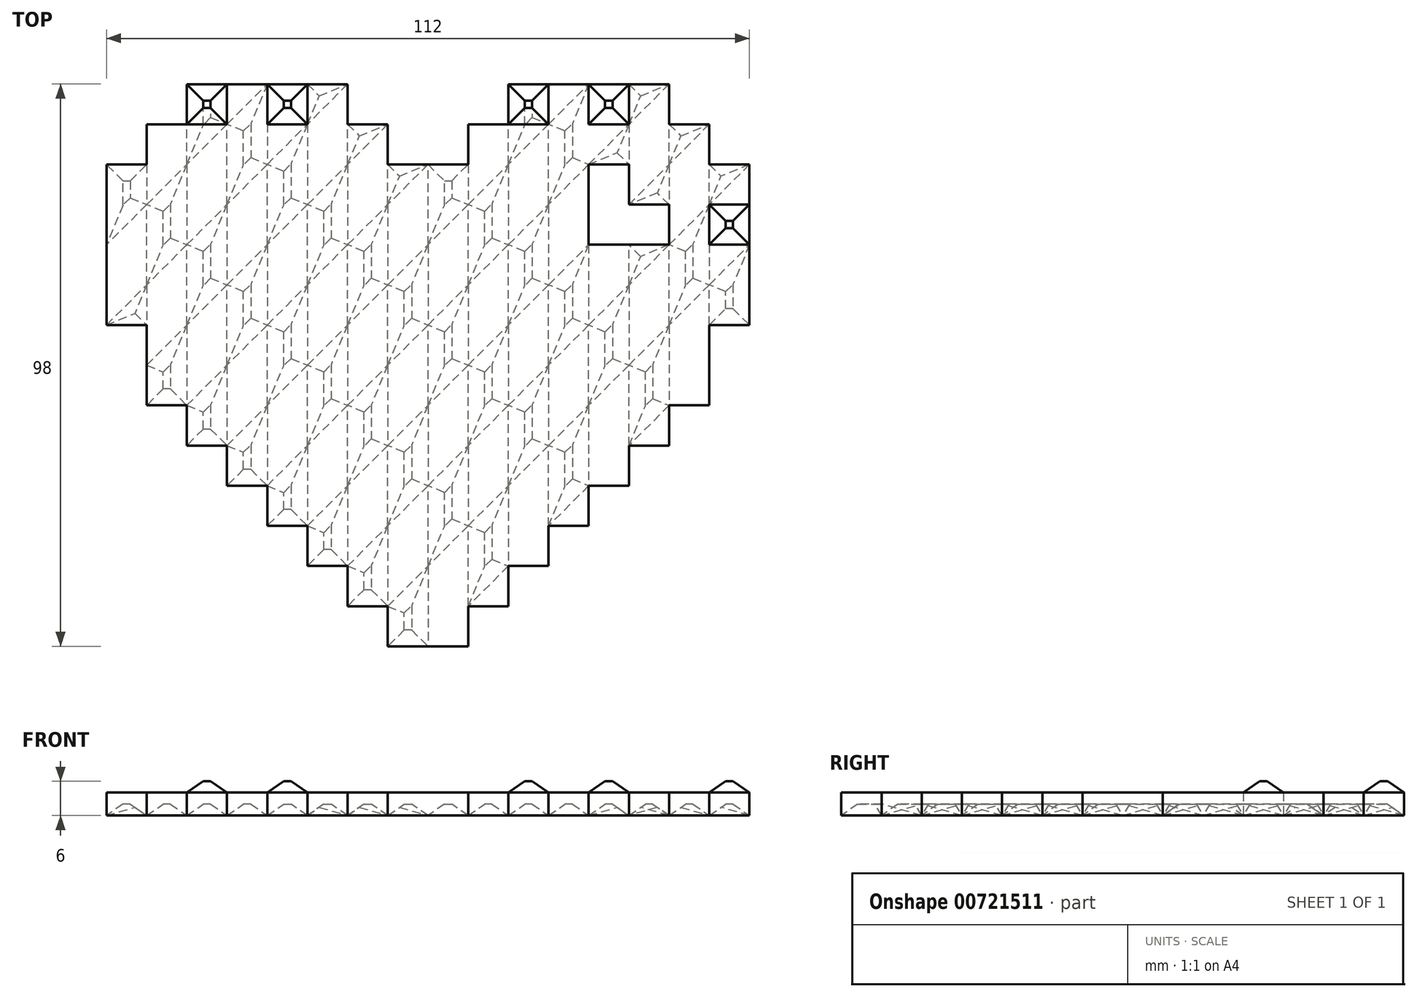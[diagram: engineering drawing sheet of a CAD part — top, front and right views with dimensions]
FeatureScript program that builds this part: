
annotation { "Feature Type Name" : "Feature", "Feature Type Description" : "" }
export const myFeature = defineFeature(function(context is Context, id is Id, definition is map)
    precondition{}
    {
        {
            var Q0;
            Q0=qCreatedBy(makeId("Top.planeOp"),FACE);
            var sketch = newSketch(context, id + "F0", { "sketchPlane" : qUnion([Q0])});
            skLineSegment(sketch, "E0", {"start": v(25.3, 13.05) * mm, "end": v(25.3, 20.05) * mm});
            skLineSegment(sketch, "E1", {"start": v(18.3, 20.05) * mm, "end": v(18.3, 6.05) * mm});
            skLineSegment(sketch, "E2", {"start": v(18.3, 6.05) * mm, "end": v(32.3, 6.05) * mm});
            skLineSegment(sketch, "E3", {"start": v(32.3, 6.05) * mm, "end": v(32.3, 13.05) * mm});
            skLineSegment(sketch, "E4", {"start": v(32.3, 13.05) * mm, "end": v(25.3, 13.05) * mm});
            skLineSegment(sketch, "E5", {"start": v(39.3, 20.05) * mm, "end": v(39.3, 27.05) * mm});
            skLineSegment(sketch, "E6", {"start": v(39.3, 27.05) * mm, "end": v(32.3, 27.05) * mm});
            skLineSegment(sketch, "E7", {"start": v(32.3, 27.05) * mm, "end": v(32.3, 34.05) * mm});
            skLineSegment(sketch, "E8", {"start": v(32.3, 34.05) * mm, "end": v(4.3, 34.05) * mm});
            skLineSegment(sketch, "E9", {"start": v(4.3, 34.05) * mm, "end": v(4.3, 27.05) * mm});
            skLineSegment(sketch, "E10", {"start": v(4.3, 27.05) * mm, "end": v(-2.7, 27.05) * mm});
            skLineSegment(sketch, "E11", {"start": v(-2.7, 27.05) * mm, "end": v(-2.7, 20.05) * mm});
            skLineSegment(sketch, "E12", {"start": v(-2.7, 20.05) * mm, "end": v(-16.7, 20.05) * mm});
            skLineSegment(sketch, "E13", {"start": v(-16.7, 20.05) * mm, "end": v(-16.7, 27.05) * mm});
            skLineSegment(sketch, "E14", {"start": v(-16.7, 27.05) * mm, "end": v(-23.7, 27.05) * mm});
            skLineSegment(sketch, "E15", {"start": v(-23.7, 27.05) * mm, "end": v(-23.7, 34.05) * mm});
            skLineSegment(sketch, "E16", {"start": v(-23.7, 34.05) * mm, "end": v(-51.7, 34.05) * mm});
            skLineSegment(sketch, "E17", {"start": v(-51.7, 34.05) * mm, "end": v(-51.7, 27.05) * mm});
            skLineSegment(sketch, "E18", {"start": v(-51.7, 27.05) * mm, "end": v(-58.7, 27.05) * mm});
            skLineSegment(sketch, "E19", {"start": v(-58.7, 27.05) * mm, "end": v(-58.7, 20.05) * mm});
            skLineSegment(sketch, "E20", {"start": v(-58.7, 20.05) * mm, "end": v(-65.7, 20.05) * mm});
            skLineSegment(sketch, "E21", {"start": v(-65.7, 20.05) * mm, "end": v(-65.7, -7.95) * mm});
            skLineSegment(sketch, "E22", {"start": v(-65.7, -7.95) * mm, "end": v(-58.7, -7.95) * mm});
            skLineSegment(sketch, "E23", {"start": v(-58.7, -7.95) * mm, "end": v(-58.7, -21.95) * mm});
            skLineSegment(sketch, "E24", {"start": v(-58.7, -21.95) * mm, "end": v(-51.7, -21.95) * mm});
            skLineSegment(sketch, "E25", {"start": v(-51.7, -21.95) * mm, "end": v(-51.7, -28.95) * mm});
            skLineSegment(sketch, "E26", {"start": v(-51.7, -28.95) * mm, "end": v(-44.7, -28.95) * mm});
            skLineSegment(sketch, "E27", {"start": v(-44.7, -28.95) * mm, "end": v(-44.7, -35.95) * mm});
            skLineSegment(sketch, "E28", {"start": v(-44.7, -35.95) * mm, "end": v(-37.7, -35.95) * mm});
            skLineSegment(sketch, "E29", {"start": v(-37.7, -35.95) * mm, "end": v(-37.7, -42.95) * mm});
            skLineSegment(sketch, "E30", {"start": v(-37.7, -42.95) * mm, "end": v(-30.7, -42.95) * mm});
            skLineSegment(sketch, "E31", {"start": v(-30.7, -42.95) * mm, "end": v(-30.7, -49.95) * mm});
            skLineSegment(sketch, "E32", {"start": v(-30.7, -49.95) * mm, "end": v(-23.7, -49.95) * mm});
            skLineSegment(sketch, "E33", {"start": v(-23.7, -49.95) * mm, "end": v(-23.7, -56.95) * mm});
            skLineSegment(sketch, "E34", {"start": v(-23.7, -56.95) * mm, "end": v(-16.7, -56.95) * mm});
            skLineSegment(sketch, "E35", {"start": v(-16.7, -56.95) * mm, "end": v(-16.7, -63.95) * mm});
            skLineSegment(sketch, "E36", {"start": v(-16.7, -63.95) * mm, "end": v(-2.7, -63.95) * mm});
            skLineSegment(sketch, "E37", {"start": v(-2.7, -63.95) * mm, "end": v(-2.7, -56.95) * mm});
            skLineSegment(sketch, "E38", {"start": v(-2.7, -56.95) * mm, "end": v(4.3, -56.95) * mm});
            skLineSegment(sketch, "E39", {"start": v(4.3, -56.95) * mm, "end": v(4.3, -49.95) * mm});
            skLineSegment(sketch, "E40", {"start": v(4.3, -49.95) * mm, "end": v(11.3, -49.95) * mm});
            skLineSegment(sketch, "E41", {"start": v(11.3, -49.95) * mm, "end": v(11.3, -42.95) * mm});
            skLineSegment(sketch, "E42", {"start": v(11.3, -42.95) * mm, "end": v(18.3, -42.95) * mm});
            skLineSegment(sketch, "E43", {"start": v(18.3, -42.95) * mm, "end": v(18.3, -35.95) * mm});
            skLineSegment(sketch, "E44", {"start": v(18.3, -35.95) * mm, "end": v(25.3, -35.95) * mm});
            skLineSegment(sketch, "E45", {"start": v(25.3, -35.95) * mm, "end": v(25.3, -28.95) * mm});
            skLineSegment(sketch, "E46", {"start": v(25.3, -28.95) * mm, "end": v(32.3, -28.95) * mm});
            skLineSegment(sketch, "E47", {"start": v(32.3, -28.95) * mm, "end": v(32.3, -21.95) * mm});
            skLineSegment(sketch, "E48", {"start": v(32.3, -21.95) * mm, "end": v(39.3, -21.95) * mm});
            skLineSegment(sketch, "E49", {"start": v(39.3, -21.95) * mm, "end": v(39.3, -7.95) * mm});
            skLineSegment(sketch, "E50", {"start": v(39.3, -7.95) * mm, "end": v(46.3, -7.95) * mm});
            skLineSegment(sketch, "E51", {"start": v(46.3, -7.95) * mm, "end": v(46.3, 20.05) * mm});
            skLineSegment(sketch, "E52", {"start": v(46.3, 20.05) * mm, "end": v(39.3, 20.05) * mm});
            skLineSegment(sketch, "E53", {"start": v(18.3, 20.05) * mm, "end": v(25.3, 20.05) * mm});
            skSolve(sketch);
        }
        {
            var Q0;
            Q0=makeQuery(id+"F0.imprint","IMPRINT",FACE,{"disambiguationData":[TD([[makeQuery(id+"F0.imprint","IMPRINT",EDGE,{"derivedFrom":sQuery(id+"F0.wireOp",EDGE,"E0")}),-1.0]])]});
            extrude(context, id + "F1", {"entities" : qUnion([Q0]), "depth" : 4 * mm, "offsetDistance" : 25 * mm});
        }
        {
            var Q0;
            Q0=makeQuery(id+"F1.opExtrude","CAP_FACE",FACE,{"disambiguationData":[OSD([sQuery(id+"F0.wireOp",EDGE,"E0"),sQuery(id+"F0.wireOp",EDGE,"E1"),sQuery(id+"F0.wireOp",EDGE,"E2"),sQuery(id+"F0.wireOp",EDGE,"E3"),sQuery(id+"F0.wireOp",EDGE,"E4"),sQuery(id+"F0.wireOp",EDGE,"E5"),sQuery(id+"F0.wireOp",EDGE,"E6"),sQuery(id+"F0.wireOp",EDGE,"E7"),sQuery(id+"F0.wireOp",EDGE,"E8"),sQuery(id+"F0.wireOp",EDGE,"E9"),sQuery(id+"F0.wireOp",EDGE,"E10"),sQuery(id+"F0.wireOp",EDGE,"E11"),sQuery(id+"F0.wireOp",EDGE,"E12"),sQuery(id+"F0.wireOp",EDGE,"E13"),sQuery(id+"F0.wireOp",EDGE,"E14"),sQuery(id+"F0.wireOp",EDGE,"E15"),sQuery(id+"F0.wireOp",EDGE,"E16"),sQuery(id+"F0.wireOp",EDGE,"E17"),sQuery(id+"F0.wireOp",EDGE,"E18"),sQuery(id+"F0.wireOp",EDGE,"E19"),sQuery(id+"F0.wireOp",EDGE,"E20"),sQuery(id+"F0.wireOp",EDGE,"E21"),sQuery(id+"F0.wireOp",EDGE,"E22"),sQuery(id+"F0.wireOp",EDGE,"E23"),sQuery(id+"F0.wireOp",EDGE,"E24"),sQuery(id+"F0.wireOp",EDGE,"E25"),sQuery(id+"F0.wireOp",EDGE,"E26"),sQuery(id+"F0.wireOp",EDGE,"E27"),sQuery(id+"F0.wireOp",EDGE,"E28"),sQuery(id+"F0.wireOp",EDGE,"E29"),sQuery(id+"F0.wireOp",EDGE,"E30"),sQuery(id+"F0.wireOp",EDGE,"E31"),sQuery(id+"F0.wireOp",EDGE,"E32"),sQuery(id+"F0.wireOp",EDGE,"E33"),sQuery(id+"F0.wireOp",EDGE,"E34"),sQuery(id+"F0.wireOp",EDGE,"E35"),sQuery(id+"F0.wireOp",EDGE,"E36"),sQuery(id+"F0.wireOp",EDGE,"E37"),sQuery(id+"F0.wireOp",EDGE,"E38"),sQuery(id+"F0.wireOp",EDGE,"E39"),sQuery(id+"F0.wireOp",EDGE,"E40"),sQuery(id+"F0.wireOp",EDGE,"E41"),sQuery(id+"F0.wireOp",EDGE,"E42"),sQuery(id+"F0.wireOp",EDGE,"E43"),sQuery(id+"F0.wireOp",EDGE,"E44"),sQuery(id+"F0.wireOp",EDGE,"E45"),sQuery(id+"F0.wireOp",EDGE,"E46"),sQuery(id+"F0.wireOp",EDGE,"E47"),sQuery(id+"F0.wireOp",EDGE,"E48"),sQuery(id+"F0.wireOp",EDGE,"E49"),sQuery(id+"F0.wireOp",EDGE,"E50"),sQuery(id+"F0.wireOp",EDGE,"E51"),sQuery(id+"F0.wireOp",EDGE,"E52"),sQuery(id+"F0.wireOp",EDGE,"E53")])],"isStart":false});
            var sketch = newSketch(context, id + "F2", { "sketchPlane" : qUnion([Q0])});
            skLineSegment(sketch, "E54.bottom", {"start": v(-58.7, 27.05) * mm, "end": v(-65.7, 27.05) * mm});
            skLineSegment(sketch, "E54.top", {"start": v(-58.7, 34.05) * mm, "end": v(-65.7, 34.05) * mm});
            skLineSegment(sketch, "E54.left", {"start": v(-58.7, 27.05) * mm, "end": v(-58.7, 34.05) * mm});
            skLineSegment(sketch, "E54.right", {"start": v(-65.7, 27.05) * mm, "end": v(-65.7, 34.05) * mm});
            skLineSegment(sketch, "E55.0.1.0", {"start": v(-58.7, 20.05) * mm, "end": v(-58.7, 27.05) * mm});
            skLineSegment(sketch, "E55.0.1.2", {"start": v(-58.7, 20.05) * mm, "end": v(-65.7, 20.05) * mm});
            skLineSegment(sketch, "E55.0.1.3", {"start": v(-65.7, 20.05) * mm, "end": v(-65.7, 27.05) * mm});
            skLineSegment(sketch, "E55.0.2.0", {"start": v(-58.7, 13.05) * mm, "end": v(-58.7, 20.05) * mm});
            skLineSegment(sketch, "E55.0.2.1", {"start": v(-58.7, 20.05) * mm, "end": v(-65.7, 20.05) * mm});
            skLineSegment(sketch, "E55.0.2.2", {"start": v(-58.7, 13.05) * mm, "end": v(-65.7, 13.05) * mm});
            skLineSegment(sketch, "E55.0.2.3", {"start": v(-65.7, 13.05) * mm, "end": v(-65.7, 20.05) * mm});
            skLineSegment(sketch, "E55.0.3.0", {"start": v(-58.7, 6.05) * mm, "end": v(-58.7, 13.05) * mm});
            skLineSegment(sketch, "E55.0.3.1", {"start": v(-58.7, 13.05) * mm, "end": v(-65.7, 13.05) * mm});
            skLineSegment(sketch, "E55.0.3.2", {"start": v(-58.7, 6.05) * mm, "end": v(-65.7, 6.05) * mm});
            skLineSegment(sketch, "E55.0.3.3", {"start": v(-65.7, 6.05) * mm, "end": v(-65.7, 13.05) * mm});
            skLineSegment(sketch, "E55.0.4.0", {"start": v(-58.7, -0.95) * mm, "end": v(-58.7, 6.05) * mm});
            skLineSegment(sketch, "E55.0.4.1", {"start": v(-58.7, 6.05) * mm, "end": v(-65.7, 6.05) * mm});
            skLineSegment(sketch, "E55.0.4.2", {"start": v(-58.7, -0.95) * mm, "end": v(-65.7, -0.95) * mm});
            skLineSegment(sketch, "E55.0.4.3", {"start": v(-65.7, -0.95) * mm, "end": v(-65.7, 6.05) * mm});
            skLineSegment(sketch, "E55.0.5.0", {"start": v(-58.7, -7.95) * mm, "end": v(-58.7, -0.95) * mm});
            skLineSegment(sketch, "E55.0.5.1", {"start": v(-58.7, -0.95) * mm, "end": v(-65.7, -0.95) * mm});
            skLineSegment(sketch, "E55.0.5.2", {"start": v(-58.7, -7.95) * mm, "end": v(-65.7, -7.95) * mm});
            skLineSegment(sketch, "E55.0.5.3", {"start": v(-65.7, -7.95) * mm, "end": v(-65.7, -0.95) * mm});
            skLineSegment(sketch, "E55.0.6.0", {"start": v(-58.7, -14.95) * mm, "end": v(-58.7, -7.95) * mm});
            skLineSegment(sketch, "E55.0.6.1", {"start": v(-58.7, -7.95) * mm, "end": v(-65.7, -7.95) * mm});
            skLineSegment(sketch, "E55.0.6.2", {"start": v(-58.7, -14.95) * mm, "end": v(-65.7, -14.95) * mm});
            skLineSegment(sketch, "E55.0.6.3", {"start": v(-65.7, -14.95) * mm, "end": v(-65.7, -7.95) * mm});
            skLineSegment(sketch, "E55.0.7.0", {"start": v(-58.7, -21.95) * mm, "end": v(-58.7, -14.95) * mm});
            skLineSegment(sketch, "E55.0.7.1", {"start": v(-58.7, -14.95) * mm, "end": v(-65.7, -14.95) * mm});
            skLineSegment(sketch, "E55.0.7.2", {"start": v(-58.7, -21.95) * mm, "end": v(-65.7, -21.95) * mm});
            skLineSegment(sketch, "E55.0.7.3", {"start": v(-65.7, -21.95) * mm, "end": v(-65.7, -14.95) * mm});
            skLineSegment(sketch, "E55.0.8.0", {"start": v(-58.7, -28.95) * mm, "end": v(-58.7, -21.95) * mm});
            skLineSegment(sketch, "E55.0.8.1", {"start": v(-58.7, -21.95) * mm, "end": v(-65.7, -21.95) * mm});
            skLineSegment(sketch, "E55.0.8.2", {"start": v(-58.7, -28.95) * mm, "end": v(-65.7, -28.95) * mm});
            skLineSegment(sketch, "E55.0.8.3", {"start": v(-65.7, -28.95) * mm, "end": v(-65.7, -21.95) * mm});
            skLineSegment(sketch, "E55.0.9.0", {"start": v(-58.7, -35.95) * mm, "end": v(-58.7, -28.95) * mm});
            skLineSegment(sketch, "E55.0.9.1", {"start": v(-58.7, -28.95) * mm, "end": v(-65.7, -28.95) * mm});
            skLineSegment(sketch, "E55.0.9.2", {"start": v(-58.7, -35.95) * mm, "end": v(-65.7, -35.95) * mm});
            skLineSegment(sketch, "E55.0.9.3", {"start": v(-65.7, -35.95) * mm, "end": v(-65.7, -28.95) * mm});
            skLineSegment(sketch, "E55.0.10.0", {"start": v(-58.7, -42.95) * mm, "end": v(-58.7, -35.95) * mm});
            skLineSegment(sketch, "E55.0.10.1", {"start": v(-58.7, -35.95) * mm, "end": v(-65.7, -35.95) * mm});
            skLineSegment(sketch, "E55.0.10.2", {"start": v(-58.7, -42.95) * mm, "end": v(-65.7, -42.95) * mm});
            skLineSegment(sketch, "E55.0.10.3", {"start": v(-65.7, -42.95) * mm, "end": v(-65.7, -35.95) * mm});
            skLineSegment(sketch, "E55.0.11.0", {"start": v(-58.7, -49.95) * mm, "end": v(-58.7, -42.95) * mm});
            skLineSegment(sketch, "E55.0.11.1", {"start": v(-58.7, -42.95) * mm, "end": v(-65.7, -42.95) * mm});
            skLineSegment(sketch, "E55.0.11.2", {"start": v(-58.7, -49.95) * mm, "end": v(-65.7, -49.95) * mm});
            skLineSegment(sketch, "E55.0.11.3", {"start": v(-65.7, -49.95) * mm, "end": v(-65.7, -42.95) * mm});
            skLineSegment(sketch, "E55.0.12.0", {"start": v(-58.7, -56.95) * mm, "end": v(-58.7, -49.95) * mm});
            skLineSegment(sketch, "E55.0.12.1", {"start": v(-58.7, -49.95) * mm, "end": v(-65.7, -49.95) * mm});
            skLineSegment(sketch, "E55.0.12.2", {"start": v(-58.7, -56.95) * mm, "end": v(-65.7, -56.95) * mm});
            skLineSegment(sketch, "E55.0.12.3", {"start": v(-65.7, -56.95) * mm, "end": v(-65.7, -49.95) * mm});
            skLineSegment(sketch, "E55.0.13.0", {"start": v(-58.7, -63.95) * mm, "end": v(-58.7, -56.95) * mm});
            skLineSegment(sketch, "E55.0.13.1", {"start": v(-58.7, -56.95) * mm, "end": v(-65.7, -56.95) * mm});
            skLineSegment(sketch, "E55.0.13.2", {"start": v(-58.7, -63.95) * mm, "end": v(-65.7, -63.95) * mm});
            skLineSegment(sketch, "E55.0.13.3", {"start": v(-65.7, -63.95) * mm, "end": v(-65.7, -56.95) * mm});
            skLineSegment(sketch, "E55.0.14.0", {"start": v(-58.7, -70.95) * mm, "end": v(-58.7, -63.95) * mm});
            skLineSegment(sketch, "E55.0.14.1", {"start": v(-58.7, -63.95) * mm, "end": v(-65.7, -63.95) * mm});
            skLineSegment(sketch, "E55.0.14.2", {"start": v(-58.7, -70.95) * mm, "end": v(-65.7, -70.95) * mm});
            skLineSegment(sketch, "E55.0.14.3", {"start": v(-65.7, -70.95) * mm, "end": v(-65.7, -63.95) * mm});
            skLineSegment(sketch, "E55.0.15.0", {"start": v(-58.7, -77.95) * mm, "end": v(-58.7, -70.95) * mm});
            skLineSegment(sketch, "E55.0.15.1", {"start": v(-58.7, -70.95) * mm, "end": v(-65.7, -70.95) * mm});
            skLineSegment(sketch, "E55.0.15.2", {"start": v(-58.7, -77.95) * mm, "end": v(-65.7, -77.95) * mm});
            skLineSegment(sketch, "E55.0.15.3", {"start": v(-65.7, -77.95) * mm, "end": v(-65.7, -70.95) * mm});
            skLineSegment(sketch, "E55.1.0.0", {"start": v(-51.7, 27.05) * mm, "end": v(-51.7, 34.05) * mm});
            skLineSegment(sketch, "E55.1.0.1", {"start": v(-51.7, 34.05) * mm, "end": v(-58.7, 34.05) * mm});
            skLineSegment(sketch, "E55.1.0.2", {"start": v(-51.7, 27.05) * mm, "end": v(-58.7, 27.05) * mm});
            skLineSegment(sketch, "E55.1.1.0", {"start": v(-51.7, 20.05) * mm, "end": v(-51.7, 27.05) * mm});
            skLineSegment(sketch, "E55.1.1.1", {"start": v(-51.7, 27.05) * mm, "end": v(-58.7, 27.05) * mm});
            skLineSegment(sketch, "E55.1.1.2", {"start": v(-51.7, 20.05) * mm, "end": v(-58.7, 20.05) * mm});
            skLineSegment(sketch, "E55.1.1.3", {"start": v(-58.7, 20.05) * mm, "end": v(-58.7, 27.05) * mm});
            skLineSegment(sketch, "E55.1.2.0", {"start": v(-51.7, 13.05) * mm, "end": v(-51.7, 20.05) * mm});
            skLineSegment(sketch, "E55.1.2.1", {"start": v(-51.7, 20.05) * mm, "end": v(-58.7, 20.05) * mm});
            skLineSegment(sketch, "E55.1.2.2", {"start": v(-51.7, 13.05) * mm, "end": v(-58.7, 13.05) * mm});
            skLineSegment(sketch, "E55.1.2.3", {"start": v(-58.7, 13.05) * mm, "end": v(-58.7, 20.05) * mm});
            skLineSegment(sketch, "E55.1.3.0", {"start": v(-51.7, 6.05) * mm, "end": v(-51.7, 13.05) * mm});
            skLineSegment(sketch, "E55.1.3.1", {"start": v(-51.7, 13.05) * mm, "end": v(-58.7, 13.05) * mm});
            skLineSegment(sketch, "E55.1.3.2", {"start": v(-51.7, 6.05) * mm, "end": v(-58.7, 6.05) * mm});
            skLineSegment(sketch, "E55.1.3.3", {"start": v(-58.7, 6.05) * mm, "end": v(-58.7, 13.05) * mm});
            skLineSegment(sketch, "E55.1.4.0", {"start": v(-51.7, -0.95) * mm, "end": v(-51.7, 6.05) * mm});
            skLineSegment(sketch, "E55.1.4.1", {"start": v(-51.7, 6.05) * mm, "end": v(-58.7, 6.05) * mm});
            skLineSegment(sketch, "E55.1.4.2", {"start": v(-51.7, -0.95) * mm, "end": v(-58.7, -0.95) * mm});
            skLineSegment(sketch, "E55.1.4.3", {"start": v(-58.7, -0.95) * mm, "end": v(-58.7, 6.05) * mm});
            skLineSegment(sketch, "E55.1.5.0", {"start": v(-51.7, -7.95) * mm, "end": v(-51.7, -0.95) * mm});
            skLineSegment(sketch, "E55.1.5.1", {"start": v(-51.7, -0.95) * mm, "end": v(-58.7, -0.95) * mm});
            skLineSegment(sketch, "E55.1.5.2", {"start": v(-51.7, -7.95) * mm, "end": v(-58.7, -7.95) * mm});
            skLineSegment(sketch, "E55.1.5.3", {"start": v(-58.7, -7.95) * mm, "end": v(-58.7, -0.95) * mm});
            skLineSegment(sketch, "E55.1.6.0", {"start": v(-51.7, -14.95) * mm, "end": v(-51.7, -7.95) * mm});
            skLineSegment(sketch, "E55.1.6.1", {"start": v(-51.7, -7.95) * mm, "end": v(-58.7, -7.95) * mm});
            skLineSegment(sketch, "E55.1.6.2", {"start": v(-51.7, -14.95) * mm, "end": v(-58.7, -14.95) * mm});
            skLineSegment(sketch, "E55.1.6.3", {"start": v(-58.7, -14.95) * mm, "end": v(-58.7, -7.95) * mm});
            skLineSegment(sketch, "E55.1.7.0", {"start": v(-51.7, -21.95) * mm, "end": v(-51.7, -14.95) * mm});
            skLineSegment(sketch, "E55.1.7.1", {"start": v(-51.7, -14.95) * mm, "end": v(-58.7, -14.95) * mm});
            skLineSegment(sketch, "E55.1.7.2", {"start": v(-51.7, -21.95) * mm, "end": v(-58.7, -21.95) * mm});
            skLineSegment(sketch, "E55.1.7.3", {"start": v(-58.7, -21.95) * mm, "end": v(-58.7, -14.95) * mm});
            skLineSegment(sketch, "E55.1.8.0", {"start": v(-51.7, -28.95) * mm, "end": v(-51.7, -21.95) * mm});
            skLineSegment(sketch, "E55.1.8.1", {"start": v(-51.7, -21.95) * mm, "end": v(-58.7, -21.95) * mm});
            skLineSegment(sketch, "E55.1.8.2", {"start": v(-51.7, -28.95) * mm, "end": v(-58.7, -28.95) * mm});
            skLineSegment(sketch, "E55.1.8.3", {"start": v(-58.7, -28.95) * mm, "end": v(-58.7, -21.95) * mm});
            skLineSegment(sketch, "E55.1.9.0", {"start": v(-51.7, -35.95) * mm, "end": v(-51.7, -28.95) * mm});
            skLineSegment(sketch, "E55.1.9.1", {"start": v(-51.7, -28.95) * mm, "end": v(-58.7, -28.95) * mm});
            skLineSegment(sketch, "E55.1.9.2", {"start": v(-51.7, -35.95) * mm, "end": v(-58.7, -35.95) * mm});
            skLineSegment(sketch, "E55.1.9.3", {"start": v(-58.7, -35.95) * mm, "end": v(-58.7, -28.95) * mm});
            skLineSegment(sketch, "E55.1.10.0", {"start": v(-51.7, -42.95) * mm, "end": v(-51.7, -35.95) * mm});
            skLineSegment(sketch, "E55.1.10.1", {"start": v(-51.7, -35.95) * mm, "end": v(-58.7, -35.95) * mm});
            skLineSegment(sketch, "E55.1.10.2", {"start": v(-51.7, -42.95) * mm, "end": v(-58.7, -42.95) * mm});
            skLineSegment(sketch, "E55.1.10.3", {"start": v(-58.7, -42.95) * mm, "end": v(-58.7, -35.95) * mm});
            skLineSegment(sketch, "E55.1.11.0", {"start": v(-51.7, -49.95) * mm, "end": v(-51.7, -42.95) * mm});
            skLineSegment(sketch, "E55.1.11.1", {"start": v(-51.7, -42.95) * mm, "end": v(-58.7, -42.95) * mm});
            skLineSegment(sketch, "E55.1.11.2", {"start": v(-51.7, -49.95) * mm, "end": v(-58.7, -49.95) * mm});
            skLineSegment(sketch, "E55.1.11.3", {"start": v(-58.7, -49.95) * mm, "end": v(-58.7, -42.95) * mm});
            skLineSegment(sketch, "E55.1.12.0", {"start": v(-51.7, -56.95) * mm, "end": v(-51.7, -49.95) * mm});
            skLineSegment(sketch, "E55.1.12.1", {"start": v(-51.7, -49.95) * mm, "end": v(-58.7, -49.95) * mm});
            skLineSegment(sketch, "E55.1.12.2", {"start": v(-51.7, -56.95) * mm, "end": v(-58.7, -56.95) * mm});
            skLineSegment(sketch, "E55.1.12.3", {"start": v(-58.7, -56.95) * mm, "end": v(-58.7, -49.95) * mm});
            skLineSegment(sketch, "E55.1.13.0", {"start": v(-51.7, -63.95) * mm, "end": v(-51.7, -56.95) * mm});
            skLineSegment(sketch, "E55.1.13.1", {"start": v(-51.7, -56.95) * mm, "end": v(-58.7, -56.95) * mm});
            skLineSegment(sketch, "E55.1.13.2", {"start": v(-51.7, -63.95) * mm, "end": v(-58.7, -63.95) * mm});
            skLineSegment(sketch, "E55.1.13.3", {"start": v(-58.7, -63.95) * mm, "end": v(-58.7, -56.95) * mm});
            skLineSegment(sketch, "E55.1.14.0", {"start": v(-51.7, -70.95) * mm, "end": v(-51.7, -63.95) * mm});
            skLineSegment(sketch, "E55.1.14.1", {"start": v(-51.7, -63.95) * mm, "end": v(-58.7, -63.95) * mm});
            skLineSegment(sketch, "E55.1.14.2", {"start": v(-51.7, -70.95) * mm, "end": v(-58.7, -70.95) * mm});
            skLineSegment(sketch, "E55.1.14.3", {"start": v(-58.7, -70.95) * mm, "end": v(-58.7, -63.95) * mm});
            skLineSegment(sketch, "E55.1.15.0", {"start": v(-51.7, -77.95) * mm, "end": v(-51.7, -70.95) * mm});
            skLineSegment(sketch, "E55.1.15.1", {"start": v(-51.7, -70.95) * mm, "end": v(-58.7, -70.95) * mm});
            skLineSegment(sketch, "E55.1.15.2", {"start": v(-51.7, -77.95) * mm, "end": v(-58.7, -77.95) * mm});
            skLineSegment(sketch, "E55.1.15.3", {"start": v(-58.7, -77.95) * mm, "end": v(-58.7, -70.95) * mm});
            skLineSegment(sketch, "E55.2.0.0", {"start": v(-44.7, 27.05) * mm, "end": v(-44.7, 34.05) * mm});
            skLineSegment(sketch, "E55.2.0.1", {"start": v(-44.7, 34.05) * mm, "end": v(-51.7, 34.05) * mm});
            skLineSegment(sketch, "E55.2.0.2", {"start": v(-44.7, 27.05) * mm, "end": v(-51.7, 27.05) * mm});
            skLineSegment(sketch, "E55.2.0.3", {"start": v(-51.7, 27.05) * mm, "end": v(-51.7, 34.05) * mm});
            skLineSegment(sketch, "E55.2.1.0", {"start": v(-44.7, 20.05) * mm, "end": v(-44.7, 27.05) * mm});
            skLineSegment(sketch, "E55.2.1.1", {"start": v(-44.7, 27.05) * mm, "end": v(-51.7, 27.05) * mm});
            skLineSegment(sketch, "E55.2.1.2", {"start": v(-44.7, 20.05) * mm, "end": v(-51.7, 20.05) * mm});
            skLineSegment(sketch, "E55.2.1.3", {"start": v(-51.7, 20.05) * mm, "end": v(-51.7, 27.05) * mm});
            skLineSegment(sketch, "E55.2.2.0", {"start": v(-44.7, 13.05) * mm, "end": v(-44.7, 20.05) * mm});
            skLineSegment(sketch, "E55.2.2.1", {"start": v(-44.7, 20.05) * mm, "end": v(-51.7, 20.05) * mm});
            skLineSegment(sketch, "E55.2.2.2", {"start": v(-44.7, 13.05) * mm, "end": v(-51.7, 13.05) * mm});
            skLineSegment(sketch, "E55.2.2.3", {"start": v(-51.7, 13.05) * mm, "end": v(-51.7, 20.05) * mm});
            skLineSegment(sketch, "E55.2.3.0", {"start": v(-44.7, 6.05) * mm, "end": v(-44.7, 13.05) * mm});
            skLineSegment(sketch, "E55.2.3.1", {"start": v(-44.7, 13.05) * mm, "end": v(-51.7, 13.05) * mm});
            skLineSegment(sketch, "E55.2.3.2", {"start": v(-44.7, 6.05) * mm, "end": v(-51.7, 6.05) * mm});
            skLineSegment(sketch, "E55.2.3.3", {"start": v(-51.7, 6.05) * mm, "end": v(-51.7, 13.05) * mm});
            skLineSegment(sketch, "E55.2.4.0", {"start": v(-44.7, -0.95) * mm, "end": v(-44.7, 6.05) * mm});
            skLineSegment(sketch, "E55.2.4.1", {"start": v(-44.7, 6.05) * mm, "end": v(-51.7, 6.05) * mm});
            skLineSegment(sketch, "E55.2.4.2", {"start": v(-44.7, -0.95) * mm, "end": v(-51.7, -0.95) * mm});
            skLineSegment(sketch, "E55.2.4.3", {"start": v(-51.7, -0.95) * mm, "end": v(-51.7, 6.05) * mm});
            skLineSegment(sketch, "E55.2.5.0", {"start": v(-44.7, -7.95) * mm, "end": v(-44.7, -0.95) * mm});
            skLineSegment(sketch, "E55.2.5.1", {"start": v(-44.7, -0.95) * mm, "end": v(-51.7, -0.95) * mm});
            skLineSegment(sketch, "E55.2.5.2", {"start": v(-44.7, -7.95) * mm, "end": v(-51.7, -7.95) * mm});
            skLineSegment(sketch, "E55.2.5.3", {"start": v(-51.7, -7.95) * mm, "end": v(-51.7, -0.95) * mm});
            skLineSegment(sketch, "E55.2.6.0", {"start": v(-44.7, -14.95) * mm, "end": v(-44.7, -7.95) * mm});
            skLineSegment(sketch, "E55.2.6.1", {"start": v(-44.7, -7.95) * mm, "end": v(-51.7, -7.95) * mm});
            skLineSegment(sketch, "E55.2.6.2", {"start": v(-44.7, -14.95) * mm, "end": v(-51.7, -14.95) * mm});
            skLineSegment(sketch, "E55.2.6.3", {"start": v(-51.7, -14.95) * mm, "end": v(-51.7, -7.95) * mm});
            skLineSegment(sketch, "E55.2.7.0", {"start": v(-44.7, -21.95) * mm, "end": v(-44.7, -14.95) * mm});
            skLineSegment(sketch, "E55.2.7.1", {"start": v(-44.7, -14.95) * mm, "end": v(-51.7, -14.95) * mm});
            skLineSegment(sketch, "E55.2.7.2", {"start": v(-44.7, -21.95) * mm, "end": v(-51.7, -21.95) * mm});
            skLineSegment(sketch, "E55.2.7.3", {"start": v(-51.7, -21.95) * mm, "end": v(-51.7, -14.95) * mm});
            skLineSegment(sketch, "E55.2.8.0", {"start": v(-44.7, -28.95) * mm, "end": v(-44.7, -21.95) * mm});
            skLineSegment(sketch, "E55.2.8.1", {"start": v(-44.7, -21.95) * mm, "end": v(-51.7, -21.95) * mm});
            skLineSegment(sketch, "E55.2.8.2", {"start": v(-44.7, -28.95) * mm, "end": v(-51.7, -28.95) * mm});
            skLineSegment(sketch, "E55.2.8.3", {"start": v(-51.7, -28.95) * mm, "end": v(-51.7, -21.95) * mm});
            skLineSegment(sketch, "E55.2.9.0", {"start": v(-44.7, -35.95) * mm, "end": v(-44.7, -28.95) * mm});
            skLineSegment(sketch, "E55.2.9.1", {"start": v(-44.7, -28.95) * mm, "end": v(-51.7, -28.95) * mm});
            skLineSegment(sketch, "E55.2.9.2", {"start": v(-44.7, -35.95) * mm, "end": v(-51.7, -35.95) * mm});
            skLineSegment(sketch, "E55.2.9.3", {"start": v(-51.7, -35.95) * mm, "end": v(-51.7, -28.95) * mm});
            skLineSegment(sketch, "E55.2.10.0", {"start": v(-44.7, -42.95) * mm, "end": v(-44.7, -35.95) * mm});
            skLineSegment(sketch, "E55.2.10.1", {"start": v(-44.7, -35.95) * mm, "end": v(-51.7, -35.95) * mm});
            skLineSegment(sketch, "E55.2.10.2", {"start": v(-44.7, -42.95) * mm, "end": v(-51.7, -42.95) * mm});
            skLineSegment(sketch, "E55.2.10.3", {"start": v(-51.7, -42.95) * mm, "end": v(-51.7, -35.95) * mm});
            skLineSegment(sketch, "E55.2.11.0", {"start": v(-44.7, -49.95) * mm, "end": v(-44.7, -42.95) * mm});
            skLineSegment(sketch, "E55.2.11.1", {"start": v(-44.7, -42.95) * mm, "end": v(-51.7, -42.95) * mm});
            skLineSegment(sketch, "E55.2.11.2", {"start": v(-44.7, -49.95) * mm, "end": v(-51.7, -49.95) * mm});
            skLineSegment(sketch, "E55.2.11.3", {"start": v(-51.7, -49.95) * mm, "end": v(-51.7, -42.95) * mm});
            skLineSegment(sketch, "E55.2.12.0", {"start": v(-44.7, -56.95) * mm, "end": v(-44.7, -49.95) * mm});
            skLineSegment(sketch, "E55.2.12.1", {"start": v(-44.7, -49.95) * mm, "end": v(-51.7, -49.95) * mm});
            skLineSegment(sketch, "E55.2.12.2", {"start": v(-44.7, -56.95) * mm, "end": v(-51.7, -56.95) * mm});
            skLineSegment(sketch, "E55.2.12.3", {"start": v(-51.7, -56.95) * mm, "end": v(-51.7, -49.95) * mm});
            skLineSegment(sketch, "E55.2.13.0", {"start": v(-44.7, -63.95) * mm, "end": v(-44.7, -56.95) * mm});
            skLineSegment(sketch, "E55.2.13.1", {"start": v(-44.7, -56.95) * mm, "end": v(-51.7, -56.95) * mm});
            skLineSegment(sketch, "E55.2.13.2", {"start": v(-44.7, -63.95) * mm, "end": v(-51.7, -63.95) * mm});
            skLineSegment(sketch, "E55.2.13.3", {"start": v(-51.7, -63.95) * mm, "end": v(-51.7, -56.95) * mm});
            skLineSegment(sketch, "E55.2.14.0", {"start": v(-44.7, -70.95) * mm, "end": v(-44.7, -63.95) * mm});
            skLineSegment(sketch, "E55.2.14.1", {"start": v(-44.7, -63.95) * mm, "end": v(-51.7, -63.95) * mm});
            skLineSegment(sketch, "E55.2.14.2", {"start": v(-44.7, -70.95) * mm, "end": v(-51.7, -70.95) * mm});
            skLineSegment(sketch, "E55.2.14.3", {"start": v(-51.7, -70.95) * mm, "end": v(-51.7, -63.95) * mm});
            skLineSegment(sketch, "E55.2.15.0", {"start": v(-44.7, -77.95) * mm, "end": v(-44.7, -70.95) * mm});
            skLineSegment(sketch, "E55.2.15.1", {"start": v(-44.7, -70.95) * mm, "end": v(-51.7, -70.95) * mm});
            skLineSegment(sketch, "E55.2.15.2", {"start": v(-44.7, -77.95) * mm, "end": v(-51.7, -77.95) * mm});
            skLineSegment(sketch, "E55.2.15.3", {"start": v(-51.7, -77.95) * mm, "end": v(-51.7, -70.95) * mm});
            skLineSegment(sketch, "E55.3.0.0", {"start": v(-37.7, 27.05) * mm, "end": v(-37.7, 34.05) * mm});
            skLineSegment(sketch, "E55.3.0.1", {"start": v(-37.7, 34.05) * mm, "end": v(-44.7, 34.05) * mm});
            skLineSegment(sketch, "E55.3.0.2", {"start": v(-37.7, 27.05) * mm, "end": v(-44.7, 27.05) * mm});
            skLineSegment(sketch, "E55.3.0.3", {"start": v(-44.7, 27.05) * mm, "end": v(-44.7, 34.05) * mm});
            skLineSegment(sketch, "E55.3.1.0", {"start": v(-37.7, 20.05) * mm, "end": v(-37.7, 27.05) * mm});
            skLineSegment(sketch, "E55.3.1.1", {"start": v(-37.7, 27.05) * mm, "end": v(-44.7, 27.05) * mm});
            skLineSegment(sketch, "E55.3.1.2", {"start": v(-37.7, 20.05) * mm, "end": v(-44.7, 20.05) * mm});
            skLineSegment(sketch, "E55.3.1.3", {"start": v(-44.7, 20.05) * mm, "end": v(-44.7, 27.05) * mm});
            skLineSegment(sketch, "E55.3.2.0", {"start": v(-37.7, 13.05) * mm, "end": v(-37.7, 20.05) * mm});
            skLineSegment(sketch, "E55.3.2.1", {"start": v(-37.7, 20.05) * mm, "end": v(-44.7, 20.05) * mm});
            skLineSegment(sketch, "E55.3.2.2", {"start": v(-37.7, 13.05) * mm, "end": v(-44.7, 13.05) * mm});
            skLineSegment(sketch, "E55.3.2.3", {"start": v(-44.7, 13.05) * mm, "end": v(-44.7, 20.05) * mm});
            skLineSegment(sketch, "E55.3.3.0", {"start": v(-37.7, 6.05) * mm, "end": v(-37.7, 13.05) * mm});
            skLineSegment(sketch, "E55.3.3.1", {"start": v(-37.7, 13.05) * mm, "end": v(-44.7, 13.05) * mm});
            skLineSegment(sketch, "E55.3.3.2", {"start": v(-37.7, 6.05) * mm, "end": v(-44.7, 6.05) * mm});
            skLineSegment(sketch, "E55.3.3.3", {"start": v(-44.7, 6.05) * mm, "end": v(-44.7, 13.05) * mm});
            skLineSegment(sketch, "E55.3.4.0", {"start": v(-37.7, -0.95) * mm, "end": v(-37.7, 6.05) * mm});
            skLineSegment(sketch, "E55.3.4.1", {"start": v(-37.7, 6.05) * mm, "end": v(-44.7, 6.05) * mm});
            skLineSegment(sketch, "E55.3.4.2", {"start": v(-37.7, -0.95) * mm, "end": v(-44.7, -0.95) * mm});
            skLineSegment(sketch, "E55.3.4.3", {"start": v(-44.7, -0.95) * mm, "end": v(-44.7, 6.05) * mm});
            skLineSegment(sketch, "E55.3.5.0", {"start": v(-37.7, -7.95) * mm, "end": v(-37.7, -0.95) * mm});
            skLineSegment(sketch, "E55.3.5.1", {"start": v(-37.7, -0.95) * mm, "end": v(-44.7, -0.95) * mm});
            skLineSegment(sketch, "E55.3.5.2", {"start": v(-37.7, -7.95) * mm, "end": v(-44.7, -7.95) * mm});
            skLineSegment(sketch, "E55.3.5.3", {"start": v(-44.7, -7.95) * mm, "end": v(-44.7, -0.95) * mm});
            skLineSegment(sketch, "E55.3.6.0", {"start": v(-37.7, -14.95) * mm, "end": v(-37.7, -7.95) * mm});
            skLineSegment(sketch, "E55.3.6.1", {"start": v(-37.7, -7.95) * mm, "end": v(-44.7, -7.95) * mm});
            skLineSegment(sketch, "E55.3.6.2", {"start": v(-37.7, -14.95) * mm, "end": v(-44.7, -14.95) * mm});
            skLineSegment(sketch, "E55.3.6.3", {"start": v(-44.7, -14.95) * mm, "end": v(-44.7, -7.95) * mm});
            skLineSegment(sketch, "E55.3.7.0", {"start": v(-37.7, -21.95) * mm, "end": v(-37.7, -14.95) * mm});
            skLineSegment(sketch, "E55.3.7.1", {"start": v(-37.7, -14.95) * mm, "end": v(-44.7, -14.95) * mm});
            skLineSegment(sketch, "E55.3.7.2", {"start": v(-37.7, -21.95) * mm, "end": v(-44.7, -21.95) * mm});
            skLineSegment(sketch, "E55.3.7.3", {"start": v(-44.7, -21.95) * mm, "end": v(-44.7, -14.95) * mm});
            skLineSegment(sketch, "E55.3.8.0", {"start": v(-37.7, -28.95) * mm, "end": v(-37.7, -21.95) * mm});
            skLineSegment(sketch, "E55.3.8.1", {"start": v(-37.7, -21.95) * mm, "end": v(-44.7, -21.95) * mm});
            skLineSegment(sketch, "E55.3.8.2", {"start": v(-37.7, -28.95) * mm, "end": v(-44.7, -28.95) * mm});
            skLineSegment(sketch, "E55.3.8.3", {"start": v(-44.7, -28.95) * mm, "end": v(-44.7, -21.95) * mm});
            skLineSegment(sketch, "E55.3.9.0", {"start": v(-37.7, -35.95) * mm, "end": v(-37.7, -28.95) * mm});
            skLineSegment(sketch, "E55.3.9.1", {"start": v(-37.7, -28.95) * mm, "end": v(-44.7, -28.95) * mm});
            skLineSegment(sketch, "E55.3.9.2", {"start": v(-37.7, -35.95) * mm, "end": v(-44.7, -35.95) * mm});
            skLineSegment(sketch, "E55.3.9.3", {"start": v(-44.7, -35.95) * mm, "end": v(-44.7, -28.95) * mm});
            skLineSegment(sketch, "E55.3.10.0", {"start": v(-37.7, -42.95) * mm, "end": v(-37.7, -35.95) * mm});
            skLineSegment(sketch, "E55.3.10.1", {"start": v(-37.7, -35.95) * mm, "end": v(-44.7, -35.95) * mm});
            skLineSegment(sketch, "E55.3.10.2", {"start": v(-37.7, -42.95) * mm, "end": v(-44.7, -42.95) * mm});
            skLineSegment(sketch, "E55.3.10.3", {"start": v(-44.7, -42.95) * mm, "end": v(-44.7, -35.95) * mm});
            skLineSegment(sketch, "E55.3.11.0", {"start": v(-37.7, -49.95) * mm, "end": v(-37.7, -42.95) * mm});
            skLineSegment(sketch, "E55.3.11.1", {"start": v(-37.7, -42.95) * mm, "end": v(-44.7, -42.95) * mm});
            skLineSegment(sketch, "E55.3.11.2", {"start": v(-37.7, -49.95) * mm, "end": v(-44.7, -49.95) * mm});
            skLineSegment(sketch, "E55.3.11.3", {"start": v(-44.7, -49.95) * mm, "end": v(-44.7, -42.95) * mm});
            skLineSegment(sketch, "E55.3.12.0", {"start": v(-37.7, -56.95) * mm, "end": v(-37.7, -49.95) * mm});
            skLineSegment(sketch, "E55.3.12.1", {"start": v(-37.7, -49.95) * mm, "end": v(-44.7, -49.95) * mm});
            skLineSegment(sketch, "E55.3.12.2", {"start": v(-37.7, -56.95) * mm, "end": v(-44.7, -56.95) * mm});
            skLineSegment(sketch, "E55.3.12.3", {"start": v(-44.7, -56.95) * mm, "end": v(-44.7, -49.95) * mm});
            skLineSegment(sketch, "E55.3.13.0", {"start": v(-37.7, -63.95) * mm, "end": v(-37.7, -56.95) * mm});
            skLineSegment(sketch, "E55.3.13.1", {"start": v(-37.7, -56.95) * mm, "end": v(-44.7, -56.95) * mm});
            skLineSegment(sketch, "E55.3.13.2", {"start": v(-37.7, -63.95) * mm, "end": v(-44.7, -63.95) * mm});
            skLineSegment(sketch, "E55.3.13.3", {"start": v(-44.7, -63.95) * mm, "end": v(-44.7, -56.95) * mm});
            skLineSegment(sketch, "E55.3.14.0", {"start": v(-37.7, -70.95) * mm, "end": v(-37.7, -63.95) * mm});
            skLineSegment(sketch, "E55.3.14.1", {"start": v(-37.7, -63.95) * mm, "end": v(-44.7, -63.95) * mm});
            skLineSegment(sketch, "E55.3.14.2", {"start": v(-37.7, -70.95) * mm, "end": v(-44.7, -70.95) * mm});
            skLineSegment(sketch, "E55.3.14.3", {"start": v(-44.7, -70.95) * mm, "end": v(-44.7, -63.95) * mm});
            skLineSegment(sketch, "E55.3.15.0", {"start": v(-37.7, -77.95) * mm, "end": v(-37.7, -70.95) * mm});
            skLineSegment(sketch, "E55.3.15.1", {"start": v(-37.7, -70.95) * mm, "end": v(-44.7, -70.95) * mm});
            skLineSegment(sketch, "E55.3.15.2", {"start": v(-37.7, -77.95) * mm, "end": v(-44.7, -77.95) * mm});
            skLineSegment(sketch, "E55.3.15.3", {"start": v(-44.7, -77.95) * mm, "end": v(-44.7, -70.95) * mm});
            skLineSegment(sketch, "E55.4.0.0", {"start": v(-30.7, 27.05) * mm, "end": v(-30.7, 34.05) * mm});
            skLineSegment(sketch, "E55.4.0.1", {"start": v(-30.7, 34.05) * mm, "end": v(-37.7, 34.05) * mm});
            skLineSegment(sketch, "E55.4.0.2", {"start": v(-30.7, 27.05) * mm, "end": v(-37.7, 27.05) * mm});
            skLineSegment(sketch, "E55.4.0.3", {"start": v(-37.7, 27.05) * mm, "end": v(-37.7, 34.05) * mm});
            skLineSegment(sketch, "E55.4.1.0", {"start": v(-30.7, 20.05) * mm, "end": v(-30.7, 27.05) * mm});
            skLineSegment(sketch, "E55.4.1.1", {"start": v(-30.7, 27.05) * mm, "end": v(-37.7, 27.05) * mm});
            skLineSegment(sketch, "E55.4.1.2", {"start": v(-30.7, 20.05) * mm, "end": v(-37.7, 20.05) * mm});
            skLineSegment(sketch, "E55.4.1.3", {"start": v(-37.7, 20.05) * mm, "end": v(-37.7, 27.05) * mm});
            skLineSegment(sketch, "E55.4.2.0", {"start": v(-30.7, 13.05) * mm, "end": v(-30.7, 20.05) * mm});
            skLineSegment(sketch, "E55.4.2.1", {"start": v(-30.7, 20.05) * mm, "end": v(-37.7, 20.05) * mm});
            skLineSegment(sketch, "E55.4.2.2", {"start": v(-30.7, 13.05) * mm, "end": v(-37.7, 13.05) * mm});
            skLineSegment(sketch, "E55.4.2.3", {"start": v(-37.7, 13.05) * mm, "end": v(-37.7, 20.05) * mm});
            skLineSegment(sketch, "E55.4.3.0", {"start": v(-30.7, 6.05) * mm, "end": v(-30.7, 13.05) * mm});
            skLineSegment(sketch, "E55.4.3.1", {"start": v(-30.7, 13.05) * mm, "end": v(-37.7, 13.05) * mm});
            skLineSegment(sketch, "E55.4.3.2", {"start": v(-30.7, 6.05) * mm, "end": v(-37.7, 6.05) * mm});
            skLineSegment(sketch, "E55.4.3.3", {"start": v(-37.7, 6.05) * mm, "end": v(-37.7, 13.05) * mm});
            skLineSegment(sketch, "E55.4.4.0", {"start": v(-30.7, -0.95) * mm, "end": v(-30.7, 6.05) * mm});
            skLineSegment(sketch, "E55.4.4.1", {"start": v(-30.7, 6.05) * mm, "end": v(-37.7, 6.05) * mm});
            skLineSegment(sketch, "E55.4.4.2", {"start": v(-30.7, -0.95) * mm, "end": v(-37.7, -0.95) * mm});
            skLineSegment(sketch, "E55.4.4.3", {"start": v(-37.7, -0.95) * mm, "end": v(-37.7, 6.05) * mm});
            skLineSegment(sketch, "E55.4.5.0", {"start": v(-30.7, -7.95) * mm, "end": v(-30.7, -0.95) * mm});
            skLineSegment(sketch, "E55.4.5.1", {"start": v(-30.7, -0.95) * mm, "end": v(-37.7, -0.95) * mm});
            skLineSegment(sketch, "E55.4.5.2", {"start": v(-30.7, -7.95) * mm, "end": v(-37.7, -7.95) * mm});
            skLineSegment(sketch, "E55.4.5.3", {"start": v(-37.7, -7.95) * mm, "end": v(-37.7, -0.95) * mm});
            skLineSegment(sketch, "E55.4.6.0", {"start": v(-30.7, -14.95) * mm, "end": v(-30.7, -7.95) * mm});
            skLineSegment(sketch, "E55.4.6.1", {"start": v(-30.7, -7.95) * mm, "end": v(-37.7, -7.95) * mm});
            skLineSegment(sketch, "E55.4.6.2", {"start": v(-30.7, -14.95) * mm, "end": v(-37.7, -14.95) * mm});
            skLineSegment(sketch, "E55.4.6.3", {"start": v(-37.7, -14.95) * mm, "end": v(-37.7, -7.95) * mm});
            skLineSegment(sketch, "E55.4.7.0", {"start": v(-30.7, -21.95) * mm, "end": v(-30.7, -14.95) * mm});
            skLineSegment(sketch, "E55.4.7.1", {"start": v(-30.7, -14.95) * mm, "end": v(-37.7, -14.95) * mm});
            skLineSegment(sketch, "E55.4.7.2", {"start": v(-30.7, -21.95) * mm, "end": v(-37.7, -21.95) * mm});
            skLineSegment(sketch, "E55.4.7.3", {"start": v(-37.7, -21.95) * mm, "end": v(-37.7, -14.95) * mm});
            skLineSegment(sketch, "E55.4.8.0", {"start": v(-30.7, -28.95) * mm, "end": v(-30.7, -21.95) * mm});
            skLineSegment(sketch, "E55.4.8.1", {"start": v(-30.7, -21.95) * mm, "end": v(-37.7, -21.95) * mm});
            skLineSegment(sketch, "E55.4.8.2", {"start": v(-30.7, -28.95) * mm, "end": v(-37.7, -28.95) * mm});
            skLineSegment(sketch, "E55.4.8.3", {"start": v(-37.7, -28.95) * mm, "end": v(-37.7, -21.95) * mm});
            skLineSegment(sketch, "E55.4.9.0", {"start": v(-30.7, -35.95) * mm, "end": v(-30.7, -28.95) * mm});
            skLineSegment(sketch, "E55.4.9.1", {"start": v(-30.7, -28.95) * mm, "end": v(-37.7, -28.95) * mm});
            skLineSegment(sketch, "E55.4.9.2", {"start": v(-30.7, -35.95) * mm, "end": v(-37.7, -35.95) * mm});
            skLineSegment(sketch, "E55.4.9.3", {"start": v(-37.7, -35.95) * mm, "end": v(-37.7, -28.95) * mm});
            skLineSegment(sketch, "E55.4.10.0", {"start": v(-30.7, -42.95) * mm, "end": v(-30.7, -35.95) * mm});
            skLineSegment(sketch, "E55.4.10.1", {"start": v(-30.7, -35.95) * mm, "end": v(-37.7, -35.95) * mm});
            skLineSegment(sketch, "E55.4.10.2", {"start": v(-30.7, -42.95) * mm, "end": v(-37.7, -42.95) * mm});
            skLineSegment(sketch, "E55.4.10.3", {"start": v(-37.7, -42.95) * mm, "end": v(-37.7, -35.95) * mm});
            skLineSegment(sketch, "E55.4.11.0", {"start": v(-30.7, -49.95) * mm, "end": v(-30.7, -42.95) * mm});
            skLineSegment(sketch, "E55.4.11.1", {"start": v(-30.7, -42.95) * mm, "end": v(-37.7, -42.95) * mm});
            skLineSegment(sketch, "E55.4.11.2", {"start": v(-30.7, -49.95) * mm, "end": v(-37.7, -49.95) * mm});
            skLineSegment(sketch, "E55.4.11.3", {"start": v(-37.7, -49.95) * mm, "end": v(-37.7, -42.95) * mm});
            skLineSegment(sketch, "E55.4.12.0", {"start": v(-30.7, -56.95) * mm, "end": v(-30.7, -49.95) * mm});
            skLineSegment(sketch, "E55.4.12.1", {"start": v(-30.7, -49.95) * mm, "end": v(-37.7, -49.95) * mm});
            skLineSegment(sketch, "E55.4.12.2", {"start": v(-30.7, -56.95) * mm, "end": v(-37.7, -56.95) * mm});
            skLineSegment(sketch, "E55.4.12.3", {"start": v(-37.7, -56.95) * mm, "end": v(-37.7, -49.95) * mm});
            skLineSegment(sketch, "E55.4.13.0", {"start": v(-30.7, -63.95) * mm, "end": v(-30.7, -56.95) * mm});
            skLineSegment(sketch, "E55.4.13.1", {"start": v(-30.7, -56.95) * mm, "end": v(-37.7, -56.95) * mm});
            skLineSegment(sketch, "E55.4.13.2", {"start": v(-30.7, -63.95) * mm, "end": v(-37.7, -63.95) * mm});
            skLineSegment(sketch, "E55.4.13.3", {"start": v(-37.7, -63.95) * mm, "end": v(-37.7, -56.95) * mm});
            skLineSegment(sketch, "E55.4.14.0", {"start": v(-30.7, -70.95) * mm, "end": v(-30.7, -63.95) * mm});
            skLineSegment(sketch, "E55.4.14.1", {"start": v(-30.7, -63.95) * mm, "end": v(-37.7, -63.95) * mm});
            skLineSegment(sketch, "E55.4.14.2", {"start": v(-30.7, -70.95) * mm, "end": v(-37.7, -70.95) * mm});
            skLineSegment(sketch, "E55.4.14.3", {"start": v(-37.7, -70.95) * mm, "end": v(-37.7, -63.95) * mm});
            skLineSegment(sketch, "E55.4.15.0", {"start": v(-30.7, -77.95) * mm, "end": v(-30.7, -70.95) * mm});
            skLineSegment(sketch, "E55.4.15.1", {"start": v(-30.7, -70.95) * mm, "end": v(-37.7, -70.95) * mm});
            skLineSegment(sketch, "E55.4.15.2", {"start": v(-30.7, -77.95) * mm, "end": v(-37.7, -77.95) * mm});
            skLineSegment(sketch, "E55.4.15.3", {"start": v(-37.7, -77.95) * mm, "end": v(-37.7, -70.95) * mm});
            skLineSegment(sketch, "E55.5.0.0", {"start": v(-23.7, 27.05) * mm, "end": v(-23.7, 34.05) * mm});
            skLineSegment(sketch, "E55.5.0.1", {"start": v(-23.7, 34.05) * mm, "end": v(-30.7, 34.05) * mm});
            skLineSegment(sketch, "E55.5.0.2", {"start": v(-23.7, 27.05) * mm, "end": v(-30.7, 27.05) * mm});
            skLineSegment(sketch, "E55.5.0.3", {"start": v(-30.7, 27.05) * mm, "end": v(-30.7, 34.05) * mm});
            skLineSegment(sketch, "E55.5.1.0", {"start": v(-23.7, 20.05) * mm, "end": v(-23.7, 27.05) * mm});
            skLineSegment(sketch, "E55.5.1.1", {"start": v(-23.7, 27.05) * mm, "end": v(-30.7, 27.05) * mm});
            skLineSegment(sketch, "E55.5.1.2", {"start": v(-23.7, 20.05) * mm, "end": v(-30.7, 20.05) * mm});
            skLineSegment(sketch, "E55.5.1.3", {"start": v(-30.7, 20.05) * mm, "end": v(-30.7, 27.05) * mm});
            skLineSegment(sketch, "E55.5.2.0", {"start": v(-23.7, 13.05) * mm, "end": v(-23.7, 20.05) * mm});
            skLineSegment(sketch, "E55.5.2.1", {"start": v(-23.7, 20.05) * mm, "end": v(-30.7, 20.05) * mm});
            skLineSegment(sketch, "E55.5.2.2", {"start": v(-23.7, 13.05) * mm, "end": v(-30.7, 13.05) * mm});
            skLineSegment(sketch, "E55.5.2.3", {"start": v(-30.7, 13.05) * mm, "end": v(-30.7, 20.05) * mm});
            skLineSegment(sketch, "E55.5.3.0", {"start": v(-23.7, 6.05) * mm, "end": v(-23.7, 13.05) * mm});
            skLineSegment(sketch, "E55.5.3.1", {"start": v(-23.7, 13.05) * mm, "end": v(-30.7, 13.05) * mm});
            skLineSegment(sketch, "E55.5.3.2", {"start": v(-23.7, 6.05) * mm, "end": v(-30.7, 6.05) * mm});
            skLineSegment(sketch, "E55.5.3.3", {"start": v(-30.7, 6.05) * mm, "end": v(-30.7, 13.05) * mm});
            skLineSegment(sketch, "E55.5.4.0", {"start": v(-23.7, -0.95) * mm, "end": v(-23.7, 6.05) * mm});
            skLineSegment(sketch, "E55.5.4.1", {"start": v(-23.7, 6.05) * mm, "end": v(-30.7, 6.05) * mm});
            skLineSegment(sketch, "E55.5.4.2", {"start": v(-23.7, -0.95) * mm, "end": v(-30.7, -0.95) * mm});
            skLineSegment(sketch, "E55.5.4.3", {"start": v(-30.7, -0.95) * mm, "end": v(-30.7, 6.05) * mm});
            skLineSegment(sketch, "E55.5.5.0", {"start": v(-23.7, -7.95) * mm, "end": v(-23.7, -0.95) * mm});
            skLineSegment(sketch, "E55.5.5.1", {"start": v(-23.7, -0.95) * mm, "end": v(-30.7, -0.95) * mm});
            skLineSegment(sketch, "E55.5.5.2", {"start": v(-23.7, -7.95) * mm, "end": v(-30.7, -7.95) * mm});
            skLineSegment(sketch, "E55.5.5.3", {"start": v(-30.7, -7.95) * mm, "end": v(-30.7, -0.95) * mm});
            skLineSegment(sketch, "E55.5.6.0", {"start": v(-23.7, -14.95) * mm, "end": v(-23.7, -7.95) * mm});
            skLineSegment(sketch, "E55.5.6.1", {"start": v(-23.7, -7.95) * mm, "end": v(-30.7, -7.95) * mm});
            skLineSegment(sketch, "E55.5.6.2", {"start": v(-23.7, -14.95) * mm, "end": v(-30.7, -14.95) * mm});
            skLineSegment(sketch, "E55.5.6.3", {"start": v(-30.7, -14.95) * mm, "end": v(-30.7, -7.95) * mm});
            skLineSegment(sketch, "E55.5.7.0", {"start": v(-23.7, -21.95) * mm, "end": v(-23.7, -14.95) * mm});
            skLineSegment(sketch, "E55.5.7.1", {"start": v(-23.7, -14.95) * mm, "end": v(-30.7, -14.95) * mm});
            skLineSegment(sketch, "E55.5.7.2", {"start": v(-23.7, -21.95) * mm, "end": v(-30.7, -21.95) * mm});
            skLineSegment(sketch, "E55.5.7.3", {"start": v(-30.7, -21.95) * mm, "end": v(-30.7, -14.95) * mm});
            skLineSegment(sketch, "E55.5.8.0", {"start": v(-23.7, -28.95) * mm, "end": v(-23.7, -21.95) * mm});
            skLineSegment(sketch, "E55.5.8.1", {"start": v(-23.7, -21.95) * mm, "end": v(-30.7, -21.95) * mm});
            skLineSegment(sketch, "E55.5.8.2", {"start": v(-23.7, -28.95) * mm, "end": v(-30.7, -28.95) * mm});
            skLineSegment(sketch, "E55.5.8.3", {"start": v(-30.7, -28.95) * mm, "end": v(-30.7, -21.95) * mm});
            skLineSegment(sketch, "E55.5.9.0", {"start": v(-23.7, -35.95) * mm, "end": v(-23.7, -28.95) * mm});
            skLineSegment(sketch, "E55.5.9.1", {"start": v(-23.7, -28.95) * mm, "end": v(-30.7, -28.95) * mm});
            skLineSegment(sketch, "E55.5.9.2", {"start": v(-23.7, -35.95) * mm, "end": v(-30.7, -35.95) * mm});
            skLineSegment(sketch, "E55.5.9.3", {"start": v(-30.7, -35.95) * mm, "end": v(-30.7, -28.95) * mm});
            skLineSegment(sketch, "E55.5.10.0", {"start": v(-23.7, -42.95) * mm, "end": v(-23.7, -35.95) * mm});
            skLineSegment(sketch, "E55.5.10.1", {"start": v(-23.7, -35.95) * mm, "end": v(-30.7, -35.95) * mm});
            skLineSegment(sketch, "E55.5.10.2", {"start": v(-23.7, -42.95) * mm, "end": v(-30.7, -42.95) * mm});
            skLineSegment(sketch, "E55.5.10.3", {"start": v(-30.7, -42.95) * mm, "end": v(-30.7, -35.95) * mm});
            skLineSegment(sketch, "E55.5.11.0", {"start": v(-23.7, -49.95) * mm, "end": v(-23.7, -42.95) * mm});
            skLineSegment(sketch, "E55.5.11.1", {"start": v(-23.7, -42.95) * mm, "end": v(-30.7, -42.95) * mm});
            skLineSegment(sketch, "E55.5.11.2", {"start": v(-23.7, -49.95) * mm, "end": v(-30.7, -49.95) * mm});
            skLineSegment(sketch, "E55.5.11.3", {"start": v(-30.7, -49.95) * mm, "end": v(-30.7, -42.95) * mm});
            skLineSegment(sketch, "E55.5.12.0", {"start": v(-23.7, -56.95) * mm, "end": v(-23.7, -49.95) * mm});
            skLineSegment(sketch, "E55.5.12.1", {"start": v(-23.7, -49.95) * mm, "end": v(-30.7, -49.95) * mm});
            skLineSegment(sketch, "E55.5.12.2", {"start": v(-23.7, -56.95) * mm, "end": v(-30.7, -56.95) * mm});
            skLineSegment(sketch, "E55.5.12.3", {"start": v(-30.7, -56.95) * mm, "end": v(-30.7, -49.95) * mm});
            skLineSegment(sketch, "E55.5.13.0", {"start": v(-23.7, -63.95) * mm, "end": v(-23.7, -56.95) * mm});
            skLineSegment(sketch, "E55.5.13.1", {"start": v(-23.7, -56.95) * mm, "end": v(-30.7, -56.95) * mm});
            skLineSegment(sketch, "E55.5.13.2", {"start": v(-23.7, -63.95) * mm, "end": v(-30.7, -63.95) * mm});
            skLineSegment(sketch, "E55.5.13.3", {"start": v(-30.7, -63.95) * mm, "end": v(-30.7, -56.95) * mm});
            skLineSegment(sketch, "E55.5.14.0", {"start": v(-23.7, -70.95) * mm, "end": v(-23.7, -63.95) * mm});
            skLineSegment(sketch, "E55.5.14.1", {"start": v(-23.7, -63.95) * mm, "end": v(-30.7, -63.95) * mm});
            skLineSegment(sketch, "E55.5.14.2", {"start": v(-23.7, -70.95) * mm, "end": v(-30.7, -70.95) * mm});
            skLineSegment(sketch, "E55.5.14.3", {"start": v(-30.7, -70.95) * mm, "end": v(-30.7, -63.95) * mm});
            skLineSegment(sketch, "E55.5.15.0", {"start": v(-23.7, -77.95) * mm, "end": v(-23.7, -70.95) * mm});
            skLineSegment(sketch, "E55.5.15.1", {"start": v(-23.7, -70.95) * mm, "end": v(-30.7, -70.95) * mm});
            skLineSegment(sketch, "E55.5.15.2", {"start": v(-23.7, -77.95) * mm, "end": v(-30.7, -77.95) * mm});
            skLineSegment(sketch, "E55.5.15.3", {"start": v(-30.7, -77.95) * mm, "end": v(-30.7, -70.95) * mm});
            skLineSegment(sketch, "E55.6.0.0", {"start": v(-16.7, 27.05) * mm, "end": v(-16.7, 34.05) * mm});
            skLineSegment(sketch, "E55.6.0.1", {"start": v(-16.7, 34.05) * mm, "end": v(-23.7, 34.05) * mm});
            skLineSegment(sketch, "E55.6.0.2", {"start": v(-16.7, 27.05) * mm, "end": v(-23.7, 27.05) * mm});
            skLineSegment(sketch, "E55.6.0.3", {"start": v(-23.7, 27.05) * mm, "end": v(-23.7, 34.05) * mm});
            skLineSegment(sketch, "E55.6.1.0", {"start": v(-16.7, 20.05) * mm, "end": v(-16.7, 27.05) * mm});
            skLineSegment(sketch, "E55.6.1.1", {"start": v(-16.7, 27.05) * mm, "end": v(-23.7, 27.05) * mm});
            skLineSegment(sketch, "E55.6.1.2", {"start": v(-16.7, 20.05) * mm, "end": v(-23.7, 20.05) * mm});
            skLineSegment(sketch, "E55.6.1.3", {"start": v(-23.7, 20.05) * mm, "end": v(-23.7, 27.05) * mm});
            skLineSegment(sketch, "E55.6.2.0", {"start": v(-16.7, 13.05) * mm, "end": v(-16.7, 20.05) * mm});
            skLineSegment(sketch, "E55.6.2.1", {"start": v(-16.7, 20.05) * mm, "end": v(-23.7, 20.05) * mm});
            skLineSegment(sketch, "E55.6.2.2", {"start": v(-16.7, 13.05) * mm, "end": v(-23.7, 13.05) * mm});
            skLineSegment(sketch, "E55.6.2.3", {"start": v(-23.7, 13.05) * mm, "end": v(-23.7, 20.05) * mm});
            skLineSegment(sketch, "E55.6.3.0", {"start": v(-16.7, 6.05) * mm, "end": v(-16.7, 13.05) * mm});
            skLineSegment(sketch, "E55.6.3.1", {"start": v(-16.7, 13.05) * mm, "end": v(-23.7, 13.05) * mm});
            skLineSegment(sketch, "E55.6.3.2", {"start": v(-16.7, 6.05) * mm, "end": v(-23.7, 6.05) * mm});
            skLineSegment(sketch, "E55.6.3.3", {"start": v(-23.7, 6.05) * mm, "end": v(-23.7, 13.05) * mm});
            skLineSegment(sketch, "E55.6.4.0", {"start": v(-16.7, -0.95) * mm, "end": v(-16.7, 6.05) * mm});
            skLineSegment(sketch, "E55.6.4.1", {"start": v(-16.7, 6.05) * mm, "end": v(-23.7, 6.05) * mm});
            skLineSegment(sketch, "E55.6.4.2", {"start": v(-16.7, -0.95) * mm, "end": v(-23.7, -0.95) * mm});
            skLineSegment(sketch, "E55.6.4.3", {"start": v(-23.7, -0.95) * mm, "end": v(-23.7, 6.05) * mm});
            skLineSegment(sketch, "E55.6.5.0", {"start": v(-16.7, -7.95) * mm, "end": v(-16.7, -0.95) * mm});
            skLineSegment(sketch, "E55.6.5.1", {"start": v(-16.7, -0.95) * mm, "end": v(-23.7, -0.95) * mm});
            skLineSegment(sketch, "E55.6.5.2", {"start": v(-16.7, -7.95) * mm, "end": v(-23.7, -7.95) * mm});
            skLineSegment(sketch, "E55.6.5.3", {"start": v(-23.7, -7.95) * mm, "end": v(-23.7, -0.95) * mm});
            skLineSegment(sketch, "E55.6.6.0", {"start": v(-16.7, -14.95) * mm, "end": v(-16.7, -7.95) * mm});
            skLineSegment(sketch, "E55.6.6.1", {"start": v(-16.7, -7.95) * mm, "end": v(-23.7, -7.95) * mm});
            skLineSegment(sketch, "E55.6.6.2", {"start": v(-16.7, -14.95) * mm, "end": v(-23.7, -14.95) * mm});
            skLineSegment(sketch, "E55.6.6.3", {"start": v(-23.7, -14.95) * mm, "end": v(-23.7, -7.95) * mm});
            skLineSegment(sketch, "E55.6.7.0", {"start": v(-16.7, -21.95) * mm, "end": v(-16.7, -14.95) * mm});
            skLineSegment(sketch, "E55.6.7.1", {"start": v(-16.7, -14.95) * mm, "end": v(-23.7, -14.95) * mm});
            skLineSegment(sketch, "E55.6.7.2", {"start": v(-16.7, -21.95) * mm, "end": v(-23.7, -21.95) * mm});
            skLineSegment(sketch, "E55.6.7.3", {"start": v(-23.7, -21.95) * mm, "end": v(-23.7, -14.95) * mm});
            skLineSegment(sketch, "E55.6.8.0", {"start": v(-16.7, -28.95) * mm, "end": v(-16.7, -21.95) * mm});
            skLineSegment(sketch, "E55.6.8.1", {"start": v(-16.7, -21.95) * mm, "end": v(-23.7, -21.95) * mm});
            skLineSegment(sketch, "E55.6.8.2", {"start": v(-16.7, -28.95) * mm, "end": v(-23.7, -28.95) * mm});
            skLineSegment(sketch, "E55.6.8.3", {"start": v(-23.7, -28.95) * mm, "end": v(-23.7, -21.95) * mm});
            skLineSegment(sketch, "E55.6.9.0", {"start": v(-16.7, -35.95) * mm, "end": v(-16.7, -28.95) * mm});
            skLineSegment(sketch, "E55.6.9.1", {"start": v(-16.7, -28.95) * mm, "end": v(-23.7, -28.95) * mm});
            skLineSegment(sketch, "E55.6.9.2", {"start": v(-16.7, -35.95) * mm, "end": v(-23.7, -35.95) * mm});
            skLineSegment(sketch, "E55.6.9.3", {"start": v(-23.7, -35.95) * mm, "end": v(-23.7, -28.95) * mm});
            skLineSegment(sketch, "E55.6.10.0", {"start": v(-16.7, -42.95) * mm, "end": v(-16.7, -35.95) * mm});
            skLineSegment(sketch, "E55.6.10.1", {"start": v(-16.7, -35.95) * mm, "end": v(-23.7, -35.95) * mm});
            skLineSegment(sketch, "E55.6.10.2", {"start": v(-16.7, -42.95) * mm, "end": v(-23.7, -42.95) * mm});
            skLineSegment(sketch, "E55.6.10.3", {"start": v(-23.7, -42.95) * mm, "end": v(-23.7, -35.95) * mm});
            skLineSegment(sketch, "E55.6.11.0", {"start": v(-16.7, -49.95) * mm, "end": v(-16.7, -42.95) * mm});
            skLineSegment(sketch, "E55.6.11.1", {"start": v(-16.7, -42.95) * mm, "end": v(-23.7, -42.95) * mm});
            skLineSegment(sketch, "E55.6.11.2", {"start": v(-16.7, -49.95) * mm, "end": v(-23.7, -49.95) * mm});
            skLineSegment(sketch, "E55.6.11.3", {"start": v(-23.7, -49.95) * mm, "end": v(-23.7, -42.95) * mm});
            skLineSegment(sketch, "E55.6.12.0", {"start": v(-16.7, -56.95) * mm, "end": v(-16.7, -49.95) * mm});
            skLineSegment(sketch, "E55.6.12.1", {"start": v(-16.7, -49.95) * mm, "end": v(-23.7, -49.95) * mm});
            skLineSegment(sketch, "E55.6.12.2", {"start": v(-16.7, -56.95) * mm, "end": v(-23.7, -56.95) * mm});
            skLineSegment(sketch, "E55.6.12.3", {"start": v(-23.7, -56.95) * mm, "end": v(-23.7, -49.95) * mm});
            skLineSegment(sketch, "E55.6.13.0", {"start": v(-16.7, -63.95) * mm, "end": v(-16.7, -56.95) * mm});
            skLineSegment(sketch, "E55.6.13.1", {"start": v(-16.7, -56.95) * mm, "end": v(-23.7, -56.95) * mm});
            skLineSegment(sketch, "E55.6.13.2", {"start": v(-16.7, -63.95) * mm, "end": v(-23.7, -63.95) * mm});
            skLineSegment(sketch, "E55.6.13.3", {"start": v(-23.7, -63.95) * mm, "end": v(-23.7, -56.95) * mm});
            skLineSegment(sketch, "E55.6.14.0", {"start": v(-16.7, -70.95) * mm, "end": v(-16.7, -63.95) * mm});
            skLineSegment(sketch, "E55.6.14.1", {"start": v(-16.7, -63.95) * mm, "end": v(-23.7, -63.95) * mm});
            skLineSegment(sketch, "E55.6.14.2", {"start": v(-16.7, -70.95) * mm, "end": v(-23.7, -70.95) * mm});
            skLineSegment(sketch, "E55.6.14.3", {"start": v(-23.7, -70.95) * mm, "end": v(-23.7, -63.95) * mm});
            skLineSegment(sketch, "E55.6.15.0", {"start": v(-16.7, -77.95) * mm, "end": v(-16.7, -70.95) * mm});
            skLineSegment(sketch, "E55.6.15.1", {"start": v(-16.7, -70.95) * mm, "end": v(-23.7, -70.95) * mm});
            skLineSegment(sketch, "E55.6.15.2", {"start": v(-16.7, -77.95) * mm, "end": v(-23.7, -77.95) * mm});
            skLineSegment(sketch, "E55.6.15.3", {"start": v(-23.7, -77.95) * mm, "end": v(-23.7, -70.95) * mm});
            skLineSegment(sketch, "E55.7.0.0", {"start": v(-9.7, 27.05) * mm, "end": v(-9.7, 34.05) * mm});
            skLineSegment(sketch, "E55.7.0.1", {"start": v(-9.7, 34.05) * mm, "end": v(-16.7, 34.05) * mm});
            skLineSegment(sketch, "E55.7.0.2", {"start": v(-9.7, 27.05) * mm, "end": v(-16.7, 27.05) * mm});
            skLineSegment(sketch, "E55.7.0.3", {"start": v(-16.7, 27.05) * mm, "end": v(-16.7, 34.05) * mm});
            skLineSegment(sketch, "E55.7.1.0", {"start": v(-9.7, 20.05) * mm, "end": v(-9.7, 27.05) * mm});
            skLineSegment(sketch, "E55.7.1.1", {"start": v(-9.7, 27.05) * mm, "end": v(-16.7, 27.05) * mm});
            skLineSegment(sketch, "E55.7.1.2", {"start": v(-9.7, 20.05) * mm, "end": v(-16.7, 20.05) * mm});
            skLineSegment(sketch, "E55.7.1.3", {"start": v(-16.7, 20.05) * mm, "end": v(-16.7, 27.05) * mm});
            skLineSegment(sketch, "E55.7.2.0", {"start": v(-9.7, 13.05) * mm, "end": v(-9.7, 20.05) * mm});
            skLineSegment(sketch, "E55.7.2.1", {"start": v(-9.7, 20.05) * mm, "end": v(-16.7, 20.05) * mm});
            skLineSegment(sketch, "E55.7.2.2", {"start": v(-9.7, 13.05) * mm, "end": v(-16.7, 13.05) * mm});
            skLineSegment(sketch, "E55.7.2.3", {"start": v(-16.7, 13.05) * mm, "end": v(-16.7, 20.05) * mm});
            skLineSegment(sketch, "E55.7.3.0", {"start": v(-9.7, 6.05) * mm, "end": v(-9.7, 13.05) * mm});
            skLineSegment(sketch, "E55.7.3.1", {"start": v(-9.7, 13.05) * mm, "end": v(-16.7, 13.05) * mm});
            skLineSegment(sketch, "E55.7.3.2", {"start": v(-9.7, 6.05) * mm, "end": v(-16.7, 6.05) * mm});
            skLineSegment(sketch, "E55.7.3.3", {"start": v(-16.7, 6.05) * mm, "end": v(-16.7, 13.05) * mm});
            skLineSegment(sketch, "E55.7.4.0", {"start": v(-9.7, -0.95) * mm, "end": v(-9.7, 6.05) * mm});
            skLineSegment(sketch, "E55.7.4.1", {"start": v(-9.7, 6.05) * mm, "end": v(-16.7, 6.05) * mm});
            skLineSegment(sketch, "E55.7.4.2", {"start": v(-9.7, -0.95) * mm, "end": v(-16.7, -0.95) * mm});
            skLineSegment(sketch, "E55.7.4.3", {"start": v(-16.7, -0.95) * mm, "end": v(-16.7, 6.05) * mm});
            skLineSegment(sketch, "E55.7.5.0", {"start": v(-9.7, -7.95) * mm, "end": v(-9.7, -0.95) * mm});
            skLineSegment(sketch, "E55.7.5.1", {"start": v(-9.7, -0.95) * mm, "end": v(-16.7, -0.95) * mm});
            skLineSegment(sketch, "E55.7.5.2", {"start": v(-9.7, -7.95) * mm, "end": v(-16.7, -7.95) * mm});
            skLineSegment(sketch, "E55.7.5.3", {"start": v(-16.7, -7.95) * mm, "end": v(-16.7, -0.95) * mm});
            skLineSegment(sketch, "E55.7.6.0", {"start": v(-9.7, -14.95) * mm, "end": v(-9.7, -7.95) * mm});
            skLineSegment(sketch, "E55.7.6.1", {"start": v(-9.7, -7.95) * mm, "end": v(-16.7, -7.95) * mm});
            skLineSegment(sketch, "E55.7.6.2", {"start": v(-9.7, -14.95) * mm, "end": v(-16.7, -14.95) * mm});
            skLineSegment(sketch, "E55.7.6.3", {"start": v(-16.7, -14.95) * mm, "end": v(-16.7, -7.95) * mm});
            skLineSegment(sketch, "E55.7.7.0", {"start": v(-9.7, -21.95) * mm, "end": v(-9.7, -14.95) * mm});
            skLineSegment(sketch, "E55.7.7.1", {"start": v(-9.7, -14.95) * mm, "end": v(-16.7, -14.95) * mm});
            skLineSegment(sketch, "E55.7.7.2", {"start": v(-9.7, -21.95) * mm, "end": v(-16.7, -21.95) * mm});
            skLineSegment(sketch, "E55.7.7.3", {"start": v(-16.7, -21.95) * mm, "end": v(-16.7, -14.95) * mm});
            skLineSegment(sketch, "E55.7.8.0", {"start": v(-9.7, -28.95) * mm, "end": v(-9.7, -21.95) * mm});
            skLineSegment(sketch, "E55.7.8.1", {"start": v(-9.7, -21.95) * mm, "end": v(-16.7, -21.95) * mm});
            skLineSegment(sketch, "E55.7.8.2", {"start": v(-9.7, -28.95) * mm, "end": v(-16.7, -28.95) * mm});
            skLineSegment(sketch, "E55.7.8.3", {"start": v(-16.7, -28.95) * mm, "end": v(-16.7, -21.95) * mm});
            skLineSegment(sketch, "E55.7.9.0", {"start": v(-9.7, -35.95) * mm, "end": v(-9.7, -28.95) * mm});
            skLineSegment(sketch, "E55.7.9.1", {"start": v(-9.7, -28.95) * mm, "end": v(-16.7, -28.95) * mm});
            skLineSegment(sketch, "E55.7.9.2", {"start": v(-9.7, -35.95) * mm, "end": v(-16.7, -35.95) * mm});
            skLineSegment(sketch, "E55.7.9.3", {"start": v(-16.7, -35.95) * mm, "end": v(-16.7, -28.95) * mm});
            skLineSegment(sketch, "E55.7.10.0", {"start": v(-9.7, -42.95) * mm, "end": v(-9.7, -35.95) * mm});
            skLineSegment(sketch, "E55.7.10.1", {"start": v(-9.7, -35.95) * mm, "end": v(-16.7, -35.95) * mm});
            skLineSegment(sketch, "E55.7.10.2", {"start": v(-9.7, -42.95) * mm, "end": v(-16.7, -42.95) * mm});
            skLineSegment(sketch, "E55.7.10.3", {"start": v(-16.7, -42.95) * mm, "end": v(-16.7, -35.95) * mm});
            skLineSegment(sketch, "E55.7.11.0", {"start": v(-9.7, -49.95) * mm, "end": v(-9.7, -42.95) * mm});
            skLineSegment(sketch, "E55.7.11.1", {"start": v(-9.7, -42.95) * mm, "end": v(-16.7, -42.95) * mm});
            skLineSegment(sketch, "E55.7.11.2", {"start": v(-9.7, -49.95) * mm, "end": v(-16.7, -49.95) * mm});
            skLineSegment(sketch, "E55.7.11.3", {"start": v(-16.7, -49.95) * mm, "end": v(-16.7, -42.95) * mm});
            skLineSegment(sketch, "E55.7.12.0", {"start": v(-9.7, -56.95) * mm, "end": v(-9.7, -49.95) * mm});
            skLineSegment(sketch, "E55.7.12.1", {"start": v(-9.7, -49.95) * mm, "end": v(-16.7, -49.95) * mm});
            skLineSegment(sketch, "E55.7.12.2", {"start": v(-9.7, -56.95) * mm, "end": v(-16.7, -56.95) * mm});
            skLineSegment(sketch, "E55.7.12.3", {"start": v(-16.7, -56.95) * mm, "end": v(-16.7, -49.95) * mm});
            skLineSegment(sketch, "E55.7.13.0", {"start": v(-9.7, -63.95) * mm, "end": v(-9.7, -56.95) * mm});
            skLineSegment(sketch, "E55.7.13.1", {"start": v(-9.7, -56.95) * mm, "end": v(-16.7, -56.95) * mm});
            skLineSegment(sketch, "E55.7.13.2", {"start": v(-9.7, -63.95) * mm, "end": v(-16.7, -63.95) * mm});
            skLineSegment(sketch, "E55.7.13.3", {"start": v(-16.7, -63.95) * mm, "end": v(-16.7, -56.95) * mm});
            skLineSegment(sketch, "E55.7.14.0", {"start": v(-9.7, -70.95) * mm, "end": v(-9.7, -63.95) * mm});
            skLineSegment(sketch, "E55.7.14.1", {"start": v(-9.7, -63.95) * mm, "end": v(-16.7, -63.95) * mm});
            skLineSegment(sketch, "E55.7.14.2", {"start": v(-9.7, -70.95) * mm, "end": v(-16.7, -70.95) * mm});
            skLineSegment(sketch, "E55.7.14.3", {"start": v(-16.7, -70.95) * mm, "end": v(-16.7, -63.95) * mm});
            skLineSegment(sketch, "E55.7.15.0", {"start": v(-9.7, -77.95) * mm, "end": v(-9.7, -70.95) * mm});
            skLineSegment(sketch, "E55.7.15.1", {"start": v(-9.7, -70.95) * mm, "end": v(-16.7, -70.95) * mm});
            skLineSegment(sketch, "E55.7.15.2", {"start": v(-9.7, -77.95) * mm, "end": v(-16.7, -77.95) * mm});
            skLineSegment(sketch, "E55.7.15.3", {"start": v(-16.7, -77.95) * mm, "end": v(-16.7, -70.95) * mm});
            skLineSegment(sketch, "E55.8.0.0", {"start": v(-2.7, 27.05) * mm, "end": v(-2.7, 34.05) * mm});
            skLineSegment(sketch, "E55.8.0.1", {"start": v(-2.7, 34.05) * mm, "end": v(-9.7, 34.05) * mm});
            skLineSegment(sketch, "E55.8.0.2", {"start": v(-2.7, 27.05) * mm, "end": v(-9.7, 27.05) * mm});
            skLineSegment(sketch, "E55.8.0.3", {"start": v(-9.7, 27.05) * mm, "end": v(-9.7, 34.05) * mm});
            skLineSegment(sketch, "E55.8.1.0", {"start": v(-2.7, 20.05) * mm, "end": v(-2.7, 27.05) * mm});
            skLineSegment(sketch, "E55.8.1.1", {"start": v(-2.7, 27.05) * mm, "end": v(-9.7, 27.05) * mm});
            skLineSegment(sketch, "E55.8.1.2", {"start": v(-2.7, 20.05) * mm, "end": v(-9.7, 20.05) * mm});
            skLineSegment(sketch, "E55.8.1.3", {"start": v(-9.7, 20.05) * mm, "end": v(-9.7, 27.05) * mm});
            skLineSegment(sketch, "E55.8.2.0", {"start": v(-2.7, 13.05) * mm, "end": v(-2.7, 20.05) * mm});
            skLineSegment(sketch, "E55.8.2.1", {"start": v(-2.7, 20.05) * mm, "end": v(-9.7, 20.05) * mm});
            skLineSegment(sketch, "E55.8.2.2", {"start": v(-2.7, 13.05) * mm, "end": v(-9.7, 13.05) * mm});
            skLineSegment(sketch, "E55.8.2.3", {"start": v(-9.7, 13.05) * mm, "end": v(-9.7, 20.05) * mm});
            skLineSegment(sketch, "E55.8.3.0", {"start": v(-2.7, 6.05) * mm, "end": v(-2.7, 13.05) * mm});
            skLineSegment(sketch, "E55.8.3.1", {"start": v(-2.7, 13.05) * mm, "end": v(-9.7, 13.05) * mm});
            skLineSegment(sketch, "E55.8.3.2", {"start": v(-2.7, 6.05) * mm, "end": v(-9.7, 6.05) * mm});
            skLineSegment(sketch, "E55.8.3.3", {"start": v(-9.7, 6.05) * mm, "end": v(-9.7, 13.05) * mm});
            skLineSegment(sketch, "E55.8.4.0", {"start": v(-2.7, -0.95) * mm, "end": v(-2.7, 6.05) * mm});
            skLineSegment(sketch, "E55.8.4.1", {"start": v(-2.7, 6.05) * mm, "end": v(-9.7, 6.05) * mm});
            skLineSegment(sketch, "E55.8.4.2", {"start": v(-2.7, -0.95) * mm, "end": v(-9.7, -0.95) * mm});
            skLineSegment(sketch, "E55.8.4.3", {"start": v(-9.7, -0.95) * mm, "end": v(-9.7, 6.05) * mm});
            skLineSegment(sketch, "E55.8.5.0", {"start": v(-2.7, -7.95) * mm, "end": v(-2.7, -0.95) * mm});
            skLineSegment(sketch, "E55.8.5.1", {"start": v(-2.7, -0.95) * mm, "end": v(-9.7, -0.95) * mm});
            skLineSegment(sketch, "E55.8.5.2", {"start": v(-2.7, -7.95) * mm, "end": v(-9.7, -7.95) * mm});
            skLineSegment(sketch, "E55.8.5.3", {"start": v(-9.7, -7.95) * mm, "end": v(-9.7, -0.95) * mm});
            skLineSegment(sketch, "E55.8.6.0", {"start": v(-2.7, -14.95) * mm, "end": v(-2.7, -7.95) * mm});
            skLineSegment(sketch, "E55.8.6.1", {"start": v(-2.7, -7.95) * mm, "end": v(-9.7, -7.95) * mm});
            skLineSegment(sketch, "E55.8.6.2", {"start": v(-2.7, -14.95) * mm, "end": v(-9.7, -14.95) * mm});
            skLineSegment(sketch, "E55.8.6.3", {"start": v(-9.7, -14.95) * mm, "end": v(-9.7, -7.95) * mm});
            skLineSegment(sketch, "E55.8.7.0", {"start": v(-2.7, -21.95) * mm, "end": v(-2.7, -14.95) * mm});
            skLineSegment(sketch, "E55.8.7.1", {"start": v(-2.7, -14.95) * mm, "end": v(-9.7, -14.95) * mm});
            skLineSegment(sketch, "E55.8.7.2", {"start": v(-2.7, -21.95) * mm, "end": v(-9.7, -21.95) * mm});
            skLineSegment(sketch, "E55.8.7.3", {"start": v(-9.7, -21.95) * mm, "end": v(-9.7, -14.95) * mm});
            skLineSegment(sketch, "E55.8.8.0", {"start": v(-2.7, -28.95) * mm, "end": v(-2.7, -21.95) * mm});
            skLineSegment(sketch, "E55.8.8.1", {"start": v(-2.7, -21.95) * mm, "end": v(-9.7, -21.95) * mm});
            skLineSegment(sketch, "E55.8.8.2", {"start": v(-2.7, -28.95) * mm, "end": v(-9.7, -28.95) * mm});
            skLineSegment(sketch, "E55.8.8.3", {"start": v(-9.7, -28.95) * mm, "end": v(-9.7, -21.95) * mm});
            skLineSegment(sketch, "E55.8.9.0", {"start": v(-2.7, -35.95) * mm, "end": v(-2.7, -28.95) * mm});
            skLineSegment(sketch, "E55.8.9.1", {"start": v(-2.7, -28.95) * mm, "end": v(-9.7, -28.95) * mm});
            skLineSegment(sketch, "E55.8.9.2", {"start": v(-2.7, -35.95) * mm, "end": v(-9.7, -35.95) * mm});
            skLineSegment(sketch, "E55.8.9.3", {"start": v(-9.7, -35.95) * mm, "end": v(-9.7, -28.95) * mm});
            skLineSegment(sketch, "E55.8.10.0", {"start": v(-2.7, -42.95) * mm, "end": v(-2.7, -35.95) * mm});
            skLineSegment(sketch, "E55.8.10.1", {"start": v(-2.7, -35.95) * mm, "end": v(-9.7, -35.95) * mm});
            skLineSegment(sketch, "E55.8.10.2", {"start": v(-2.7, -42.95) * mm, "end": v(-9.7, -42.95) * mm});
            skLineSegment(sketch, "E55.8.10.3", {"start": v(-9.7, -42.95) * mm, "end": v(-9.7, -35.95) * mm});
            skLineSegment(sketch, "E55.8.11.0", {"start": v(-2.7, -49.95) * mm, "end": v(-2.7, -42.95) * mm});
            skLineSegment(sketch, "E55.8.11.1", {"start": v(-2.7, -42.95) * mm, "end": v(-9.7, -42.95) * mm});
            skLineSegment(sketch, "E55.8.11.2", {"start": v(-2.7, -49.95) * mm, "end": v(-9.7, -49.95) * mm});
            skLineSegment(sketch, "E55.8.11.3", {"start": v(-9.7, -49.95) * mm, "end": v(-9.7, -42.95) * mm});
            skLineSegment(sketch, "E55.8.12.0", {"start": v(-2.7, -56.95) * mm, "end": v(-2.7, -49.95) * mm});
            skLineSegment(sketch, "E55.8.12.1", {"start": v(-2.7, -49.95) * mm, "end": v(-9.7, -49.95) * mm});
            skLineSegment(sketch, "E55.8.12.2", {"start": v(-2.7, -56.95) * mm, "end": v(-9.7, -56.95) * mm});
            skLineSegment(sketch, "E55.8.12.3", {"start": v(-9.7, -56.95) * mm, "end": v(-9.7, -49.95) * mm});
            skLineSegment(sketch, "E55.8.13.0", {"start": v(-2.7, -63.95) * mm, "end": v(-2.7, -56.95) * mm});
            skLineSegment(sketch, "E55.8.13.1", {"start": v(-2.7, -56.95) * mm, "end": v(-9.7, -56.95) * mm});
            skLineSegment(sketch, "E55.8.13.2", {"start": v(-2.7, -63.95) * mm, "end": v(-9.7, -63.95) * mm});
            skLineSegment(sketch, "E55.8.13.3", {"start": v(-9.7, -63.95) * mm, "end": v(-9.7, -56.95) * mm});
            skLineSegment(sketch, "E55.8.14.0", {"start": v(-2.7, -70.95) * mm, "end": v(-2.7, -63.95) * mm});
            skLineSegment(sketch, "E55.8.14.1", {"start": v(-2.7, -63.95) * mm, "end": v(-9.7, -63.95) * mm});
            skLineSegment(sketch, "E55.8.14.2", {"start": v(-2.7, -70.95) * mm, "end": v(-9.7, -70.95) * mm});
            skLineSegment(sketch, "E55.8.14.3", {"start": v(-9.7, -70.95) * mm, "end": v(-9.7, -63.95) * mm});
            skLineSegment(sketch, "E55.8.15.0", {"start": v(-2.7, -77.95) * mm, "end": v(-2.7, -70.95) * mm});
            skLineSegment(sketch, "E55.8.15.1", {"start": v(-2.7, -70.95) * mm, "end": v(-9.7, -70.95) * mm});
            skLineSegment(sketch, "E55.8.15.2", {"start": v(-2.7, -77.95) * mm, "end": v(-9.7, -77.95) * mm});
            skLineSegment(sketch, "E55.8.15.3", {"start": v(-9.7, -77.95) * mm, "end": v(-9.7, -70.95) * mm});
            skLineSegment(sketch, "E55.9.0.0", {"start": v(4.3, 27.05) * mm, "end": v(4.3, 34.05) * mm});
            skLineSegment(sketch, "E55.9.0.1", {"start": v(4.3, 34.05) * mm, "end": v(-2.7, 34.05) * mm});
            skLineSegment(sketch, "E55.9.0.2", {"start": v(4.3, 27.05) * mm, "end": v(-2.7, 27.05) * mm});
            skLineSegment(sketch, "E55.9.0.3", {"start": v(-2.7, 27.05) * mm, "end": v(-2.7, 34.05) * mm});
            skLineSegment(sketch, "E55.9.1.0", {"start": v(4.3, 20.05) * mm, "end": v(4.3, 27.05) * mm});
            skLineSegment(sketch, "E55.9.1.1", {"start": v(4.3, 27.05) * mm, "end": v(-2.7, 27.05) * mm});
            skLineSegment(sketch, "E55.9.1.2", {"start": v(4.3, 20.05) * mm, "end": v(-2.7, 20.05) * mm});
            skLineSegment(sketch, "E55.9.1.3", {"start": v(-2.7, 20.05) * mm, "end": v(-2.7, 27.05) * mm});
            skLineSegment(sketch, "E55.9.2.0", {"start": v(4.3, 13.05) * mm, "end": v(4.3, 20.05) * mm});
            skLineSegment(sketch, "E55.9.2.1", {"start": v(4.3, 20.05) * mm, "end": v(-2.7, 20.05) * mm});
            skLineSegment(sketch, "E55.9.2.2", {"start": v(4.3, 13.05) * mm, "end": v(-2.7, 13.05) * mm});
            skLineSegment(sketch, "E55.9.2.3", {"start": v(-2.7, 13.05) * mm, "end": v(-2.7, 20.05) * mm});
            skLineSegment(sketch, "E55.9.3.0", {"start": v(4.3, 6.05) * mm, "end": v(4.3, 13.05) * mm});
            skLineSegment(sketch, "E55.9.3.1", {"start": v(4.3, 13.05) * mm, "end": v(-2.7, 13.05) * mm});
            skLineSegment(sketch, "E55.9.3.2", {"start": v(4.3, 6.05) * mm, "end": v(-2.7, 6.05) * mm});
            skLineSegment(sketch, "E55.9.3.3", {"start": v(-2.7, 6.05) * mm, "end": v(-2.7, 13.05) * mm});
            skLineSegment(sketch, "E55.9.4.0", {"start": v(4.3, -0.95) * mm, "end": v(4.3, 6.05) * mm});
            skLineSegment(sketch, "E55.9.4.1", {"start": v(4.3, 6.05) * mm, "end": v(-2.7, 6.05) * mm});
            skLineSegment(sketch, "E55.9.4.2", {"start": v(4.3, -0.95) * mm, "end": v(-2.7, -0.95) * mm});
            skLineSegment(sketch, "E55.9.4.3", {"start": v(-2.7, -0.95) * mm, "end": v(-2.7, 6.05) * mm});
            skLineSegment(sketch, "E55.9.5.0", {"start": v(4.3, -7.95) * mm, "end": v(4.3, -0.95) * mm});
            skLineSegment(sketch, "E55.9.5.1", {"start": v(4.3, -0.95) * mm, "end": v(-2.7, -0.95) * mm});
            skLineSegment(sketch, "E55.9.5.2", {"start": v(4.3, -7.95) * mm, "end": v(-2.7, -7.95) * mm});
            skLineSegment(sketch, "E55.9.5.3", {"start": v(-2.7, -7.95) * mm, "end": v(-2.7, -0.95) * mm});
            skLineSegment(sketch, "E55.9.6.0", {"start": v(4.3, -14.95) * mm, "end": v(4.3, -7.95) * mm});
            skLineSegment(sketch, "E55.9.6.1", {"start": v(4.3, -7.95) * mm, "end": v(-2.7, -7.95) * mm});
            skLineSegment(sketch, "E55.9.6.2", {"start": v(4.3, -14.95) * mm, "end": v(-2.7, -14.95) * mm});
            skLineSegment(sketch, "E55.9.6.3", {"start": v(-2.7, -14.95) * mm, "end": v(-2.7, -7.95) * mm});
            skLineSegment(sketch, "E55.9.7.0", {"start": v(4.3, -21.95) * mm, "end": v(4.3, -14.95) * mm});
            skLineSegment(sketch, "E55.9.7.1", {"start": v(4.3, -14.95) * mm, "end": v(-2.7, -14.95) * mm});
            skLineSegment(sketch, "E55.9.7.2", {"start": v(4.3, -21.95) * mm, "end": v(-2.7, -21.95) * mm});
            skLineSegment(sketch, "E55.9.7.3", {"start": v(-2.7, -21.95) * mm, "end": v(-2.7, -14.95) * mm});
            skLineSegment(sketch, "E55.9.8.0", {"start": v(4.3, -28.95) * mm, "end": v(4.3, -21.95) * mm});
            skLineSegment(sketch, "E55.9.8.1", {"start": v(4.3, -21.95) * mm, "end": v(-2.7, -21.95) * mm});
            skLineSegment(sketch, "E55.9.8.2", {"start": v(4.3, -28.95) * mm, "end": v(-2.7, -28.95) * mm});
            skLineSegment(sketch, "E55.9.8.3", {"start": v(-2.7, -28.95) * mm, "end": v(-2.7, -21.95) * mm});
            skLineSegment(sketch, "E55.9.9.0", {"start": v(4.3, -35.95) * mm, "end": v(4.3, -28.95) * mm});
            skLineSegment(sketch, "E55.9.9.1", {"start": v(4.3, -28.95) * mm, "end": v(-2.7, -28.95) * mm});
            skLineSegment(sketch, "E55.9.9.2", {"start": v(4.3, -35.95) * mm, "end": v(-2.7, -35.95) * mm});
            skLineSegment(sketch, "E55.9.9.3", {"start": v(-2.7, -35.95) * mm, "end": v(-2.7, -28.95) * mm});
            skLineSegment(sketch, "E55.9.10.0", {"start": v(4.3, -42.95) * mm, "end": v(4.3, -35.95) * mm});
            skLineSegment(sketch, "E55.9.10.1", {"start": v(4.3, -35.95) * mm, "end": v(-2.7, -35.95) * mm});
            skLineSegment(sketch, "E55.9.10.2", {"start": v(4.3, -42.95) * mm, "end": v(-2.7, -42.95) * mm});
            skLineSegment(sketch, "E55.9.10.3", {"start": v(-2.7, -42.95) * mm, "end": v(-2.7, -35.95) * mm});
            skLineSegment(sketch, "E55.9.11.0", {"start": v(4.3, -49.95) * mm, "end": v(4.3, -42.95) * mm});
            skLineSegment(sketch, "E55.9.11.1", {"start": v(4.3, -42.95) * mm, "end": v(-2.7, -42.95) * mm});
            skLineSegment(sketch, "E55.9.11.2", {"start": v(4.3, -49.95) * mm, "end": v(-2.7, -49.95) * mm});
            skLineSegment(sketch, "E55.9.11.3", {"start": v(-2.7, -49.95) * mm, "end": v(-2.7, -42.95) * mm});
            skLineSegment(sketch, "E55.9.12.0", {"start": v(4.3, -56.95) * mm, "end": v(4.3, -49.95) * mm});
            skLineSegment(sketch, "E55.9.12.1", {"start": v(4.3, -49.95) * mm, "end": v(-2.7, -49.95) * mm});
            skLineSegment(sketch, "E55.9.12.2", {"start": v(4.3, -56.95) * mm, "end": v(-2.7, -56.95) * mm});
            skLineSegment(sketch, "E55.9.12.3", {"start": v(-2.7, -56.95) * mm, "end": v(-2.7, -49.95) * mm});
            skLineSegment(sketch, "E55.9.13.0", {"start": v(4.3, -63.95) * mm, "end": v(4.3, -56.95) * mm});
            skLineSegment(sketch, "E55.9.13.1", {"start": v(4.3, -56.95) * mm, "end": v(-2.7, -56.95) * mm});
            skLineSegment(sketch, "E55.9.13.2", {"start": v(4.3, -63.95) * mm, "end": v(-2.7, -63.95) * mm});
            skLineSegment(sketch, "E55.9.13.3", {"start": v(-2.7, -63.95) * mm, "end": v(-2.7, -56.95) * mm});
            skLineSegment(sketch, "E55.9.14.0", {"start": v(4.3, -70.95) * mm, "end": v(4.3, -63.95) * mm});
            skLineSegment(sketch, "E55.9.14.1", {"start": v(4.3, -63.95) * mm, "end": v(-2.7, -63.95) * mm});
            skLineSegment(sketch, "E55.9.14.2", {"start": v(4.3, -70.95) * mm, "end": v(-2.7, -70.95) * mm});
            skLineSegment(sketch, "E55.9.14.3", {"start": v(-2.7, -70.95) * mm, "end": v(-2.7, -63.95) * mm});
            skLineSegment(sketch, "E55.9.15.0", {"start": v(4.3, -77.95) * mm, "end": v(4.3, -70.95) * mm});
            skLineSegment(sketch, "E55.9.15.1", {"start": v(4.3, -70.95) * mm, "end": v(-2.7, -70.95) * mm});
            skLineSegment(sketch, "E55.9.15.2", {"start": v(4.3, -77.95) * mm, "end": v(-2.7, -77.95) * mm});
            skLineSegment(sketch, "E55.9.15.3", {"start": v(-2.7, -77.95) * mm, "end": v(-2.7, -70.95) * mm});
            skLineSegment(sketch, "E55.10.0.0", {"start": v(11.3, 27.05) * mm, "end": v(11.3, 34.05) * mm});
            skLineSegment(sketch, "E55.10.0.1", {"start": v(11.3, 34.05) * mm, "end": v(4.3, 34.05) * mm});
            skLineSegment(sketch, "E55.10.0.2", {"start": v(11.3, 27.05) * mm, "end": v(4.3, 27.05) * mm});
            skLineSegment(sketch, "E55.10.0.3", {"start": v(4.3, 27.05) * mm, "end": v(4.3, 34.05) * mm});
            skLineSegment(sketch, "E55.10.1.0", {"start": v(11.3, 20.05) * mm, "end": v(11.3, 27.05) * mm});
            skLineSegment(sketch, "E55.10.1.1", {"start": v(11.3, 27.05) * mm, "end": v(4.3, 27.05) * mm});
            skLineSegment(sketch, "E55.10.1.2", {"start": v(11.3, 20.05) * mm, "end": v(4.3, 20.05) * mm});
            skLineSegment(sketch, "E55.10.1.3", {"start": v(4.3, 20.05) * mm, "end": v(4.3, 27.05) * mm});
            skLineSegment(sketch, "E55.10.2.0", {"start": v(11.3, 13.05) * mm, "end": v(11.3, 20.05) * mm});
            skLineSegment(sketch, "E55.10.2.1", {"start": v(11.3, 20.05) * mm, "end": v(4.3, 20.05) * mm});
            skLineSegment(sketch, "E55.10.2.2", {"start": v(11.3, 13.05) * mm, "end": v(4.3, 13.05) * mm});
            skLineSegment(sketch, "E55.10.2.3", {"start": v(4.3, 13.05) * mm, "end": v(4.3, 20.05) * mm});
            skLineSegment(sketch, "E55.10.3.0", {"start": v(11.3, 6.05) * mm, "end": v(11.3, 13.05) * mm});
            skLineSegment(sketch, "E55.10.3.1", {"start": v(11.3, 13.05) * mm, "end": v(4.3, 13.05) * mm});
            skLineSegment(sketch, "E55.10.3.2", {"start": v(11.3, 6.05) * mm, "end": v(4.3, 6.05) * mm});
            skLineSegment(sketch, "E55.10.3.3", {"start": v(4.3, 6.05) * mm, "end": v(4.3, 13.05) * mm});
            skLineSegment(sketch, "E55.10.4.0", {"start": v(11.3, -0.95) * mm, "end": v(11.3, 6.05) * mm});
            skLineSegment(sketch, "E55.10.4.1", {"start": v(11.3, 6.05) * mm, "end": v(4.3, 6.05) * mm});
            skLineSegment(sketch, "E55.10.4.2", {"start": v(11.3, -0.95) * mm, "end": v(4.3, -0.95) * mm});
            skLineSegment(sketch, "E55.10.4.3", {"start": v(4.3, -0.95) * mm, "end": v(4.3, 6.05) * mm});
            skLineSegment(sketch, "E55.10.5.0", {"start": v(11.3, -7.95) * mm, "end": v(11.3, -0.95) * mm});
            skLineSegment(sketch, "E55.10.5.1", {"start": v(11.3, -0.95) * mm, "end": v(4.3, -0.95) * mm});
            skLineSegment(sketch, "E55.10.5.2", {"start": v(11.3, -7.95) * mm, "end": v(4.3, -7.95) * mm});
            skLineSegment(sketch, "E55.10.5.3", {"start": v(4.3, -7.95) * mm, "end": v(4.3, -0.95) * mm});
            skLineSegment(sketch, "E55.10.6.0", {"start": v(11.3, -14.95) * mm, "end": v(11.3, -7.95) * mm});
            skLineSegment(sketch, "E55.10.6.1", {"start": v(11.3, -7.95) * mm, "end": v(4.3, -7.95) * mm});
            skLineSegment(sketch, "E55.10.6.2", {"start": v(11.3, -14.95) * mm, "end": v(4.3, -14.95) * mm});
            skLineSegment(sketch, "E55.10.6.3", {"start": v(4.3, -14.95) * mm, "end": v(4.3, -7.95) * mm});
            skLineSegment(sketch, "E55.10.7.0", {"start": v(11.3, -21.95) * mm, "end": v(11.3, -14.95) * mm});
            skLineSegment(sketch, "E55.10.7.1", {"start": v(11.3, -14.95) * mm, "end": v(4.3, -14.95) * mm});
            skLineSegment(sketch, "E55.10.7.2", {"start": v(11.3, -21.95) * mm, "end": v(4.3, -21.95) * mm});
            skLineSegment(sketch, "E55.10.7.3", {"start": v(4.3, -21.95) * mm, "end": v(4.3, -14.95) * mm});
            skLineSegment(sketch, "E55.10.8.0", {"start": v(11.3, -28.95) * mm, "end": v(11.3, -21.95) * mm});
            skLineSegment(sketch, "E55.10.8.1", {"start": v(11.3, -21.95) * mm, "end": v(4.3, -21.95) * mm});
            skLineSegment(sketch, "E55.10.8.2", {"start": v(11.3, -28.95) * mm, "end": v(4.3, -28.95) * mm});
            skLineSegment(sketch, "E55.10.8.3", {"start": v(4.3, -28.95) * mm, "end": v(4.3, -21.95) * mm});
            skLineSegment(sketch, "E55.10.9.0", {"start": v(11.3, -35.95) * mm, "end": v(11.3, -28.95) * mm});
            skLineSegment(sketch, "E55.10.9.1", {"start": v(11.3, -28.95) * mm, "end": v(4.3, -28.95) * mm});
            skLineSegment(sketch, "E55.10.9.2", {"start": v(11.3, -35.95) * mm, "end": v(4.3, -35.95) * mm});
            skLineSegment(sketch, "E55.10.9.3", {"start": v(4.3, -35.95) * mm, "end": v(4.3, -28.95) * mm});
            skLineSegment(sketch, "E55.10.10.0", {"start": v(11.3, -42.95) * mm, "end": v(11.3, -35.95) * mm});
            skLineSegment(sketch, "E55.10.10.1", {"start": v(11.3, -35.95) * mm, "end": v(4.3, -35.95) * mm});
            skLineSegment(sketch, "E55.10.10.2", {"start": v(11.3, -42.95) * mm, "end": v(4.3, -42.95) * mm});
            skLineSegment(sketch, "E55.10.10.3", {"start": v(4.3, -42.95) * mm, "end": v(4.3, -35.95) * mm});
            skLineSegment(sketch, "E55.10.11.0", {"start": v(11.3, -49.95) * mm, "end": v(11.3, -42.95) * mm});
            skLineSegment(sketch, "E55.10.11.1", {"start": v(11.3, -42.95) * mm, "end": v(4.3, -42.95) * mm});
            skLineSegment(sketch, "E55.10.11.2", {"start": v(11.3, -49.95) * mm, "end": v(4.3, -49.95) * mm});
            skLineSegment(sketch, "E55.10.11.3", {"start": v(4.3, -49.95) * mm, "end": v(4.3, -42.95) * mm});
            skLineSegment(sketch, "E55.10.12.0", {"start": v(11.3, -56.95) * mm, "end": v(11.3, -49.95) * mm});
            skLineSegment(sketch, "E55.10.12.1", {"start": v(11.3, -49.95) * mm, "end": v(4.3, -49.95) * mm});
            skLineSegment(sketch, "E55.10.12.2", {"start": v(11.3, -56.95) * mm, "end": v(4.3, -56.95) * mm});
            skLineSegment(sketch, "E55.10.12.3", {"start": v(4.3, -56.95) * mm, "end": v(4.3, -49.95) * mm});
            skLineSegment(sketch, "E55.10.13.0", {"start": v(11.3, -63.95) * mm, "end": v(11.3, -56.95) * mm});
            skLineSegment(sketch, "E55.10.13.1", {"start": v(11.3, -56.95) * mm, "end": v(4.3, -56.95) * mm});
            skLineSegment(sketch, "E55.10.13.2", {"start": v(11.3, -63.95) * mm, "end": v(4.3, -63.95) * mm});
            skLineSegment(sketch, "E55.10.13.3", {"start": v(4.3, -63.95) * mm, "end": v(4.3, -56.95) * mm});
            skLineSegment(sketch, "E55.10.14.0", {"start": v(11.3, -70.95) * mm, "end": v(11.3, -63.95) * mm});
            skLineSegment(sketch, "E55.10.14.1", {"start": v(11.3, -63.95) * mm, "end": v(4.3, -63.95) * mm});
            skLineSegment(sketch, "E55.10.14.2", {"start": v(11.3, -70.95) * mm, "end": v(4.3, -70.95) * mm});
            skLineSegment(sketch, "E55.10.14.3", {"start": v(4.3, -70.95) * mm, "end": v(4.3, -63.95) * mm});
            skLineSegment(sketch, "E55.10.15.0", {"start": v(11.3, -77.95) * mm, "end": v(11.3, -70.95) * mm});
            skLineSegment(sketch, "E55.10.15.1", {"start": v(11.3, -70.95) * mm, "end": v(4.3, -70.95) * mm});
            skLineSegment(sketch, "E55.10.15.2", {"start": v(11.3, -77.95) * mm, "end": v(4.3, -77.95) * mm});
            skLineSegment(sketch, "E55.10.15.3", {"start": v(4.3, -77.95) * mm, "end": v(4.3, -70.95) * mm});
            skLineSegment(sketch, "E55.11.0.0", {"start": v(18.3, 27.05) * mm, "end": v(18.3, 34.05) * mm});
            skLineSegment(sketch, "E55.11.0.1", {"start": v(18.3, 34.05) * mm, "end": v(11.3, 34.05) * mm});
            skLineSegment(sketch, "E55.11.0.2", {"start": v(18.3, 27.05) * mm, "end": v(11.3, 27.05) * mm});
            skLineSegment(sketch, "E55.11.0.3", {"start": v(11.3, 27.05) * mm, "end": v(11.3, 34.05) * mm});
            skLineSegment(sketch, "E55.11.1.0", {"start": v(18.3, 20.05) * mm, "end": v(18.3, 27.05) * mm});
            skLineSegment(sketch, "E55.11.1.1", {"start": v(18.3, 27.05) * mm, "end": v(11.3, 27.05) * mm});
            skLineSegment(sketch, "E55.11.1.2", {"start": v(18.3, 20.05) * mm, "end": v(11.3, 20.05) * mm});
            skLineSegment(sketch, "E55.11.1.3", {"start": v(11.3, 20.05) * mm, "end": v(11.3, 27.05) * mm});
            skLineSegment(sketch, "E55.11.2.0", {"start": v(18.3, 13.05) * mm, "end": v(18.3, 20.05) * mm});
            skLineSegment(sketch, "E55.11.2.1", {"start": v(18.3, 20.05) * mm, "end": v(11.3, 20.05) * mm});
            skLineSegment(sketch, "E55.11.2.2", {"start": v(18.3, 13.05) * mm, "end": v(11.3, 13.05) * mm});
            skLineSegment(sketch, "E55.11.2.3", {"start": v(11.3, 13.05) * mm, "end": v(11.3, 20.05) * mm});
            skLineSegment(sketch, "E55.11.3.0", {"start": v(18.3, 6.05) * mm, "end": v(18.3, 13.05) * mm});
            skLineSegment(sketch, "E55.11.3.1", {"start": v(18.3, 13.05) * mm, "end": v(11.3, 13.05) * mm});
            skLineSegment(sketch, "E55.11.3.2", {"start": v(18.3, 6.05) * mm, "end": v(11.3, 6.05) * mm});
            skLineSegment(sketch, "E55.11.3.3", {"start": v(11.3, 6.05) * mm, "end": v(11.3, 13.05) * mm});
            skLineSegment(sketch, "E55.11.4.0", {"start": v(18.3, -0.95) * mm, "end": v(18.3, 6.05) * mm});
            skLineSegment(sketch, "E55.11.4.1", {"start": v(18.3, 6.05) * mm, "end": v(11.3, 6.05) * mm});
            skLineSegment(sketch, "E55.11.4.2", {"start": v(18.3, -0.95) * mm, "end": v(11.3, -0.95) * mm});
            skLineSegment(sketch, "E55.11.4.3", {"start": v(11.3, -0.95) * mm, "end": v(11.3, 6.05) * mm});
            skLineSegment(sketch, "E55.11.5.0", {"start": v(18.3, -7.95) * mm, "end": v(18.3, -0.95) * mm});
            skLineSegment(sketch, "E55.11.5.1", {"start": v(18.3, -0.95) * mm, "end": v(11.3, -0.95) * mm});
            skLineSegment(sketch, "E55.11.5.2", {"start": v(18.3, -7.95) * mm, "end": v(11.3, -7.95) * mm});
            skLineSegment(sketch, "E55.11.5.3", {"start": v(11.3, -7.95) * mm, "end": v(11.3, -0.95) * mm});
            skLineSegment(sketch, "E55.11.6.0", {"start": v(18.3, -14.95) * mm, "end": v(18.3, -7.95) * mm});
            skLineSegment(sketch, "E55.11.6.1", {"start": v(18.3, -7.95) * mm, "end": v(11.3, -7.95) * mm});
            skLineSegment(sketch, "E55.11.6.2", {"start": v(18.3, -14.95) * mm, "end": v(11.3, -14.95) * mm});
            skLineSegment(sketch, "E55.11.6.3", {"start": v(11.3, -14.95) * mm, "end": v(11.3, -7.95) * mm});
            skLineSegment(sketch, "E55.11.7.0", {"start": v(18.3, -21.95) * mm, "end": v(18.3, -14.95) * mm});
            skLineSegment(sketch, "E55.11.7.1", {"start": v(18.3, -14.95) * mm, "end": v(11.3, -14.95) * mm});
            skLineSegment(sketch, "E55.11.7.2", {"start": v(18.3, -21.95) * mm, "end": v(11.3, -21.95) * mm});
            skLineSegment(sketch, "E55.11.7.3", {"start": v(11.3, -21.95) * mm, "end": v(11.3, -14.95) * mm});
            skLineSegment(sketch, "E55.11.8.0", {"start": v(18.3, -28.95) * mm, "end": v(18.3, -21.95) * mm});
            skLineSegment(sketch, "E55.11.8.1", {"start": v(18.3, -21.95) * mm, "end": v(11.3, -21.95) * mm});
            skLineSegment(sketch, "E55.11.8.2", {"start": v(18.3, -28.95) * mm, "end": v(11.3, -28.95) * mm});
            skLineSegment(sketch, "E55.11.8.3", {"start": v(11.3, -28.95) * mm, "end": v(11.3, -21.95) * mm});
            skLineSegment(sketch, "E55.11.9.0", {"start": v(18.3, -35.95) * mm, "end": v(18.3, -28.95) * mm});
            skLineSegment(sketch, "E55.11.9.1", {"start": v(18.3, -28.95) * mm, "end": v(11.3, -28.95) * mm});
            skLineSegment(sketch, "E55.11.9.2", {"start": v(18.3, -35.95) * mm, "end": v(11.3, -35.95) * mm});
            skLineSegment(sketch, "E55.11.9.3", {"start": v(11.3, -35.95) * mm, "end": v(11.3, -28.95) * mm});
            skLineSegment(sketch, "E55.11.10.0", {"start": v(18.3, -42.95) * mm, "end": v(18.3, -35.95) * mm});
            skLineSegment(sketch, "E55.11.10.1", {"start": v(18.3, -35.95) * mm, "end": v(11.3, -35.95) * mm});
            skLineSegment(sketch, "E55.11.10.2", {"start": v(18.3, -42.95) * mm, "end": v(11.3, -42.95) * mm});
            skLineSegment(sketch, "E55.11.10.3", {"start": v(11.3, -42.95) * mm, "end": v(11.3, -35.95) * mm});
            skLineSegment(sketch, "E55.11.11.0", {"start": v(18.3, -49.95) * mm, "end": v(18.3, -42.95) * mm});
            skLineSegment(sketch, "E55.11.11.1", {"start": v(18.3, -42.95) * mm, "end": v(11.3, -42.95) * mm});
            skLineSegment(sketch, "E55.11.11.2", {"start": v(18.3, -49.95) * mm, "end": v(11.3, -49.95) * mm});
            skLineSegment(sketch, "E55.11.11.3", {"start": v(11.3, -49.95) * mm, "end": v(11.3, -42.95) * mm});
            skLineSegment(sketch, "E55.11.12.0", {"start": v(18.3, -56.95) * mm, "end": v(18.3, -49.95) * mm});
            skLineSegment(sketch, "E55.11.12.1", {"start": v(18.3, -49.95) * mm, "end": v(11.3, -49.95) * mm});
            skLineSegment(sketch, "E55.11.12.2", {"start": v(18.3, -56.95) * mm, "end": v(11.3, -56.95) * mm});
            skLineSegment(sketch, "E55.11.12.3", {"start": v(11.3, -56.95) * mm, "end": v(11.3, -49.95) * mm});
            skLineSegment(sketch, "E55.11.13.0", {"start": v(18.3, -63.95) * mm, "end": v(18.3, -56.95) * mm});
            skLineSegment(sketch, "E55.11.13.1", {"start": v(18.3, -56.95) * mm, "end": v(11.3, -56.95) * mm});
            skLineSegment(sketch, "E55.11.13.2", {"start": v(18.3, -63.95) * mm, "end": v(11.3, -63.95) * mm});
            skLineSegment(sketch, "E55.11.13.3", {"start": v(11.3, -63.95) * mm, "end": v(11.3, -56.95) * mm});
            skLineSegment(sketch, "E55.11.14.0", {"start": v(18.3, -70.95) * mm, "end": v(18.3, -63.95) * mm});
            skLineSegment(sketch, "E55.11.14.1", {"start": v(18.3, -63.95) * mm, "end": v(11.3, -63.95) * mm});
            skLineSegment(sketch, "E55.11.14.2", {"start": v(18.3, -70.95) * mm, "end": v(11.3, -70.95) * mm});
            skLineSegment(sketch, "E55.11.14.3", {"start": v(11.3, -70.95) * mm, "end": v(11.3, -63.95) * mm});
            skLineSegment(sketch, "E55.11.15.0", {"start": v(18.3, -77.95) * mm, "end": v(18.3, -70.95) * mm});
            skLineSegment(sketch, "E55.11.15.1", {"start": v(18.3, -70.95) * mm, "end": v(11.3, -70.95) * mm});
            skLineSegment(sketch, "E55.11.15.2", {"start": v(18.3, -77.95) * mm, "end": v(11.3, -77.95) * mm});
            skLineSegment(sketch, "E55.11.15.3", {"start": v(11.3, -77.95) * mm, "end": v(11.3, -70.95) * mm});
            skLineSegment(sketch, "E55.12.0.0", {"start": v(25.3, 27.05) * mm, "end": v(25.3, 34.05) * mm});
            skLineSegment(sketch, "E55.12.0.1", {"start": v(25.3, 34.05) * mm, "end": v(18.3, 34.05) * mm});
            skLineSegment(sketch, "E55.12.0.2", {"start": v(25.3, 27.05) * mm, "end": v(18.3, 27.05) * mm});
            skLineSegment(sketch, "E55.12.0.3", {"start": v(18.3, 27.05) * mm, "end": v(18.3, 34.05) * mm});
            skLineSegment(sketch, "E55.12.1.0", {"start": v(25.3, 20.05) * mm, "end": v(25.3, 27.05) * mm});
            skLineSegment(sketch, "E55.12.1.1", {"start": v(25.3, 27.05) * mm, "end": v(18.3, 27.05) * mm});
            skLineSegment(sketch, "E55.12.1.2", {"start": v(25.3, 20.05) * mm, "end": v(18.3, 20.05) * mm});
            skLineSegment(sketch, "E55.12.1.3", {"start": v(18.3, 20.05) * mm, "end": v(18.3, 27.05) * mm});
            skLineSegment(sketch, "E55.12.2.0", {"start": v(25.3, 13.05) * mm, "end": v(25.3, 20.05) * mm});
            skLineSegment(sketch, "E55.12.2.1", {"start": v(25.3, 20.05) * mm, "end": v(18.3, 20.05) * mm});
            skLineSegment(sketch, "E55.12.2.2", {"start": v(25.3, 13.05) * mm, "end": v(18.3, 13.05) * mm});
            skLineSegment(sketch, "E55.12.2.3", {"start": v(18.3, 13.05) * mm, "end": v(18.3, 20.05) * mm});
            skLineSegment(sketch, "E55.12.3.0", {"start": v(25.3, 6.05) * mm, "end": v(25.3, 13.05) * mm});
            skLineSegment(sketch, "E55.12.3.1", {"start": v(25.3, 13.05) * mm, "end": v(18.3, 13.05) * mm});
            skLineSegment(sketch, "E55.12.3.2", {"start": v(25.3, 6.05) * mm, "end": v(18.3, 6.05) * mm});
            skLineSegment(sketch, "E55.12.3.3", {"start": v(18.3, 6.05) * mm, "end": v(18.3, 13.05) * mm});
            skLineSegment(sketch, "E55.12.4.0", {"start": v(25.3, -0.95) * mm, "end": v(25.3, 6.05) * mm});
            skLineSegment(sketch, "E55.12.4.1", {"start": v(25.3, 6.05) * mm, "end": v(18.3, 6.05) * mm});
            skLineSegment(sketch, "E55.12.4.2", {"start": v(25.3, -0.95) * mm, "end": v(18.3, -0.95) * mm});
            skLineSegment(sketch, "E55.12.4.3", {"start": v(18.3, -0.95) * mm, "end": v(18.3, 6.05) * mm});
            skLineSegment(sketch, "E55.12.5.0", {"start": v(25.3, -7.95) * mm, "end": v(25.3, -0.95) * mm});
            skLineSegment(sketch, "E55.12.5.1", {"start": v(25.3, -0.95) * mm, "end": v(18.3, -0.95) * mm});
            skLineSegment(sketch, "E55.12.5.2", {"start": v(25.3, -7.95) * mm, "end": v(18.3, -7.95) * mm});
            skLineSegment(sketch, "E55.12.5.3", {"start": v(18.3, -7.95) * mm, "end": v(18.3, -0.95) * mm});
            skLineSegment(sketch, "E55.12.6.0", {"start": v(25.3, -14.95) * mm, "end": v(25.3, -7.95) * mm});
            skLineSegment(sketch, "E55.12.6.1", {"start": v(25.3, -7.95) * mm, "end": v(18.3, -7.95) * mm});
            skLineSegment(sketch, "E55.12.6.2", {"start": v(25.3, -14.95) * mm, "end": v(18.3, -14.95) * mm});
            skLineSegment(sketch, "E55.12.6.3", {"start": v(18.3, -14.95) * mm, "end": v(18.3, -7.95) * mm});
            skLineSegment(sketch, "E55.12.7.0", {"start": v(25.3, -21.95) * mm, "end": v(25.3, -14.95) * mm});
            skLineSegment(sketch, "E55.12.7.1", {"start": v(25.3, -14.95) * mm, "end": v(18.3, -14.95) * mm});
            skLineSegment(sketch, "E55.12.7.2", {"start": v(25.3, -21.95) * mm, "end": v(18.3, -21.95) * mm});
            skLineSegment(sketch, "E55.12.7.3", {"start": v(18.3, -21.95) * mm, "end": v(18.3, -14.95) * mm});
            skLineSegment(sketch, "E55.12.8.0", {"start": v(25.3, -28.95) * mm, "end": v(25.3, -21.95) * mm});
            skLineSegment(sketch, "E55.12.8.1", {"start": v(25.3, -21.95) * mm, "end": v(18.3, -21.95) * mm});
            skLineSegment(sketch, "E55.12.8.2", {"start": v(25.3, -28.95) * mm, "end": v(18.3, -28.95) * mm});
            skLineSegment(sketch, "E55.12.8.3", {"start": v(18.3, -28.95) * mm, "end": v(18.3, -21.95) * mm});
            skLineSegment(sketch, "E55.12.9.0", {"start": v(25.3, -35.95) * mm, "end": v(25.3, -28.95) * mm});
            skLineSegment(sketch, "E55.12.9.1", {"start": v(25.3, -28.95) * mm, "end": v(18.3, -28.95) * mm});
            skLineSegment(sketch, "E55.12.9.2", {"start": v(25.3, -35.95) * mm, "end": v(18.3, -35.95) * mm});
            skLineSegment(sketch, "E55.12.9.3", {"start": v(18.3, -35.95) * mm, "end": v(18.3, -28.95) * mm});
            skLineSegment(sketch, "E55.12.10.0", {"start": v(25.3, -42.95) * mm, "end": v(25.3, -35.95) * mm});
            skLineSegment(sketch, "E55.12.10.1", {"start": v(25.3, -35.95) * mm, "end": v(18.3, -35.95) * mm});
            skLineSegment(sketch, "E55.12.10.2", {"start": v(25.3, -42.95) * mm, "end": v(18.3, -42.95) * mm});
            skLineSegment(sketch, "E55.12.10.3", {"start": v(18.3, -42.95) * mm, "end": v(18.3, -35.95) * mm});
            skLineSegment(sketch, "E55.12.11.0", {"start": v(25.3, -49.95) * mm, "end": v(25.3, -42.95) * mm});
            skLineSegment(sketch, "E55.12.11.1", {"start": v(25.3, -42.95) * mm, "end": v(18.3, -42.95) * mm});
            skLineSegment(sketch, "E55.12.11.2", {"start": v(25.3, -49.95) * mm, "end": v(18.3, -49.95) * mm});
            skLineSegment(sketch, "E55.12.11.3", {"start": v(18.3, -49.95) * mm, "end": v(18.3, -42.95) * mm});
            skLineSegment(sketch, "E55.12.12.0", {"start": v(25.3, -56.95) * mm, "end": v(25.3, -49.95) * mm});
            skLineSegment(sketch, "E55.12.12.1", {"start": v(25.3, -49.95) * mm, "end": v(18.3, -49.95) * mm});
            skLineSegment(sketch, "E55.12.12.2", {"start": v(25.3, -56.95) * mm, "end": v(18.3, -56.95) * mm});
            skLineSegment(sketch, "E55.12.12.3", {"start": v(18.3, -56.95) * mm, "end": v(18.3, -49.95) * mm});
            skLineSegment(sketch, "E55.12.13.0", {"start": v(25.3, -63.95) * mm, "end": v(25.3, -56.95) * mm});
            skLineSegment(sketch, "E55.12.13.1", {"start": v(25.3, -56.95) * mm, "end": v(18.3, -56.95) * mm});
            skLineSegment(sketch, "E55.12.13.2", {"start": v(25.3, -63.95) * mm, "end": v(18.3, -63.95) * mm});
            skLineSegment(sketch, "E55.12.13.3", {"start": v(18.3, -63.95) * mm, "end": v(18.3, -56.95) * mm});
            skLineSegment(sketch, "E55.12.14.0", {"start": v(25.3, -70.95) * mm, "end": v(25.3, -63.95) * mm});
            skLineSegment(sketch, "E55.12.14.1", {"start": v(25.3, -63.95) * mm, "end": v(18.3, -63.95) * mm});
            skLineSegment(sketch, "E55.12.14.2", {"start": v(25.3, -70.95) * mm, "end": v(18.3, -70.95) * mm});
            skLineSegment(sketch, "E55.12.14.3", {"start": v(18.3, -70.95) * mm, "end": v(18.3, -63.95) * mm});
            skLineSegment(sketch, "E55.12.15.0", {"start": v(25.3, -77.95) * mm, "end": v(25.3, -70.95) * mm});
            skLineSegment(sketch, "E55.12.15.1", {"start": v(25.3, -70.95) * mm, "end": v(18.3, -70.95) * mm});
            skLineSegment(sketch, "E55.12.15.2", {"start": v(25.3, -77.95) * mm, "end": v(18.3, -77.95) * mm});
            skLineSegment(sketch, "E55.12.15.3", {"start": v(18.3, -77.95) * mm, "end": v(18.3, -70.95) * mm});
            skLineSegment(sketch, "E55.13.0.0", {"start": v(32.3, 27.05) * mm, "end": v(32.3, 34.05) * mm});
            skLineSegment(sketch, "E55.13.0.1", {"start": v(32.3, 34.05) * mm, "end": v(25.3, 34.05) * mm});
            skLineSegment(sketch, "E55.13.0.2", {"start": v(32.3, 27.05) * mm, "end": v(25.3, 27.05) * mm});
            skLineSegment(sketch, "E55.13.0.3", {"start": v(25.3, 27.05) * mm, "end": v(25.3, 34.05) * mm});
            skLineSegment(sketch, "E55.13.1.0", {"start": v(32.3, 20.05) * mm, "end": v(32.3, 27.05) * mm});
            skLineSegment(sketch, "E55.13.1.1", {"start": v(32.3, 27.05) * mm, "end": v(25.3, 27.05) * mm});
            skLineSegment(sketch, "E55.13.1.2", {"start": v(32.3, 20.05) * mm, "end": v(25.3, 20.05) * mm});
            skLineSegment(sketch, "E55.13.1.3", {"start": v(25.3, 20.05) * mm, "end": v(25.3, 27.05) * mm});
            skLineSegment(sketch, "E55.13.2.0", {"start": v(32.3, 13.05) * mm, "end": v(32.3, 20.05) * mm});
            skLineSegment(sketch, "E55.13.2.1", {"start": v(32.3, 20.05) * mm, "end": v(25.3, 20.05) * mm});
            skLineSegment(sketch, "E55.13.2.2", {"start": v(32.3, 13.05) * mm, "end": v(25.3, 13.05) * mm});
            skLineSegment(sketch, "E55.13.2.3", {"start": v(25.3, 13.05) * mm, "end": v(25.3, 20.05) * mm});
            skLineSegment(sketch, "E55.13.3.0", {"start": v(32.3, 6.05) * mm, "end": v(32.3, 13.05) * mm});
            skLineSegment(sketch, "E55.13.3.1", {"start": v(32.3, 13.05) * mm, "end": v(25.3, 13.05) * mm});
            skLineSegment(sketch, "E55.13.3.2", {"start": v(32.3, 6.05) * mm, "end": v(25.3, 6.05) * mm});
            skLineSegment(sketch, "E55.13.3.3", {"start": v(25.3, 6.05) * mm, "end": v(25.3, 13.05) * mm});
            skLineSegment(sketch, "E55.13.4.0", {"start": v(32.3, -0.95) * mm, "end": v(32.3, 6.05) * mm});
            skLineSegment(sketch, "E55.13.4.1", {"start": v(32.3, 6.05) * mm, "end": v(25.3, 6.05) * mm});
            skLineSegment(sketch, "E55.13.4.2", {"start": v(32.3, -0.95) * mm, "end": v(25.3, -0.95) * mm});
            skLineSegment(sketch, "E55.13.4.3", {"start": v(25.3, -0.95) * mm, "end": v(25.3, 6.05) * mm});
            skLineSegment(sketch, "E55.13.5.0", {"start": v(32.3, -7.95) * mm, "end": v(32.3, -0.95) * mm});
            skLineSegment(sketch, "E55.13.5.1", {"start": v(32.3, -0.95) * mm, "end": v(25.3, -0.95) * mm});
            skLineSegment(sketch, "E55.13.5.2", {"start": v(32.3, -7.95) * mm, "end": v(25.3, -7.95) * mm});
            skLineSegment(sketch, "E55.13.5.3", {"start": v(25.3, -7.95) * mm, "end": v(25.3, -0.95) * mm});
            skLineSegment(sketch, "E55.13.6.0", {"start": v(32.3, -14.95) * mm, "end": v(32.3, -7.95) * mm});
            skLineSegment(sketch, "E55.13.6.1", {"start": v(32.3, -7.95) * mm, "end": v(25.3, -7.95) * mm});
            skLineSegment(sketch, "E55.13.6.2", {"start": v(32.3, -14.95) * mm, "end": v(25.3, -14.95) * mm});
            skLineSegment(sketch, "E55.13.6.3", {"start": v(25.3, -14.95) * mm, "end": v(25.3, -7.95) * mm});
            skLineSegment(sketch, "E55.13.7.0", {"start": v(32.3, -21.95) * mm, "end": v(32.3, -14.95) * mm});
            skLineSegment(sketch, "E55.13.7.1", {"start": v(32.3, -14.95) * mm, "end": v(25.3, -14.95) * mm});
            skLineSegment(sketch, "E55.13.7.2", {"start": v(32.3, -21.95) * mm, "end": v(25.3, -21.95) * mm});
            skLineSegment(sketch, "E55.13.7.3", {"start": v(25.3, -21.95) * mm, "end": v(25.3, -14.95) * mm});
            skLineSegment(sketch, "E55.13.8.0", {"start": v(32.3, -28.95) * mm, "end": v(32.3, -21.95) * mm});
            skLineSegment(sketch, "E55.13.8.1", {"start": v(32.3, -21.95) * mm, "end": v(25.3, -21.95) * mm});
            skLineSegment(sketch, "E55.13.8.2", {"start": v(32.3, -28.95) * mm, "end": v(25.3, -28.95) * mm});
            skLineSegment(sketch, "E55.13.8.3", {"start": v(25.3, -28.95) * mm, "end": v(25.3, -21.95) * mm});
            skLineSegment(sketch, "E55.13.9.0", {"start": v(32.3, -35.95) * mm, "end": v(32.3, -28.95) * mm});
            skLineSegment(sketch, "E55.13.9.1", {"start": v(32.3, -28.95) * mm, "end": v(25.3, -28.95) * mm});
            skLineSegment(sketch, "E55.13.9.2", {"start": v(32.3, -35.95) * mm, "end": v(25.3, -35.95) * mm});
            skLineSegment(sketch, "E55.13.9.3", {"start": v(25.3, -35.95) * mm, "end": v(25.3, -28.95) * mm});
            skLineSegment(sketch, "E55.13.10.0", {"start": v(32.3, -42.95) * mm, "end": v(32.3, -35.95) * mm});
            skLineSegment(sketch, "E55.13.10.1", {"start": v(32.3, -35.95) * mm, "end": v(25.3, -35.95) * mm});
            skLineSegment(sketch, "E55.13.10.2", {"start": v(32.3, -42.95) * mm, "end": v(25.3, -42.95) * mm});
            skLineSegment(sketch, "E55.13.10.3", {"start": v(25.3, -42.95) * mm, "end": v(25.3, -35.95) * mm});
            skLineSegment(sketch, "E55.13.11.0", {"start": v(32.3, -49.95) * mm, "end": v(32.3, -42.95) * mm});
            skLineSegment(sketch, "E55.13.11.1", {"start": v(32.3, -42.95) * mm, "end": v(25.3, -42.95) * mm});
            skLineSegment(sketch, "E55.13.11.2", {"start": v(32.3, -49.95) * mm, "end": v(25.3, -49.95) * mm});
            skLineSegment(sketch, "E55.13.11.3", {"start": v(25.3, -49.95) * mm, "end": v(25.3, -42.95) * mm});
            skLineSegment(sketch, "E55.13.12.0", {"start": v(32.3, -56.95) * mm, "end": v(32.3, -49.95) * mm});
            skLineSegment(sketch, "E55.13.12.1", {"start": v(32.3, -49.95) * mm, "end": v(25.3, -49.95) * mm});
            skLineSegment(sketch, "E55.13.12.2", {"start": v(32.3, -56.95) * mm, "end": v(25.3, -56.95) * mm});
            skLineSegment(sketch, "E55.13.12.3", {"start": v(25.3, -56.95) * mm, "end": v(25.3, -49.95) * mm});
            skLineSegment(sketch, "E55.13.13.0", {"start": v(32.3, -63.95) * mm, "end": v(32.3, -56.95) * mm});
            skLineSegment(sketch, "E55.13.13.1", {"start": v(32.3, -56.95) * mm, "end": v(25.3, -56.95) * mm});
            skLineSegment(sketch, "E55.13.13.2", {"start": v(32.3, -63.95) * mm, "end": v(25.3, -63.95) * mm});
            skLineSegment(sketch, "E55.13.13.3", {"start": v(25.3, -63.95) * mm, "end": v(25.3, -56.95) * mm});
            skLineSegment(sketch, "E55.13.14.0", {"start": v(32.3, -70.95) * mm, "end": v(32.3, -63.95) * mm});
            skLineSegment(sketch, "E55.13.14.1", {"start": v(32.3, -63.95) * mm, "end": v(25.3, -63.95) * mm});
            skLineSegment(sketch, "E55.13.14.2", {"start": v(32.3, -70.95) * mm, "end": v(25.3, -70.95) * mm});
            skLineSegment(sketch, "E55.13.14.3", {"start": v(25.3, -70.95) * mm, "end": v(25.3, -63.95) * mm});
            skLineSegment(sketch, "E55.13.15.0", {"start": v(32.3, -77.95) * mm, "end": v(32.3, -70.95) * mm});
            skLineSegment(sketch, "E55.13.15.1", {"start": v(32.3, -70.95) * mm, "end": v(25.3, -70.95) * mm});
            skLineSegment(sketch, "E55.13.15.2", {"start": v(32.3, -77.95) * mm, "end": v(25.3, -77.95) * mm});
            skLineSegment(sketch, "E55.13.15.3", {"start": v(25.3, -77.95) * mm, "end": v(25.3, -70.95) * mm});
            skLineSegment(sketch, "E55.14.0.0", {"start": v(39.3, 27.05) * mm, "end": v(39.3, 34.05) * mm});
            skLineSegment(sketch, "E55.14.0.1", {"start": v(39.3, 34.05) * mm, "end": v(32.3, 34.05) * mm});
            skLineSegment(sketch, "E55.14.0.2", {"start": v(39.3, 27.05) * mm, "end": v(32.3, 27.05) * mm});
            skLineSegment(sketch, "E55.14.0.3", {"start": v(32.3, 27.05) * mm, "end": v(32.3, 34.05) * mm});
            skLineSegment(sketch, "E55.14.1.0", {"start": v(39.3, 20.05) * mm, "end": v(39.3, 27.05) * mm});
            skLineSegment(sketch, "E55.14.1.1", {"start": v(39.3, 27.05) * mm, "end": v(32.3, 27.05) * mm});
            skLineSegment(sketch, "E55.14.1.2", {"start": v(39.3, 20.05) * mm, "end": v(32.3, 20.05) * mm});
            skLineSegment(sketch, "E55.14.1.3", {"start": v(32.3, 20.05) * mm, "end": v(32.3, 27.05) * mm});
            skLineSegment(sketch, "E55.14.2.0", {"start": v(39.3, 13.05) * mm, "end": v(39.3, 20.05) * mm});
            skLineSegment(sketch, "E55.14.2.1", {"start": v(39.3, 20.05) * mm, "end": v(32.3, 20.05) * mm});
            skLineSegment(sketch, "E55.14.2.2", {"start": v(39.3, 13.05) * mm, "end": v(32.3, 13.05) * mm});
            skLineSegment(sketch, "E55.14.2.3", {"start": v(32.3, 13.05) * mm, "end": v(32.3, 20.05) * mm});
            skLineSegment(sketch, "E55.14.3.0", {"start": v(39.3, 6.05) * mm, "end": v(39.3, 13.05) * mm});
            skLineSegment(sketch, "E55.14.3.1", {"start": v(39.3, 13.05) * mm, "end": v(32.3, 13.05) * mm});
            skLineSegment(sketch, "E55.14.3.2", {"start": v(39.3, 6.05) * mm, "end": v(32.3, 6.05) * mm});
            skLineSegment(sketch, "E55.14.3.3", {"start": v(32.3, 6.05) * mm, "end": v(32.3, 13.05) * mm});
            skLineSegment(sketch, "E55.14.4.0", {"start": v(39.3, -0.95) * mm, "end": v(39.3, 6.05) * mm});
            skLineSegment(sketch, "E55.14.4.1", {"start": v(39.3, 6.05) * mm, "end": v(32.3, 6.05) * mm});
            skLineSegment(sketch, "E55.14.4.2", {"start": v(39.3, -0.95) * mm, "end": v(32.3, -0.95) * mm});
            skLineSegment(sketch, "E55.14.4.3", {"start": v(32.3, -0.95) * mm, "end": v(32.3, 6.05) * mm});
            skLineSegment(sketch, "E55.14.5.0", {"start": v(39.3, -7.95) * mm, "end": v(39.3, -0.95) * mm});
            skLineSegment(sketch, "E55.14.5.1", {"start": v(39.3, -0.95) * mm, "end": v(32.3, -0.95) * mm});
            skLineSegment(sketch, "E55.14.5.2", {"start": v(39.3, -7.95) * mm, "end": v(32.3, -7.95) * mm});
            skLineSegment(sketch, "E55.14.5.3", {"start": v(32.3, -7.95) * mm, "end": v(32.3, -0.95) * mm});
            skLineSegment(sketch, "E55.14.6.0", {"start": v(39.3, -14.95) * mm, "end": v(39.3, -7.95) * mm});
            skLineSegment(sketch, "E55.14.6.1", {"start": v(39.3, -7.95) * mm, "end": v(32.3, -7.95) * mm});
            skLineSegment(sketch, "E55.14.6.2", {"start": v(39.3, -14.95) * mm, "end": v(32.3, -14.95) * mm});
            skLineSegment(sketch, "E55.14.6.3", {"start": v(32.3, -14.95) * mm, "end": v(32.3, -7.95) * mm});
            skLineSegment(sketch, "E55.14.7.0", {"start": v(39.3, -21.95) * mm, "end": v(39.3, -14.95) * mm});
            skLineSegment(sketch, "E55.14.7.1", {"start": v(39.3, -14.95) * mm, "end": v(32.3, -14.95) * mm});
            skLineSegment(sketch, "E55.14.7.2", {"start": v(39.3, -21.95) * mm, "end": v(32.3, -21.95) * mm});
            skLineSegment(sketch, "E55.14.7.3", {"start": v(32.3, -21.95) * mm, "end": v(32.3, -14.95) * mm});
            skLineSegment(sketch, "E55.14.8.0", {"start": v(39.3, -28.95) * mm, "end": v(39.3, -21.95) * mm});
            skLineSegment(sketch, "E55.14.8.1", {"start": v(39.3, -21.95) * mm, "end": v(32.3, -21.95) * mm});
            skLineSegment(sketch, "E55.14.8.2", {"start": v(39.3, -28.95) * mm, "end": v(32.3, -28.95) * mm});
            skLineSegment(sketch, "E55.14.8.3", {"start": v(32.3, -28.95) * mm, "end": v(32.3, -21.95) * mm});
            skLineSegment(sketch, "E55.14.9.0", {"start": v(39.3, -35.95) * mm, "end": v(39.3, -28.95) * mm});
            skLineSegment(sketch, "E55.14.9.1", {"start": v(39.3, -28.95) * mm, "end": v(32.3, -28.95) * mm});
            skLineSegment(sketch, "E55.14.9.2", {"start": v(39.3, -35.95) * mm, "end": v(32.3, -35.95) * mm});
            skLineSegment(sketch, "E55.14.9.3", {"start": v(32.3, -35.95) * mm, "end": v(32.3, -28.95) * mm});
            skLineSegment(sketch, "E55.14.10.0", {"start": v(39.3, -42.95) * mm, "end": v(39.3, -35.95) * mm});
            skLineSegment(sketch, "E55.14.10.1", {"start": v(39.3, -35.95) * mm, "end": v(32.3, -35.95) * mm});
            skLineSegment(sketch, "E55.14.10.2", {"start": v(39.3, -42.95) * mm, "end": v(32.3, -42.95) * mm});
            skLineSegment(sketch, "E55.14.10.3", {"start": v(32.3, -42.95) * mm, "end": v(32.3, -35.95) * mm});
            skLineSegment(sketch, "E55.14.11.0", {"start": v(39.3, -49.95) * mm, "end": v(39.3, -42.95) * mm});
            skLineSegment(sketch, "E55.14.11.1", {"start": v(39.3, -42.95) * mm, "end": v(32.3, -42.95) * mm});
            skLineSegment(sketch, "E55.14.11.2", {"start": v(39.3, -49.95) * mm, "end": v(32.3, -49.95) * mm});
            skLineSegment(sketch, "E55.14.11.3", {"start": v(32.3, -49.95) * mm, "end": v(32.3, -42.95) * mm});
            skLineSegment(sketch, "E55.14.12.0", {"start": v(39.3, -56.95) * mm, "end": v(39.3, -49.95) * mm});
            skLineSegment(sketch, "E55.14.12.1", {"start": v(39.3, -49.95) * mm, "end": v(32.3, -49.95) * mm});
            skLineSegment(sketch, "E55.14.12.2", {"start": v(39.3, -56.95) * mm, "end": v(32.3, -56.95) * mm});
            skLineSegment(sketch, "E55.14.12.3", {"start": v(32.3, -56.95) * mm, "end": v(32.3, -49.95) * mm});
            skLineSegment(sketch, "E55.14.13.0", {"start": v(39.3, -63.95) * mm, "end": v(39.3, -56.95) * mm});
            skLineSegment(sketch, "E55.14.13.1", {"start": v(39.3, -56.95) * mm, "end": v(32.3, -56.95) * mm});
            skLineSegment(sketch, "E55.14.13.2", {"start": v(39.3, -63.95) * mm, "end": v(32.3, -63.95) * mm});
            skLineSegment(sketch, "E55.14.13.3", {"start": v(32.3, -63.95) * mm, "end": v(32.3, -56.95) * mm});
            skLineSegment(sketch, "E55.14.14.0", {"start": v(39.3, -70.95) * mm, "end": v(39.3, -63.95) * mm});
            skLineSegment(sketch, "E55.14.14.1", {"start": v(39.3, -63.95) * mm, "end": v(32.3, -63.95) * mm});
            skLineSegment(sketch, "E55.14.14.2", {"start": v(39.3, -70.95) * mm, "end": v(32.3, -70.95) * mm});
            skLineSegment(sketch, "E55.14.14.3", {"start": v(32.3, -70.95) * mm, "end": v(32.3, -63.95) * mm});
            skLineSegment(sketch, "E55.14.15.0", {"start": v(39.3, -77.95) * mm, "end": v(39.3, -70.95) * mm});
            skLineSegment(sketch, "E55.14.15.1", {"start": v(39.3, -70.95) * mm, "end": v(32.3, -70.95) * mm});
            skLineSegment(sketch, "E55.14.15.2", {"start": v(39.3, -77.95) * mm, "end": v(32.3, -77.95) * mm});
            skLineSegment(sketch, "E55.14.15.3", {"start": v(32.3, -77.95) * mm, "end": v(32.3, -70.95) * mm});
            skLineSegment(sketch, "E55.15.0.0", {"start": v(46.3, 27.05) * mm, "end": v(46.3, 34.05) * mm});
            skLineSegment(sketch, "E55.15.0.1", {"start": v(46.3, 34.05) * mm, "end": v(39.3, 34.05) * mm});
            skLineSegment(sketch, "E55.15.0.2", {"start": v(46.3, 27.05) * mm, "end": v(39.3, 27.05) * mm});
            skLineSegment(sketch, "E55.15.0.3", {"start": v(39.3, 27.05) * mm, "end": v(39.3, 34.05) * mm});
            skLineSegment(sketch, "E55.15.1.0", {"start": v(46.3, 20.05) * mm, "end": v(46.3, 27.05) * mm});
            skLineSegment(sketch, "E55.15.1.1", {"start": v(46.3, 27.05) * mm, "end": v(39.3, 27.05) * mm});
            skLineSegment(sketch, "E55.15.1.2", {"start": v(46.3, 20.05) * mm, "end": v(39.3, 20.05) * mm});
            skLineSegment(sketch, "E55.15.1.3", {"start": v(39.3, 20.05) * mm, "end": v(39.3, 27.05) * mm});
            skLineSegment(sketch, "E55.15.2.0", {"start": v(46.3, 13.05) * mm, "end": v(46.3, 20.05) * mm});
            skLineSegment(sketch, "E55.15.2.1", {"start": v(46.3, 20.05) * mm, "end": v(39.3, 20.05) * mm});
            skLineSegment(sketch, "E55.15.2.2", {"start": v(46.3, 13.05) * mm, "end": v(39.3, 13.05) * mm});
            skLineSegment(sketch, "E55.15.2.3", {"start": v(39.3, 13.05) * mm, "end": v(39.3, 20.05) * mm});
            skLineSegment(sketch, "E55.15.3.0", {"start": v(46.3, 6.05) * mm, "end": v(46.3, 13.05) * mm});
            skLineSegment(sketch, "E55.15.3.1", {"start": v(46.3, 13.05) * mm, "end": v(39.3, 13.05) * mm});
            skLineSegment(sketch, "E55.15.3.2", {"start": v(46.3, 6.05) * mm, "end": v(39.3, 6.05) * mm});
            skLineSegment(sketch, "E55.15.3.3", {"start": v(39.3, 6.05) * mm, "end": v(39.3, 13.05) * mm});
            skLineSegment(sketch, "E55.15.4.0", {"start": v(46.3, -0.95) * mm, "end": v(46.3, 6.05) * mm});
            skLineSegment(sketch, "E55.15.4.1", {"start": v(46.3, 6.05) * mm, "end": v(39.3, 6.05) * mm});
            skLineSegment(sketch, "E55.15.4.2", {"start": v(46.3, -0.95) * mm, "end": v(39.3, -0.95) * mm});
            skLineSegment(sketch, "E55.15.4.3", {"start": v(39.3, -0.95) * mm, "end": v(39.3, 6.05) * mm});
            skLineSegment(sketch, "E55.15.5.0", {"start": v(46.3, -7.95) * mm, "end": v(46.3, -0.95) * mm});
            skLineSegment(sketch, "E55.15.5.1", {"start": v(46.3, -0.95) * mm, "end": v(39.3, -0.95) * mm});
            skLineSegment(sketch, "E55.15.5.2", {"start": v(46.3, -7.95) * mm, "end": v(39.3, -7.95) * mm});
            skLineSegment(sketch, "E55.15.5.3", {"start": v(39.3, -7.95) * mm, "end": v(39.3, -0.95) * mm});
            skLineSegment(sketch, "E55.15.6.0", {"start": v(46.3, -14.95) * mm, "end": v(46.3, -7.95) * mm});
            skLineSegment(sketch, "E55.15.6.1", {"start": v(46.3, -7.95) * mm, "end": v(39.3, -7.95) * mm});
            skLineSegment(sketch, "E55.15.6.2", {"start": v(46.3, -14.95) * mm, "end": v(39.3, -14.95) * mm});
            skLineSegment(sketch, "E55.15.6.3", {"start": v(39.3, -14.95) * mm, "end": v(39.3, -7.95) * mm});
            skLineSegment(sketch, "E55.15.7.0", {"start": v(46.3, -21.95) * mm, "end": v(46.3, -14.95) * mm});
            skLineSegment(sketch, "E55.15.7.1", {"start": v(46.3, -14.95) * mm, "end": v(39.3, -14.95) * mm});
            skLineSegment(sketch, "E55.15.7.2", {"start": v(46.3, -21.95) * mm, "end": v(39.3, -21.95) * mm});
            skLineSegment(sketch, "E55.15.7.3", {"start": v(39.3, -21.95) * mm, "end": v(39.3, -14.95) * mm});
            skLineSegment(sketch, "E55.15.8.0", {"start": v(46.3, -28.95) * mm, "end": v(46.3, -21.95) * mm});
            skLineSegment(sketch, "E55.15.8.1", {"start": v(46.3, -21.95) * mm, "end": v(39.3, -21.95) * mm});
            skLineSegment(sketch, "E55.15.8.2", {"start": v(46.3, -28.95) * mm, "end": v(39.3, -28.95) * mm});
            skLineSegment(sketch, "E55.15.8.3", {"start": v(39.3, -28.95) * mm, "end": v(39.3, -21.95) * mm});
            skLineSegment(sketch, "E55.15.9.0", {"start": v(46.3, -35.95) * mm, "end": v(46.3, -28.95) * mm});
            skLineSegment(sketch, "E55.15.9.1", {"start": v(46.3, -28.95) * mm, "end": v(39.3, -28.95) * mm});
            skLineSegment(sketch, "E55.15.9.2", {"start": v(46.3, -35.95) * mm, "end": v(39.3, -35.95) * mm});
            skLineSegment(sketch, "E55.15.9.3", {"start": v(39.3, -35.95) * mm, "end": v(39.3, -28.95) * mm});
            skLineSegment(sketch, "E55.15.10.0", {"start": v(46.3, -42.95) * mm, "end": v(46.3, -35.95) * mm});
            skLineSegment(sketch, "E55.15.10.1", {"start": v(46.3, -35.95) * mm, "end": v(39.3, -35.95) * mm});
            skLineSegment(sketch, "E55.15.10.2", {"start": v(46.3, -42.95) * mm, "end": v(39.3, -42.95) * mm});
            skLineSegment(sketch, "E55.15.10.3", {"start": v(39.3, -42.95) * mm, "end": v(39.3, -35.95) * mm});
            skLineSegment(sketch, "E55.15.11.0", {"start": v(46.3, -49.95) * mm, "end": v(46.3, -42.95) * mm});
            skLineSegment(sketch, "E55.15.11.1", {"start": v(46.3, -42.95) * mm, "end": v(39.3, -42.95) * mm});
            skLineSegment(sketch, "E55.15.11.2", {"start": v(46.3, -49.95) * mm, "end": v(39.3, -49.95) * mm});
            skLineSegment(sketch, "E55.15.11.3", {"start": v(39.3, -49.95) * mm, "end": v(39.3, -42.95) * mm});
            skLineSegment(sketch, "E55.15.12.0", {"start": v(46.3, -56.95) * mm, "end": v(46.3, -49.95) * mm});
            skLineSegment(sketch, "E55.15.12.1", {"start": v(46.3, -49.95) * mm, "end": v(39.3, -49.95) * mm});
            skLineSegment(sketch, "E55.15.12.2", {"start": v(46.3, -56.95) * mm, "end": v(39.3, -56.95) * mm});
            skLineSegment(sketch, "E55.15.12.3", {"start": v(39.3, -56.95) * mm, "end": v(39.3, -49.95) * mm});
            skLineSegment(sketch, "E55.15.13.0", {"start": v(46.3, -63.95) * mm, "end": v(46.3, -56.95) * mm});
            skLineSegment(sketch, "E55.15.13.1", {"start": v(46.3, -56.95) * mm, "end": v(39.3, -56.95) * mm});
            skLineSegment(sketch, "E55.15.13.2", {"start": v(46.3, -63.95) * mm, "end": v(39.3, -63.95) * mm});
            skLineSegment(sketch, "E55.15.13.3", {"start": v(39.3, -63.95) * mm, "end": v(39.3, -56.95) * mm});
            skLineSegment(sketch, "E55.15.14.0", {"start": v(46.3, -70.95) * mm, "end": v(46.3, -63.95) * mm});
            skLineSegment(sketch, "E55.15.14.1", {"start": v(46.3, -63.95) * mm, "end": v(39.3, -63.95) * mm});
            skLineSegment(sketch, "E55.15.14.2", {"start": v(46.3, -70.95) * mm, "end": v(39.3, -70.95) * mm});
            skLineSegment(sketch, "E55.15.14.3", {"start": v(39.3, -70.95) * mm, "end": v(39.3, -63.95) * mm});
            skLineSegment(sketch, "E55.15.15.0", {"start": v(46.3, -77.95) * mm, "end": v(46.3, -70.95) * mm});
            skLineSegment(sketch, "E55.15.15.1", {"start": v(46.3, -70.95) * mm, "end": v(39.3, -70.95) * mm});
            skLineSegment(sketch, "E55.15.15.2", {"start": v(46.3, -77.95) * mm, "end": v(39.3, -77.95) * mm});
            skLineSegment(sketch, "E55.15.15.3", {"start": v(39.3, -77.95) * mm, "end": v(39.3, -70.95) * mm});
            skLineSegment(sketch, "E55.direction1", {"start": v(-58.7, 27.05) * mm, "end": v(-51.7, 27.05) * mm, "construction": true});
            skLineSegment(sketch, "E55.direction2", {"start": v(-58.7, 27.05) * mm, "end": v(-58.7, 20.05) * mm, "construction": true});
            skSolve(sketch);
        }
        {
            var Q0;
            Q0=makeQuery(id+"F2.imprint","IMPRINT",FACE,{"disambiguationData":[TD([[makeQuery(id+"F2.imprint","IMPRINT",EDGE,{"derivedFrom":sQuery(id+"F2.wireOp",EDGE,"E55.2.0.1")}),1.0]])]});
            var Q1;
            Q1=makeQuery(id+"F2.imprint","IMPRINT",FACE,{"disambiguationData":[TD([[makeQuery(id+"F2.imprint","IMPRINT",EDGE,{"derivedFrom":sQuery(id+"F2.wireOp",EDGE,"E55.4.0.1")}),1.0]])]});
            var Q2;
            Q2=makeQuery(id+"F2.imprint","IMPRINT",FACE,{"disambiguationData":[TD([[makeQuery(id+"F2.imprint","IMPRINT",EDGE,{"derivedFrom":sQuery(id+"F2.wireOp",EDGE,"E55.10.0.1")}),1.0]])]});
            var Q3;
            Q3=makeQuery(id+"F2.imprint","IMPRINT",FACE,{"disambiguationData":[TD([[makeQuery(id+"F2.imprint","IMPRINT",EDGE,{"derivedFrom":sQuery(id+"F2.wireOp",EDGE,"E55.12.0.1")}),1.0]])]});
            var Q4;
            Q4=makeQuery(id+"F2.imprint","IMPRINT",FACE,{"disambiguationData":[TD([[makeQuery(id+"F2.imprint","IMPRINT",EDGE,{"derivedFrom":sQuery(id+"F2.wireOp",EDGE,"E55.3.1.1")}),1.0]])]});
            var Q5;
            Q5=makeQuery(id+"F2.imprint","IMPRINT",FACE,{"disambiguationData":[TD([[makeQuery(id+"F2.imprint","IMPRINT",EDGE,{"derivedFrom":sQuery(id+"F2.wireOp",EDGE,"E55.5.1.1")}),1.0]])]});
            var Q6;
            Q6=makeQuery(id+"F2.imprint","IMPRINT",FACE,{"disambiguationData":[TD([[makeQuery(id+"F2.imprint","IMPRINT",EDGE,{"derivedFrom":sQuery(id+"F2.wireOp",EDGE,"E55.9.1.1")}),1.0]])]});
            var Q7;
            Q7=makeQuery(id+"F2.imprint","IMPRINT",FACE,{"disambiguationData":[TD([[makeQuery(id+"F2.imprint","IMPRINT",EDGE,{"derivedFrom":sQuery(id+"F2.wireOp",EDGE,"E55.1.1.1")}),1.0]])]});
            var Q8;
            Q8=makeQuery(id+"F2.imprint","IMPRINT",FACE,{"disambiguationData":[TD([[makeQuery(id+"F2.imprint","IMPRINT",EDGE,{"derivedFrom":sQuery(id+"F2.wireOp",EDGE,"E55.11.1.1")}),1.0]])]});
            var Q9;
            Q9=makeQuery(id+"F2.imprint","IMPRINT",FACE,{"disambiguationData":[TD([[makeQuery(id+"F2.imprint","IMPRINT",EDGE,{"derivedFrom":sQuery(id+"F2.wireOp",EDGE,"E55.13.1.1")}),1.0]])]});
            var Q10;
            Q10=makeQuery(id+"F2.imprint","IMPRINT",FACE,{"disambiguationData":[TD([[makeQuery(id+"F2.imprint","IMPRINT",EDGE,{"derivedFrom":sQuery(id+"F2.wireOp",EDGE,"E55.0.2.1")}),1.0]])]});
            var Q11;
            Q11=makeQuery(id+"F2.imprint","IMPRINT",FACE,{"disambiguationData":[TD([[makeQuery(id+"F2.imprint","IMPRINT",EDGE,{"derivedFrom":sQuery(id+"F2.wireOp",EDGE,"E55.2.2.1")}),1.0]])]});
            var Q12;
            Q12=makeQuery(id+"F2.imprint","IMPRINT",FACE,{"disambiguationData":[TD([[makeQuery(id+"F2.imprint","IMPRINT",EDGE,{"derivedFrom":sQuery(id+"F2.wireOp",EDGE,"E55.4.2.1")}),1.0]])]});
            var Q13;
            Q13=makeQuery(id+"F2.imprint","IMPRINT",FACE,{"disambiguationData":[TD([[makeQuery(id+"F2.imprint","IMPRINT",EDGE,{"derivedFrom":sQuery(id+"F2.wireOp",EDGE,"E55.6.2.1")}),1.0]])]});
            var Q14;
            Q14=makeQuery(id+"F2.imprint","IMPRINT",FACE,{"disambiguationData":[TD([[makeQuery(id+"F2.imprint","IMPRINT",EDGE,{"derivedFrom":sQuery(id+"F2.wireOp",EDGE,"E55.8.2.1")}),1.0]])]});
            var Q15;
            Q15=makeQuery(id+"F2.imprint","IMPRINT",FACE,{"disambiguationData":[TD([[makeQuery(id+"F2.imprint","IMPRINT",EDGE,{"derivedFrom":sQuery(id+"F2.wireOp",EDGE,"E55.10.2.1")}),1.0]])]});
            var Q16;
            Q16=makeQuery(id+"F2.imprint","IMPRINT",FACE,{"disambiguationData":[TD([[makeQuery(id+"F2.imprint","IMPRINT",EDGE,{"derivedFrom":sQuery(id+"F2.wireOp",EDGE,"E55.14.2.1")}),1.0]])]});
            var Q17;
            Q17=makeQuery(id+"F2.imprint","IMPRINT",FACE,{"disambiguationData":[TD([[makeQuery(id+"F2.imprint","IMPRINT",EDGE,{"derivedFrom":sQuery(id+"F2.wireOp",EDGE,"E55.15.3.0")}),1.0]])]});
            var Q18;
            Q18=makeQuery(id+"F2.imprint","IMPRINT",FACE,{"disambiguationData":[TD([[makeQuery(id+"F2.imprint","IMPRINT",EDGE,{"derivedFrom":sQuery(id+"F2.wireOp",EDGE,"E55.11.3.1")}),1.0]])]});
            var Q19;
            Q19=makeQuery(id+"F2.imprint","IMPRINT",FACE,{"disambiguationData":[TD([[makeQuery(id+"F2.imprint","IMPRINT",EDGE,{"derivedFrom":sQuery(id+"F2.wireOp",EDGE,"E55.9.3.1")}),1.0]])]});
            var Q20;
            Q20=makeQuery(id+"F2.imprint","IMPRINT",FACE,{"disambiguationData":[TD([[makeQuery(id+"F2.imprint","IMPRINT",EDGE,{"derivedFrom":sQuery(id+"F2.wireOp",EDGE,"E55.7.3.1")}),1.0]])]});
            var Q21;
            Q21=makeQuery(id+"F2.imprint","IMPRINT",FACE,{"disambiguationData":[TD([[makeQuery(id+"F2.imprint","IMPRINT",EDGE,{"derivedFrom":sQuery(id+"F2.wireOp",EDGE,"E55.5.3.1")}),1.0]])]});
            var Q22;
            Q22=makeQuery(id+"F2.imprint","IMPRINT",FACE,{"disambiguationData":[TD([[makeQuery(id+"F2.imprint","IMPRINT",EDGE,{"derivedFrom":sQuery(id+"F2.wireOp",EDGE,"E55.3.3.1")}),1.0]])]});
            var Q23;
            Q23=makeQuery(id+"F2.imprint","IMPRINT",FACE,{"disambiguationData":[TD([[makeQuery(id+"F2.imprint","IMPRINT",EDGE,{"derivedFrom":sQuery(id+"F2.wireOp",EDGE,"E55.1.3.1")}),1.0]])]});
            var Q24;
            Q24=makeQuery(id+"F2.imprint","IMPRINT",FACE,{"disambiguationData":[TD([[makeQuery(id+"F2.imprint","IMPRINT",EDGE,{"derivedFrom":sQuery(id+"F2.wireOp",EDGE,"E55.0.4.1")}),1.0]])]});
            var Q25;
            Q25=makeQuery(id+"F2.imprint","IMPRINT",FACE,{"disambiguationData":[TD([[makeQuery(id+"F2.imprint","IMPRINT",EDGE,{"derivedFrom":sQuery(id+"F2.wireOp",EDGE,"E55.2.4.1")}),1.0]])]});
            var Q26;
            Q26=makeQuery(id+"F2.imprint","IMPRINT",FACE,{"disambiguationData":[TD([[makeQuery(id+"F2.imprint","IMPRINT",EDGE,{"derivedFrom":sQuery(id+"F2.wireOp",EDGE,"E55.4.4.1")}),1.0]])]});
            var Q27;
            Q27=makeQuery(id+"F2.imprint","IMPRINT",FACE,{"disambiguationData":[TD([[makeQuery(id+"F2.imprint","IMPRINT",EDGE,{"derivedFrom":sQuery(id+"F2.wireOp",EDGE,"E55.6.4.1")}),1.0]])]});
            var Q28;
            Q28=makeQuery(id+"F2.imprint","IMPRINT",FACE,{"disambiguationData":[TD([[makeQuery(id+"F2.imprint","IMPRINT",EDGE,{"derivedFrom":sQuery(id+"F2.wireOp",EDGE,"E55.8.4.1")}),1.0]])]});
            var Q29;
            Q29=makeQuery(id+"F2.imprint","IMPRINT",FACE,{"disambiguationData":[TD([[makeQuery(id+"F2.imprint","IMPRINT",EDGE,{"derivedFrom":sQuery(id+"F2.wireOp",EDGE,"E55.10.4.1")}),1.0]])]});
            var Q30;
            Q30=makeQuery(id+"F2.imprint","IMPRINT",FACE,{"disambiguationData":[TD([[makeQuery(id+"F2.imprint","IMPRINT",EDGE,{"derivedFrom":sQuery(id+"F2.wireOp",EDGE,"E55.12.4.1")}),-1.0]])]});
            var Q31;
            Q31=makeQuery(id+"F2.imprint","IMPRINT",FACE,{"disambiguationData":[TD([[makeQuery(id+"F2.imprint","IMPRINT",EDGE,{"derivedFrom":sQuery(id+"F2.wireOp",EDGE,"E55.14.4.1")}),1.0]])]});
            var Q32;
            {var subQ2=sQuery(id+"F2.wireOp",EDGE,"E55.15.5.1");Q32=makeQuery(id+"F2.imprint","IMPRINT",FACE,{"disambiguationData":[TD([[makeQuery(id+"F2.imprint","IMPRINT",EDGE,{"derivedFrom":subQ2}),1.0]])]});}
            var Q33;
            Q33=makeQuery(id+"F2.imprint","IMPRINT",FACE,{"disambiguationData":[TD([[makeQuery(id+"F2.imprint","IMPRINT",EDGE,{"derivedFrom":sQuery(id+"F2.wireOp",EDGE,"E55.13.5.1")}),1.0]])]});
            var Q34;
            Q34=makeQuery(id+"F2.imprint","IMPRINT",FACE,{"disambiguationData":[TD([[makeQuery(id+"F2.imprint","IMPRINT",EDGE,{"derivedFrom":sQuery(id+"F2.wireOp",EDGE,"E55.11.5.1")}),1.0]])]});
            var Q35;
            Q35=makeQuery(id+"F2.imprint","IMPRINT",FACE,{"disambiguationData":[TD([[makeQuery(id+"F2.imprint","IMPRINT",EDGE,{"derivedFrom":sQuery(id+"F2.wireOp",EDGE,"E55.9.5.1")}),1.0]])]});
            var Q36;
            Q36=makeQuery(id+"F2.imprint","IMPRINT",FACE,{"disambiguationData":[TD([[makeQuery(id+"F2.imprint","IMPRINT",EDGE,{"derivedFrom":sQuery(id+"F2.wireOp",EDGE,"E55.7.5.1")}),1.0]])]});
            var Q37;
            Q37=makeQuery(id+"F2.imprint","IMPRINT",FACE,{"disambiguationData":[TD([[makeQuery(id+"F2.imprint","IMPRINT",EDGE,{"derivedFrom":sQuery(id+"F2.wireOp",EDGE,"E55.5.5.1")}),1.0]])]});
            var Q38;
            Q38=makeQuery(id+"F2.imprint","IMPRINT",FACE,{"disambiguationData":[TD([[makeQuery(id+"F2.imprint","IMPRINT",EDGE,{"derivedFrom":sQuery(id+"F2.wireOp",EDGE,"E55.3.5.1")}),1.0]])]});
            var Q39;
            Q39=makeQuery(id+"F2.imprint","IMPRINT",FACE,{"disambiguationData":[TD([[makeQuery(id+"F2.imprint","IMPRINT",EDGE,{"derivedFrom":sQuery(id+"F2.wireOp",EDGE,"E55.1.5.1")}),1.0]])]});
            var Q40;
            Q40=makeQuery(id+"F2.imprint","IMPRINT",FACE,{"disambiguationData":[TD([[makeQuery(id+"F2.imprint","IMPRINT",EDGE,{"derivedFrom":sQuery(id+"F2.wireOp",EDGE,"E55.2.6.1")}),1.0]])]});
            var Q41;
            Q41=makeQuery(id+"F2.imprint","IMPRINT",FACE,{"disambiguationData":[TD([[makeQuery(id+"F2.imprint","IMPRINT",EDGE,{"derivedFrom":sQuery(id+"F2.wireOp",EDGE,"E55.4.6.1")}),1.0]])]});
            var Q42;
            Q42=makeQuery(id+"F2.imprint","IMPRINT",FACE,{"disambiguationData":[TD([[makeQuery(id+"F2.imprint","IMPRINT",EDGE,{"derivedFrom":sQuery(id+"F2.wireOp",EDGE,"E55.6.6.1")}),1.0]])]});
            var Q43;
            Q43=makeQuery(id+"F2.imprint","IMPRINT",FACE,{"disambiguationData":[TD([[makeQuery(id+"F2.imprint","IMPRINT",EDGE,{"derivedFrom":sQuery(id+"F2.wireOp",EDGE,"E55.8.6.1")}),1.0]])]});
            var Q44;
            Q44=makeQuery(id+"F2.imprint","IMPRINT",FACE,{"disambiguationData":[TD([[makeQuery(id+"F2.imprint","IMPRINT",EDGE,{"derivedFrom":sQuery(id+"F2.wireOp",EDGE,"E55.10.6.1")}),1.0]])]});
            var Q45;
            Q45=makeQuery(id+"F2.imprint","IMPRINT",FACE,{"disambiguationData":[TD([[makeQuery(id+"F2.imprint","IMPRINT",EDGE,{"derivedFrom":sQuery(id+"F2.wireOp",EDGE,"E55.12.6.1")}),1.0]])]});
            var Q46;
            Q46=makeQuery(id+"F2.imprint","IMPRINT",FACE,{"disambiguationData":[TD([[makeQuery(id+"F2.imprint","IMPRINT",EDGE,{"derivedFrom":sQuery(id+"F2.wireOp",EDGE,"E55.14.6.1")}),1.0]])]});
            var Q47;
            Q47=makeQuery(id+"F2.imprint","IMPRINT",FACE,{"disambiguationData":[TD([[makeQuery(id+"F2.imprint","IMPRINT",EDGE,{"derivedFrom":sQuery(id+"F2.wireOp",EDGE,"E55.1.7.1")}),1.0]])]});
            var Q48;
            Q48=makeQuery(id+"F2.imprint","IMPRINT",FACE,{"disambiguationData":[TD([[makeQuery(id+"F2.imprint","IMPRINT",EDGE,{"derivedFrom":sQuery(id+"F2.wireOp",EDGE,"E55.3.7.1")}),1.0]])]});
            var Q49;
            Q49=makeQuery(id+"F2.imprint","IMPRINT",FACE,{"disambiguationData":[TD([[makeQuery(id+"F2.imprint","IMPRINT",EDGE,{"derivedFrom":sQuery(id+"F2.wireOp",EDGE,"E55.5.7.1")}),1.0]])]});
            var Q50;
            Q50=makeQuery(id+"F2.imprint","IMPRINT",FACE,{"disambiguationData":[TD([[makeQuery(id+"F2.imprint","IMPRINT",EDGE,{"derivedFrom":sQuery(id+"F2.wireOp",EDGE,"E55.7.7.1")}),1.0]])]});
            var Q51;
            Q51=makeQuery(id+"F2.imprint","IMPRINT",FACE,{"disambiguationData":[TD([[makeQuery(id+"F2.imprint","IMPRINT",EDGE,{"derivedFrom":sQuery(id+"F2.wireOp",EDGE,"E55.9.7.1")}),1.0]])]});
            var Q52;
            Q52=makeQuery(id+"F2.imprint","IMPRINT",FACE,{"disambiguationData":[TD([[makeQuery(id+"F2.imprint","IMPRINT",EDGE,{"derivedFrom":sQuery(id+"F2.wireOp",EDGE,"E55.11.7.1")}),1.0]])]});
            var Q53;
            Q53=makeQuery(id+"F2.imprint","IMPRINT",FACE,{"disambiguationData":[TD([[makeQuery(id+"F2.imprint","IMPRINT",EDGE,{"derivedFrom":sQuery(id+"F2.wireOp",EDGE,"E55.13.7.1")}),1.0]])]});
            var Q54;
            Q54=makeQuery(id+"F2.imprint","IMPRINT",FACE,{"disambiguationData":[TD([[makeQuery(id+"F2.imprint","IMPRINT",EDGE,{"derivedFrom":sQuery(id+"F2.wireOp",EDGE,"E55.12.8.1")}),1.0]])]});
            var Q55;
            Q55=makeQuery(id+"F2.imprint","IMPRINT",FACE,{"disambiguationData":[TD([[makeQuery(id+"F2.imprint","IMPRINT",EDGE,{"derivedFrom":sQuery(id+"F2.wireOp",EDGE,"E55.10.8.1")}),1.0]])]});
            var Q56;
            Q56=makeQuery(id+"F2.imprint","IMPRINT",FACE,{"disambiguationData":[TD([[makeQuery(id+"F2.imprint","IMPRINT",EDGE,{"derivedFrom":sQuery(id+"F2.wireOp",EDGE,"E55.8.8.1")}),1.0]])]});
            var Q57;
            Q57=makeQuery(id+"F2.imprint","IMPRINT",FACE,{"disambiguationData":[TD([[makeQuery(id+"F2.imprint","IMPRINT",EDGE,{"derivedFrom":sQuery(id+"F2.wireOp",EDGE,"E55.6.8.1")}),1.0]])]});
            var Q58;
            Q58=makeQuery(id+"F2.imprint","IMPRINT",FACE,{"disambiguationData":[TD([[makeQuery(id+"F2.imprint","IMPRINT",EDGE,{"derivedFrom":sQuery(id+"F2.wireOp",EDGE,"E55.4.8.1")}),1.0]])]});
            var Q59;
            Q59=makeQuery(id+"F2.imprint","IMPRINT",FACE,{"disambiguationData":[TD([[makeQuery(id+"F2.imprint","IMPRINT",EDGE,{"derivedFrom":sQuery(id+"F2.wireOp",EDGE,"E55.2.8.1")}),1.0]])]});
            var Q60;
            Q60=makeQuery(id+"F2.imprint","IMPRINT",FACE,{"disambiguationData":[TD([[makeQuery(id+"F2.imprint","IMPRINT",EDGE,{"derivedFrom":sQuery(id+"F2.wireOp",EDGE,"E55.3.9.1")}),1.0]])]});
            var Q61;
            Q61=makeQuery(id+"F2.imprint","IMPRINT",FACE,{"disambiguationData":[TD([[makeQuery(id+"F2.imprint","IMPRINT",EDGE,{"derivedFrom":sQuery(id+"F2.wireOp",EDGE,"E55.5.9.1")}),1.0]])]});
            var Q62;
            Q62=makeQuery(id+"F2.imprint","IMPRINT",FACE,{"disambiguationData":[TD([[makeQuery(id+"F2.imprint","IMPRINT",EDGE,{"derivedFrom":sQuery(id+"F2.wireOp",EDGE,"E55.7.9.1")}),1.0]])]});
            var Q63;
            Q63=makeQuery(id+"F2.imprint","IMPRINT",FACE,{"disambiguationData":[TD([[makeQuery(id+"F2.imprint","IMPRINT",EDGE,{"derivedFrom":sQuery(id+"F2.wireOp",EDGE,"E55.9.9.1")}),1.0]])]});
            var Q64;
            Q64=makeQuery(id+"F2.imprint","IMPRINT",FACE,{"disambiguationData":[TD([[makeQuery(id+"F2.imprint","IMPRINT",EDGE,{"derivedFrom":sQuery(id+"F2.wireOp",EDGE,"E55.11.9.1")}),1.0]])]});
            var Q65;
            Q65=makeQuery(id+"F2.imprint","IMPRINT",FACE,{"disambiguationData":[TD([[makeQuery(id+"F2.imprint","IMPRINT",EDGE,{"derivedFrom":sQuery(id+"F2.wireOp",EDGE,"E55.10.10.1")}),1.0]])]});
            var Q66;
            Q66=makeQuery(id+"F2.imprint","IMPRINT",FACE,{"disambiguationData":[TD([[makeQuery(id+"F2.imprint","IMPRINT",EDGE,{"derivedFrom":sQuery(id+"F2.wireOp",EDGE,"E55.8.10.1")}),1.0]])]});
            var Q67;
            Q67=makeQuery(id+"F2.imprint","IMPRINT",FACE,{"disambiguationData":[TD([[makeQuery(id+"F2.imprint","IMPRINT",EDGE,{"derivedFrom":sQuery(id+"F2.wireOp",EDGE,"E55.6.10.1")}),1.0]])]});
            var Q68;
            Q68=makeQuery(id+"F2.imprint","IMPRINT",FACE,{"disambiguationData":[TD([[makeQuery(id+"F2.imprint","IMPRINT",EDGE,{"derivedFrom":sQuery(id+"F2.wireOp",EDGE,"E55.4.10.1")}),1.0]])]});
            var Q69;
            Q69=makeQuery(id+"F2.imprint","IMPRINT",FACE,{"disambiguationData":[TD([[makeQuery(id+"F2.imprint","IMPRINT",EDGE,{"derivedFrom":sQuery(id+"F2.wireOp",EDGE,"E55.5.11.1")}),1.0]])]});
            var Q70;
            Q70=makeQuery(id+"F2.imprint","IMPRINT",FACE,{"disambiguationData":[TD([[makeQuery(id+"F2.imprint","IMPRINT",EDGE,{"derivedFrom":sQuery(id+"F2.wireOp",EDGE,"E55.7.11.1")}),1.0]])]});
            var Q71;
            Q71=makeQuery(id+"F2.imprint","IMPRINT",FACE,{"disambiguationData":[TD([[makeQuery(id+"F2.imprint","IMPRINT",EDGE,{"derivedFrom":sQuery(id+"F2.wireOp",EDGE,"E55.9.11.1")}),1.0]])]});
            var Q72;
            Q72=makeQuery(id+"F2.imprint","IMPRINT",FACE,{"disambiguationData":[TD([[makeQuery(id+"F2.imprint","IMPRINT",EDGE,{"derivedFrom":sQuery(id+"F2.wireOp",EDGE,"E55.8.12.1")}),1.0]])]});
            var Q73;
            Q73=makeQuery(id+"F2.imprint","IMPRINT",FACE,{"disambiguationData":[TD([[makeQuery(id+"F2.imprint","IMPRINT",EDGE,{"derivedFrom":sQuery(id+"F2.wireOp",EDGE,"E55.6.12.1")}),1.0]])]});
            var Q74;
            Q74=makeQuery(id+"F2.imprint","IMPRINT",FACE,{"disambiguationData":[TD([[makeQuery(id+"F2.imprint","IMPRINT",EDGE,{"derivedFrom":sQuery(id+"F2.wireOp",EDGE,"E55.7.13.1")}),1.0]])]});
            extrude(context, id + "F3", {"entities" : qUnion([Q0, Q1, Q2, Q3, Q4, Q5, Q6, Q7, Q8, Q9, Q10, Q11, Q12, Q13, Q14, Q15, Q16, Q17, Q18, Q19, Q20, Q21, Q22, Q23, Q24, Q25, Q26, Q27, Q28, Q29, Q30, Q31, Q32, Q33, Q34, Q35, Q36, Q37, Q38, Q39, Q40, Q41, Q42, Q43, Q44, Q45, Q46, Q47, Q48, Q49, Q50, Q51, Q52, Q53, Q54, Q55, Q56, Q57, Q58, Q59, Q60, Q61, Q62, Q63, Q64, Q65, Q66, Q67, Q68, Q69, Q70, Q71, Q72, Q73, Q74]), "operationType" : NewBodyOperationType.ADD, "depth" : 2 * mm, "offsetDistance" : 25 * mm, "hasDraft" : true, "draftAngle" : 55 * degree, "draftPullDirection" : true, "hasSecondDirection" : true, "secondDirectionOppositeDirection" : true, "secondDirectionDepth" : 1 * mm});
        }
        {
            var Q0;
            Q0=makeQuery(id+"F1.opExtrude","CAP_FACE",FACE,{"disambiguationData":[OSD([sQuery(id+"F0.wireOp",EDGE,"E0"),sQuery(id+"F0.wireOp",EDGE,"E1"),sQuery(id+"F0.wireOp",EDGE,"E2"),sQuery(id+"F0.wireOp",EDGE,"E3"),sQuery(id+"F0.wireOp",EDGE,"E4"),sQuery(id+"F0.wireOp",EDGE,"E5"),sQuery(id+"F0.wireOp",EDGE,"E6"),sQuery(id+"F0.wireOp",EDGE,"E7"),sQuery(id+"F0.wireOp",EDGE,"E8"),sQuery(id+"F0.wireOp",EDGE,"E9"),sQuery(id+"F0.wireOp",EDGE,"E10"),sQuery(id+"F0.wireOp",EDGE,"E11"),sQuery(id+"F0.wireOp",EDGE,"E12"),sQuery(id+"F0.wireOp",EDGE,"E13"),sQuery(id+"F0.wireOp",EDGE,"E14"),sQuery(id+"F0.wireOp",EDGE,"E15"),sQuery(id+"F0.wireOp",EDGE,"E16"),sQuery(id+"F0.wireOp",EDGE,"E17"),sQuery(id+"F0.wireOp",EDGE,"E18"),sQuery(id+"F0.wireOp",EDGE,"E19"),sQuery(id+"F0.wireOp",EDGE,"E20"),sQuery(id+"F0.wireOp",EDGE,"E21"),sQuery(id+"F0.wireOp",EDGE,"E22"),sQuery(id+"F0.wireOp",EDGE,"E23"),sQuery(id+"F0.wireOp",EDGE,"E24"),sQuery(id+"F0.wireOp",EDGE,"E25"),sQuery(id+"F0.wireOp",EDGE,"E26"),sQuery(id+"F0.wireOp",EDGE,"E27"),sQuery(id+"F0.wireOp",EDGE,"E28"),sQuery(id+"F0.wireOp",EDGE,"E29"),sQuery(id+"F0.wireOp",EDGE,"E30"),sQuery(id+"F0.wireOp",EDGE,"E31"),sQuery(id+"F0.wireOp",EDGE,"E32"),sQuery(id+"F0.wireOp",EDGE,"E33"),sQuery(id+"F0.wireOp",EDGE,"E34"),sQuery(id+"F0.wireOp",EDGE,"E35"),sQuery(id+"F0.wireOp",EDGE,"E36"),sQuery(id+"F0.wireOp",EDGE,"E37"),sQuery(id+"F0.wireOp",EDGE,"E38"),sQuery(id+"F0.wireOp",EDGE,"E39"),sQuery(id+"F0.wireOp",EDGE,"E40"),sQuery(id+"F0.wireOp",EDGE,"E41"),sQuery(id+"F0.wireOp",EDGE,"E42"),sQuery(id+"F0.wireOp",EDGE,"E43"),sQuery(id+"F0.wireOp",EDGE,"E44"),sQuery(id+"F0.wireOp",EDGE,"E45"),sQuery(id+"F0.wireOp",EDGE,"E46"),sQuery(id+"F0.wireOp",EDGE,"E47"),sQuery(id+"F0.wireOp",EDGE,"E48"),sQuery(id+"F0.wireOp",EDGE,"E49"),sQuery(id+"F0.wireOp",EDGE,"E50"),sQuery(id+"F0.wireOp",EDGE,"E51"),sQuery(id+"F0.wireOp",EDGE,"E52"),sQuery(id+"F0.wireOp",EDGE,"E53")])],"isStart":true});
            var sketch = newSketch(context, id + "F4", { "sketchPlane" : qUnion([Q0])});
            skLineSegment(sketch, "E56", {"start": v(-65.7, 65.9) * mm, "end": v(-65.7, -34.05) * mm});
            skPoint(sketch, "E56.startSnap0", {"position": v(-10.57, 65.9) * mm});
            skLineSegment(sketch, "E57.1.0.0", {"start": v(-58.7, 65.9) * mm, "end": v(-58.7, -34.05) * mm});
            skLineSegment(sketch, "E57.2.0.0", {"start": v(-51.7, 65.9) * mm, "end": v(-51.7, -34.05) * mm});
            skLineSegment(sketch, "E57.3.0.0", {"start": v(-44.7, 65.9) * mm, "end": v(-44.7, -34.05) * mm});
            skLineSegment(sketch, "E57.4.0.0", {"start": v(-37.7, 65.9) * mm, "end": v(-37.7, -34.05) * mm});
            skLineSegment(sketch, "E57.5.0.0", {"start": v(-30.7, 65.9) * mm, "end": v(-30.7, -34.05) * mm});
            skLineSegment(sketch, "E57.6.0.0", {"start": v(-23.7, 65.9) * mm, "end": v(-23.7, -34.05) * mm});
            skLineSegment(sketch, "E57.7.0.0", {"start": v(-16.7, 65.9) * mm, "end": v(-16.7, -34.05) * mm});
            skLineSegment(sketch, "E57.8.0.0", {"start": v(-9.7, 65.9) * mm, "end": v(-9.7, -34.05) * mm});
            skLineSegment(sketch, "E57.9.0.0", {"start": v(-2.7, 65.9) * mm, "end": v(-2.7, -34.05) * mm});
            skLineSegment(sketch, "E57.10.0.0", {"start": v(4.3, 65.9) * mm, "end": v(4.3, -34.05) * mm});
            skLineSegment(sketch, "E57.11.0.0", {"start": v(11.3, 65.9) * mm, "end": v(11.3, -34.05) * mm});
            skLineSegment(sketch, "E57.12.0.0", {"start": v(18.3, 65.9) * mm, "end": v(18.3, -34.05) * mm});
            skLineSegment(sketch, "E57.13.0.0", {"start": v(25.3, 65.9) * mm, "end": v(25.3, -34.05) * mm});
            skLineSegment(sketch, "E57.14.0.0", {"start": v(32.3, 65.9) * mm, "end": v(32.3, -34.05) * mm});
            skLineSegment(sketch, "E57.15.0.0", {"start": v(39.3, 65.9) * mm, "end": v(39.3, -34.05) * mm});
            skLineSegment(sketch, "E57.direction1", {"start": v(-65.7, -34.05) * mm, "end": v(-58.7, -34.05) * mm, "construction": true});
            skLineSegment(sketch, "E58", {"start": v(-156.84, 71.09) * mm, "end": v(-9.57, -76.18) * mm});
            skLineSegment(sketch, "E59.1.0.0", {"start": v(-142.84, 71.09) * mm, "end": v(4.43, -76.18) * mm});
            skLineSegment(sketch, "E59.2.0.0", {"start": v(-128.84, 71.09) * mm, "end": v(18.43, -76.18) * mm});
            skLineSegment(sketch, "E59.3.0.0", {"start": v(-114.84, 71.09) * mm, "end": v(32.43, -76.18) * mm});
            skLineSegment(sketch, "E59.4.0.0", {"start": v(-100.84, 71.09) * mm, "end": v(46.43, -76.18) * mm});
            skLineSegment(sketch, "E59.5.0.0", {"start": v(-86.84, 71.09) * mm, "end": v(60.43, -76.18) * mm});
            skLineSegment(sketch, "E59.6.0.0", {"start": v(-72.84, 71.09) * mm, "end": v(74.43, -76.18) * mm});
            skLineSegment(sketch, "E59.7.0.0", {"start": v(-58.84, 71.09) * mm, "end": v(88.43, -76.18) * mm});
            skLineSegment(sketch, "E59.8.0.0", {"start": v(-44.84, 71.09) * mm, "end": v(102.43, -76.18) * mm});
            skLineSegment(sketch, "E59.9.0.0", {"start": v(-30.84, 71.09) * mm, "end": v(116.43, -76.18) * mm});
            skLineSegment(sketch, "E59.10.0.0", {"start": v(-16.84, 71.09) * mm, "end": v(130.43, -76.18) * mm});
            skLineSegment(sketch, "E59.11.0.0", {"start": v(-2.84, 71.09) * mm, "end": v(144.43, -76.18) * mm});
            skLineSegment(sketch, "E59.12.0.0", {"start": v(11.16, 71.09) * mm, "end": v(158.43, -76.18) * mm});
            skLineSegment(sketch, "E59.13.0.0", {"start": v(25.16, 71.09) * mm, "end": v(172.43, -76.18) * mm});
            skLineSegment(sketch, "E59.14.0.0", {"start": v(39.16, 71.09) * mm, "end": v(186.43, -76.18) * mm});
            skLineSegment(sketch, "E59.15.0.0", {"start": v(53.16, 71.09) * mm, "end": v(200.43, -76.18) * mm});
            skLineSegment(sketch, "E59.direction1", {"start": v(-9.57, -76.18) * mm, "end": v(4.43, -76.18) * mm, "construction": true});
            skSolve(sketch);
        }
        {
            var Q0;
            {var subQ0=sQuery(id+"F4.wireOp",EDGE,"E56");var subQ3=sQuery(id+"F4.wireOp",EDGE,"E59.1.0.0");var subQ4=makeQuery(id+"F4.imprint","INTERSECT",VERTEX,{"derivedFrom":[subQ0,subQ3]});Q0=makeQuery(id+"F4.imprint","IMPRINT",FACE,{"disambiguationData":[TD([[makeQuery(id+"F4.imprint","IMPRINT",EDGE,{"disambiguationData":[TD([[subQ4,-1.0]])],"derivedFrom":subQ3}),-1.0]])]});}
            var Q1;
            {var subQ0=sQuery(id+"F4.wireOp",EDGE,"E59.1.0.0");var subQ1=sQuery(id+"F4.wireOp",EDGE,"E57.2.0.0");var subQ2=makeQuery(id+"F4.imprint","INTERSECT",VERTEX,{"derivedFrom":[subQ1,subQ0]});Q1=makeQuery(id+"F4.imprint","IMPRINT",FACE,{"disambiguationData":[TD([[makeQuery(id+"F4.imprint","IMPRINT",EDGE,{"disambiguationData":[TD([[subQ2,-1.0]])],"derivedFrom":subQ0}),-1.0]])]});}
            var Q2;
            {var subQ0=sQuery(id+"F4.wireOp",EDGE,"E57.1.0.0");var subQ4=sQuery(id+"F4.wireOp",EDGE,"E59.2.0.0");var subQ5=makeQuery(id+"F4.imprint","INTERSECT",VERTEX,{"derivedFrom":[subQ0,subQ4]});Q2=makeQuery(id+"F4.imprint","IMPRINT",FACE,{"disambiguationData":[TD([[makeQuery(id+"F4.imprint","IMPRINT",EDGE,{"disambiguationData":[TD([[subQ5,1.0]])],"derivedFrom":subQ0}),-1.0]])]});}
            var Q3;
            {var subQ0=sQuery(id+"F4.wireOp",EDGE,"E59.2.0.0");var subQ1=sQuery(id+"F4.wireOp",EDGE,"E57.1.0.0");var subQ2=makeQuery(id+"F4.imprint","INTERSECT",VERTEX,{"derivedFrom":[subQ1,subQ0]});Q3=makeQuery(id+"F4.imprint","IMPRINT",FACE,{"disambiguationData":[TD([[makeQuery(id+"F4.imprint","IMPRINT",EDGE,{"disambiguationData":[TD([[subQ2,-1.0]])],"derivedFrom":subQ1}),1.0]])]});}
            var Q4;
            {var subQ0=sQuery(id+"F4.wireOp",EDGE,"E59.3.0.0");var subQ1=sQuery(id+"F4.wireOp",EDGE,"E57.2.0.0");var subQ2=makeQuery(id+"F4.imprint","INTERSECT",VERTEX,{"derivedFrom":[subQ1,subQ0]});Q4=makeQuery(id+"F4.imprint","IMPRINT",FACE,{"disambiguationData":[TD([[makeQuery(id+"F4.imprint","IMPRINT",EDGE,{"disambiguationData":[TD([[subQ2,-1.0]])],"derivedFrom":subQ1}),1.0]])]});}
            var Q5;
            {var subQ0=sQuery(id+"F4.wireOp",EDGE,"E59.2.0.0");var subQ1=sQuery(id+"F4.wireOp",EDGE,"E57.3.0.0");var subQ2=makeQuery(id+"F4.imprint","INTERSECT",VERTEX,{"derivedFrom":[subQ1,subQ0]});Q5=makeQuery(id+"F4.imprint","IMPRINT",FACE,{"disambiguationData":[TD([[makeQuery(id+"F4.imprint","IMPRINT",EDGE,{"disambiguationData":[TD([[subQ2,-1.0]])],"derivedFrom":subQ1}),1.0]])]});}
            var Q6;
            {var subQ0=sQuery(id+"F4.wireOp",EDGE,"E57.5.0.0");var subQ6=sQuery(id+"F4.wireOp",EDGE,"E59.2.0.0");var subQ7=makeQuery(id+"F4.imprint","INTERSECT",VERTEX,{"derivedFrom":[subQ0,subQ6]});Q6=makeQuery(id+"F4.imprint","IMPRINT",FACE,{"disambiguationData":[TD([[makeQuery(id+"F4.imprint","IMPRINT",EDGE,{"disambiguationData":[TD([[subQ7,-1.0]])],"derivedFrom":subQ0}),1.0]])]});}
            var Q7;
            {var subQ0=sQuery(id+"F4.wireOp",EDGE,"E59.3.0.0");var subQ1=sQuery(id+"F4.wireOp",EDGE,"E57.6.0.0");var subQ2=makeQuery(id+"F4.imprint","INTERSECT",VERTEX,{"derivedFrom":[subQ1,subQ0]});Q7=makeQuery(id+"F4.imprint","IMPRINT",FACE,{"disambiguationData":[TD([[makeQuery(id+"F4.imprint","IMPRINT",EDGE,{"disambiguationData":[TD([[subQ2,-1.0]])],"derivedFrom":subQ1}),1.0]])]});}
            var Q8;
            {var subQ0=sQuery(id+"F4.wireOp",EDGE,"E59.3.0.0");var subQ1=sQuery(id+"F4.wireOp",EDGE,"E57.4.0.0");var subQ2=makeQuery(id+"F4.imprint","INTERSECT",VERTEX,{"derivedFrom":[subQ1,subQ0]});Q8=makeQuery(id+"F4.imprint","IMPRINT",FACE,{"disambiguationData":[TD([[makeQuery(id+"F4.imprint","IMPRINT",EDGE,{"disambiguationData":[TD([[subQ2,-1.0]])],"derivedFrom":subQ1}),1.0]])]});}
            var Q9;
            {var subQ0=sQuery(id+"F4.wireOp",EDGE,"E57.1.0.0");var subQ3=sQuery(id+"F4.wireOp",EDGE,"E59.3.0.0");var subQ4=makeQuery(id+"F4.imprint","INTERSECT",VERTEX,{"derivedFrom":[subQ0,subQ3]});Q9=makeQuery(id+"F4.imprint","IMPRINT",FACE,{"disambiguationData":[TD([[makeQuery(id+"F4.imprint","IMPRINT",EDGE,{"disambiguationData":[TD([[subQ4,-1.0]])],"derivedFrom":subQ3}),1.0]])]});}
            var Q10;
            {var subQ0=sQuery(id+"F4.wireOp",EDGE,"E59.4.0.0");var subQ1=sQuery(id+"F4.wireOp",EDGE,"E57.3.0.0");var subQ2=makeQuery(id+"F4.imprint","INTERSECT",VERTEX,{"derivedFrom":[subQ1,subQ0]});Q10=makeQuery(id+"F4.imprint","IMPRINT",FACE,{"disambiguationData":[TD([[makeQuery(id+"F4.imprint","IMPRINT",EDGE,{"disambiguationData":[TD([[subQ2,-1.0]])],"derivedFrom":subQ1}),1.0]])]});}
            var Q11;
            {var subQ0=sQuery(id+"F4.wireOp",EDGE,"E59.4.0.0");var subQ1=sQuery(id+"F4.wireOp",EDGE,"E57.5.0.0");var subQ2=makeQuery(id+"F4.imprint","INTERSECT",VERTEX,{"derivedFrom":[subQ1,subQ0]});Q11=makeQuery(id+"F4.imprint","IMPRINT",FACE,{"disambiguationData":[TD([[makeQuery(id+"F4.imprint","IMPRINT",EDGE,{"disambiguationData":[TD([[subQ2,-1.0]])],"derivedFrom":subQ1}),1.0]])]});}
            var Q12;
            {var subQ0=sQuery(id+"F4.wireOp",EDGE,"E59.4.0.0");var subQ1=sQuery(id+"F4.wireOp",EDGE,"E57.7.0.0");var subQ2=makeQuery(id+"F4.imprint","INTERSECT",VERTEX,{"derivedFrom":[subQ1,subQ0]});Q12=makeQuery(id+"F4.imprint","IMPRINT",FACE,{"disambiguationData":[TD([[makeQuery(id+"F4.imprint","IMPRINT",EDGE,{"disambiguationData":[TD([[subQ2,-1.0]])],"derivedFrom":subQ1}),1.0]])]});}
            var Q13;
            {var subQ0=sQuery(id+"F4.wireOp",EDGE,"E57.2.0.0");var subQ3=sQuery(id+"F4.wireOp",EDGE,"E59.4.0.0");var subQ4=makeQuery(id+"F4.imprint","INTERSECT",VERTEX,{"derivedFrom":[subQ0,subQ3]});Q13=makeQuery(id+"F4.imprint","IMPRINT",FACE,{"disambiguationData":[TD([[makeQuery(id+"F4.imprint","IMPRINT",EDGE,{"disambiguationData":[TD([[subQ4,-1.0]])],"derivedFrom":subQ3}),1.0]])]});}
            var Q14;
            {var subQ0=sQuery(id+"F4.wireOp",EDGE,"E59.5.0.0");var subQ1=sQuery(id+"F4.wireOp",EDGE,"E57.4.0.0");var subQ2=makeQuery(id+"F4.imprint","INTERSECT",VERTEX,{"derivedFrom":[subQ1,subQ0]});Q14=makeQuery(id+"F4.imprint","IMPRINT",FACE,{"disambiguationData":[TD([[makeQuery(id+"F4.imprint","IMPRINT",EDGE,{"disambiguationData":[TD([[subQ2,-1.0]])],"derivedFrom":subQ1}),1.0]])]});}
            var Q15;
            {var subQ0=sQuery(id+"F4.wireOp",EDGE,"E59.5.0.0");var subQ1=sQuery(id+"F4.wireOp",EDGE,"E57.6.0.0");var subQ2=makeQuery(id+"F4.imprint","INTERSECT",VERTEX,{"derivedFrom":[subQ1,subQ0]});Q15=makeQuery(id+"F4.imprint","IMPRINT",FACE,{"disambiguationData":[TD([[makeQuery(id+"F4.imprint","IMPRINT",EDGE,{"disambiguationData":[TD([[subQ2,-1.0]])],"derivedFrom":subQ1}),1.0]])]});}
            var Q16;
            {var subQ0=sQuery(id+"F4.wireOp",EDGE,"E59.5.0.0");var subQ1=sQuery(id+"F4.wireOp",EDGE,"E57.8.0.0");var subQ2=makeQuery(id+"F4.imprint","INTERSECT",VERTEX,{"derivedFrom":[subQ1,subQ0]});Q16=makeQuery(id+"F4.imprint","IMPRINT",FACE,{"disambiguationData":[TD([[makeQuery(id+"F4.imprint","IMPRINT",EDGE,{"disambiguationData":[TD([[subQ2,-1.0]])],"derivedFrom":subQ0}),-1.0]])]});}
            var Q17;
            {var subQ0=sQuery(id+"F4.wireOp",EDGE,"E59.5.0.0");var subQ1=sQuery(id+"F4.wireOp",EDGE,"E57.10.0.0");var subQ2=makeQuery(id+"F4.imprint","INTERSECT",VERTEX,{"derivedFrom":[subQ1,subQ0]});Q17=makeQuery(id+"F4.imprint","IMPRINT",FACE,{"disambiguationData":[TD([[makeQuery(id+"F4.imprint","IMPRINT",EDGE,{"disambiguationData":[TD([[subQ2,-1.0]])],"derivedFrom":subQ0}),-1.0]])]});}
            var Q18;
            {var subQ0=sQuery(id+"F4.wireOp",EDGE,"E57.3.0.0");var subQ3=sQuery(id+"F4.wireOp",EDGE,"E59.5.0.0");var subQ4=makeQuery(id+"F4.imprint","INTERSECT",VERTEX,{"derivedFrom":[subQ0,subQ3]});Q18=makeQuery(id+"F4.imprint","IMPRINT",FACE,{"disambiguationData":[TD([[makeQuery(id+"F4.imprint","IMPRINT",EDGE,{"disambiguationData":[TD([[subQ4,-1.0]])],"derivedFrom":subQ3}),1.0]])]});}
            var Q19;
            {var subQ0=sQuery(id+"F4.wireOp",EDGE,"E59.6.0.0");var subQ1=sQuery(id+"F4.wireOp",EDGE,"E57.5.0.0");var subQ2=makeQuery(id+"F4.imprint","INTERSECT",VERTEX,{"derivedFrom":[subQ1,subQ0]});Q19=makeQuery(id+"F4.imprint","IMPRINT",FACE,{"disambiguationData":[TD([[makeQuery(id+"F4.imprint","IMPRINT",EDGE,{"disambiguationData":[TD([[subQ2,-1.0]])],"derivedFrom":subQ1}),1.0]])]});}
            var Q20;
            {var subQ0=sQuery(id+"F4.wireOp",EDGE,"E59.6.0.0");var subQ1=sQuery(id+"F4.wireOp",EDGE,"E57.7.0.0");var subQ2=makeQuery(id+"F4.imprint","INTERSECT",VERTEX,{"derivedFrom":[subQ1,subQ0]});Q20=makeQuery(id+"F4.imprint","IMPRINT",FACE,{"disambiguationData":[TD([[makeQuery(id+"F4.imprint","IMPRINT",EDGE,{"disambiguationData":[TD([[subQ2,-1.0]])],"derivedFrom":subQ1}),1.0]])]});}
            var Q21;
            {var subQ0=sQuery(id+"F4.wireOp",EDGE,"E59.6.0.0");var subQ1=sQuery(id+"F4.wireOp",EDGE,"E57.9.0.0");var subQ2=makeQuery(id+"F4.imprint","INTERSECT",VERTEX,{"derivedFrom":[subQ1,subQ0]});Q21=makeQuery(id+"F4.imprint","IMPRINT",FACE,{"disambiguationData":[TD([[makeQuery(id+"F4.imprint","IMPRINT",EDGE,{"disambiguationData":[TD([[subQ2,-1.0]])],"derivedFrom":subQ1}),1.0]])]});}
            var Q22;
            {var subQ0=sQuery(id+"F4.wireOp",EDGE,"E59.6.0.0");var subQ1=sQuery(id+"F4.wireOp",EDGE,"E57.11.0.0");var subQ2=makeQuery(id+"F4.imprint","INTERSECT",VERTEX,{"derivedFrom":[subQ1,subQ0]});Q22=makeQuery(id+"F4.imprint","IMPRINT",FACE,{"disambiguationData":[TD([[makeQuery(id+"F4.imprint","IMPRINT",EDGE,{"disambiguationData":[TD([[subQ2,-1.0]])],"derivedFrom":subQ1}),1.0]])]});}
            var Q23;
            {var subQ0=sQuery(id+"F4.wireOp",EDGE,"E57.13.0.0");var subQ6=sQuery(id+"F4.wireOp",EDGE,"E59.6.0.0");var subQ7=makeQuery(id+"F4.imprint","INTERSECT",VERTEX,{"derivedFrom":[subQ0,subQ6]});Q23=makeQuery(id+"F4.imprint","IMPRINT",FACE,{"disambiguationData":[TD([[makeQuery(id+"F4.imprint","IMPRINT",EDGE,{"disambiguationData":[TD([[subQ7,-1.0]])],"derivedFrom":subQ0}),1.0]])]});}
            var Q24;
            {var subQ0=sQuery(id+"F4.wireOp",EDGE,"E57.4.0.0");var subQ3=sQuery(id+"F4.wireOp",EDGE,"E59.6.0.0");var subQ4=makeQuery(id+"F4.imprint","INTERSECT",VERTEX,{"derivedFrom":[subQ0,subQ3]});Q24=makeQuery(id+"F4.imprint","IMPRINT",FACE,{"disambiguationData":[TD([[makeQuery(id+"F4.imprint","IMPRINT",EDGE,{"disambiguationData":[TD([[subQ4,-1.0]])],"derivedFrom":subQ3}),1.0]])]});}
            var Q25;
            {var subQ0=sQuery(id+"F4.wireOp",EDGE,"E59.7.0.0");var subQ1=sQuery(id+"F4.wireOp",EDGE,"E57.6.0.0");var subQ2=makeQuery(id+"F4.imprint","INTERSECT",VERTEX,{"derivedFrom":[subQ1,subQ0]});Q25=makeQuery(id+"F4.imprint","IMPRINT",FACE,{"disambiguationData":[TD([[makeQuery(id+"F4.imprint","IMPRINT",EDGE,{"disambiguationData":[TD([[subQ2,-1.0]])],"derivedFrom":subQ1}),1.0]])]});}
            var Q26;
            {var subQ0=sQuery(id+"F4.wireOp",EDGE,"E59.7.0.0");var subQ1=sQuery(id+"F4.wireOp",EDGE,"E57.8.0.0");var subQ2=makeQuery(id+"F4.imprint","INTERSECT",VERTEX,{"derivedFrom":[subQ1,subQ0]});Q26=makeQuery(id+"F4.imprint","IMPRINT",FACE,{"disambiguationData":[TD([[makeQuery(id+"F4.imprint","IMPRINT",EDGE,{"disambiguationData":[TD([[subQ2,-1.0]])],"derivedFrom":subQ1}),1.0]])]});}
            var Q27;
            {var subQ0=sQuery(id+"F4.wireOp",EDGE,"E59.7.0.0");var subQ1=sQuery(id+"F4.wireOp",EDGE,"E57.10.0.0");var subQ2=makeQuery(id+"F4.imprint","INTERSECT",VERTEX,{"derivedFrom":[subQ1,subQ0]});Q27=makeQuery(id+"F4.imprint","IMPRINT",FACE,{"disambiguationData":[TD([[makeQuery(id+"F4.imprint","IMPRINT",EDGE,{"disambiguationData":[TD([[subQ2,-1.0]])],"derivedFrom":subQ1}),1.0]])]});}
            var Q28;
            {var subQ0=sQuery(id+"F4.wireOp",EDGE,"E57.5.0.0");var subQ3=sQuery(id+"F4.wireOp",EDGE,"E59.7.0.0");var subQ4=makeQuery(id+"F4.imprint","INTERSECT",VERTEX,{"derivedFrom":[subQ0,subQ3]});Q28=makeQuery(id+"F4.imprint","IMPRINT",FACE,{"disambiguationData":[TD([[makeQuery(id+"F4.imprint","IMPRINT",EDGE,{"disambiguationData":[TD([[subQ4,-1.0]])],"derivedFrom":subQ3}),1.0]])]});}
            var Q29;
            {var subQ0=sQuery(id+"F4.wireOp",EDGE,"E59.8.0.0");var subQ1=sQuery(id+"F4.wireOp",EDGE,"E57.7.0.0");var subQ2=makeQuery(id+"F4.imprint","INTERSECT",VERTEX,{"derivedFrom":[subQ1,subQ0]});Q29=makeQuery(id+"F4.imprint","IMPRINT",FACE,{"disambiguationData":[TD([[makeQuery(id+"F4.imprint","IMPRINT",EDGE,{"disambiguationData":[TD([[subQ2,-1.0]])],"derivedFrom":subQ1}),1.0]])]});}
            var Q30;
            {var subQ0=sQuery(id+"F4.wireOp",EDGE,"E59.8.0.0");var subQ1=sQuery(id+"F4.wireOp",EDGE,"E57.9.0.0");var subQ2=makeQuery(id+"F4.imprint","INTERSECT",VERTEX,{"derivedFrom":[subQ1,subQ0]});Q30=makeQuery(id+"F4.imprint","IMPRINT",FACE,{"disambiguationData":[TD([[makeQuery(id+"F4.imprint","IMPRINT",EDGE,{"disambiguationData":[TD([[subQ2,-1.0]])],"derivedFrom":subQ1}),1.0]])]});}
            var Q31;
            {var subQ0=sQuery(id+"F4.wireOp",EDGE,"E59.8.0.0");var subQ1=sQuery(id+"F4.wireOp",EDGE,"E57.11.0.0");var subQ2=makeQuery(id+"F4.imprint","INTERSECT",VERTEX,{"derivedFrom":[subQ1,subQ0]});Q31=makeQuery(id+"F4.imprint","IMPRINT",FACE,{"disambiguationData":[TD([[makeQuery(id+"F4.imprint","IMPRINT",EDGE,{"disambiguationData":[TD([[subQ2,-1.0]])],"derivedFrom":subQ1}),1.0]])]});}
            var Q32;
            {var subQ0=sQuery(id+"F4.wireOp",EDGE,"E59.8.0.0");var subQ1=sQuery(id+"F4.wireOp",EDGE,"E57.13.0.0");var subQ2=makeQuery(id+"F4.imprint","INTERSECT",VERTEX,{"derivedFrom":[subQ1,subQ0]});Q32=makeQuery(id+"F4.imprint","IMPRINT",FACE,{"disambiguationData":[TD([[makeQuery(id+"F4.imprint","IMPRINT",EDGE,{"disambiguationData":[TD([[subQ2,-1.0]])],"derivedFrom":subQ1}),1.0]])]});}
            var Q33;
            {var subQ0=sQuery(id+"F4.wireOp",EDGE,"E59.8.0.0");var subQ1=sQuery(id+"F4.wireOp",EDGE,"E57.15.0.0");var subQ2=makeQuery(id+"F4.imprint","INTERSECT",VERTEX,{"derivedFrom":[subQ1,subQ0]});Q33=makeQuery(id+"F4.imprint","IMPRINT",FACE,{"disambiguationData":[TD([[makeQuery(id+"F4.imprint","IMPRINT",EDGE,{"disambiguationData":[TD([[subQ2,-1.0]])],"derivedFrom":subQ1}),1.0]])]});}
            var Q34;
            {var subQ0=sQuery(id+"F4.wireOp",EDGE,"E57.14.0.0");var subQ4=sQuery(id+"F4.wireOp",EDGE,"E59.7.0.0");var subQ5=makeQuery(id+"F4.imprint","INTERSECT",VERTEX,{"derivedFrom":[subQ0,subQ4]});Q34=makeQuery(id+"F4.imprint","IMPRINT",FACE,{"disambiguationData":[TD([[makeQuery(id+"F4.imprint","IMPRINT",EDGE,{"disambiguationData":[TD([[subQ5,1.0]])],"derivedFrom":subQ0}),-1.0]])]});}
            var Q35;
            {var subQ0=sQuery(id+"F4.wireOp",EDGE,"E57.13.0.0");var subQ4=sQuery(id+"F4.wireOp",EDGE,"E59.6.0.0");var subQ5=makeQuery(id+"F4.imprint","INTERSECT",VERTEX,{"derivedFrom":[subQ0,subQ4]});Q35=makeQuery(id+"F4.imprint","IMPRINT",FACE,{"disambiguationData":[TD([[makeQuery(id+"F4.imprint","IMPRINT",EDGE,{"disambiguationData":[TD([[subQ5,1.0]])],"derivedFrom":subQ0}),-1.0]])]});}
            var Q36;
            {var subQ0=sQuery(id+"F4.wireOp",EDGE,"E59.7.0.0");var subQ1=sQuery(id+"F4.wireOp",EDGE,"E57.14.0.0");var subQ2=makeQuery(id+"F4.imprint","INTERSECT",VERTEX,{"derivedFrom":[subQ1,subQ0]});Q36=makeQuery(id+"F4.imprint","IMPRINT",FACE,{"disambiguationData":[TD([[makeQuery(id+"F4.imprint","IMPRINT",EDGE,{"disambiguationData":[TD([[subQ2,-1.0]])],"derivedFrom":subQ1}),1.0]])]});}
            var Q37;
            {var subQ0=sQuery(id+"F4.wireOp",EDGE,"E57.6.0.0");var subQ3=sQuery(id+"F4.wireOp",EDGE,"E59.8.0.0");var subQ4=makeQuery(id+"F4.imprint","INTERSECT",VERTEX,{"derivedFrom":[subQ0,subQ3]});Q37=makeQuery(id+"F4.imprint","IMPRINT",FACE,{"disambiguationData":[TD([[makeQuery(id+"F4.imprint","IMPRINT",EDGE,{"disambiguationData":[TD([[subQ4,-1.0]])],"derivedFrom":subQ3}),1.0]])]});}
            var Q38;
            {var subQ0=sQuery(id+"F4.wireOp",EDGE,"E59.9.0.0");var subQ1=sQuery(id+"F4.wireOp",EDGE,"E57.10.0.0");var subQ2=makeQuery(id+"F4.imprint","INTERSECT",VERTEX,{"derivedFrom":[subQ1,subQ0]});Q38=makeQuery(id+"F4.imprint","IMPRINT",FACE,{"disambiguationData":[TD([[makeQuery(id+"F4.imprint","IMPRINT",EDGE,{"disambiguationData":[TD([[subQ2,-1.0]])],"derivedFrom":subQ1}),1.0]])]});}
            var Q39;
            {var subQ0=sQuery(id+"F4.wireOp",EDGE,"E59.9.0.0");var subQ1=sQuery(id+"F4.wireOp",EDGE,"E57.12.0.0");var subQ2=makeQuery(id+"F4.imprint","INTERSECT",VERTEX,{"derivedFrom":[subQ1,subQ0]});Q39=makeQuery(id+"F4.imprint","IMPRINT",FACE,{"disambiguationData":[TD([[makeQuery(id+"F4.imprint","IMPRINT",EDGE,{"disambiguationData":[TD([[subQ2,-1.0]])],"derivedFrom":subQ1}),1.0]])]});}
            var Q40;
            {var subQ4=sQuery(id+"F4.wireOp",EDGE,"E59.9.0.0");var subQ6=sQuery(id+"F4.wireOp",EDGE,"E57.15.0.0");var subQ8=makeQuery(id+"F4.imprint","INTERSECT",VERTEX,{"derivedFrom":[subQ6,subQ4]});Q40=makeQuery(id+"F4.imprint","IMPRINT",FACE,{"disambiguationData":[TD([[makeQuery(id+"F4.imprint","IMPRINT",EDGE,{"disambiguationData":[TD([[subQ8,-1.0]])],"derivedFrom":subQ6}),-1.0]])]});}
            var Q41;
            {var subQ0=sQuery(id+"F4.wireOp",EDGE,"E59.9.0.0");var subQ1=sQuery(id+"F4.wireOp",EDGE,"E57.15.0.0");var subQ2=makeQuery(id+"F4.imprint","INTERSECT",VERTEX,{"derivedFrom":[subQ1,subQ0]});Q41=makeQuery(id+"F4.imprint","IMPRINT",FACE,{"disambiguationData":[TD([[makeQuery(id+"F4.imprint","IMPRINT",EDGE,{"disambiguationData":[TD([[subQ2,1.0]])],"derivedFrom":subQ1}),1.0]])]});}
            var Q42;
            {var subQ9=sQuery(id+"F4.wireOp",EDGE,"E59.9.0.0");var subQ10=sQuery(id+"F4.wireOp",EDGE,"E57.13.0.0");var subQ11=makeQuery(id+"F4.imprint","INTERSECT",VERTEX,{"derivedFrom":[subQ10,subQ9]});Q42=makeQuery(id+"F4.imprint","IMPRINT",FACE,{"disambiguationData":[TD([[makeQuery(id+"F4.imprint","IMPRINT",EDGE,{"disambiguationData":[TD([[subQ11,-1.0]])],"derivedFrom":subQ9}),1.0]])]});}
            var Q43;
            {var subQ0=sQuery(id+"F4.wireOp",EDGE,"E59.9.0.0");var subQ1=sQuery(id+"F4.wireOp",EDGE,"E57.11.0.0");var subQ2=makeQuery(id+"F4.imprint","INTERSECT",VERTEX,{"derivedFrom":[subQ1,subQ0]});Q43=makeQuery(id+"F4.imprint","IMPRINT",FACE,{"disambiguationData":[TD([[makeQuery(id+"F4.imprint","IMPRINT",EDGE,{"disambiguationData":[TD([[subQ2,-1.0]])],"derivedFrom":subQ0}),1.0]])]});}
            var Q44;
            {var subQ9=sQuery(id+"F4.wireOp",EDGE,"E59.9.0.0");var subQ10=sQuery(id+"F4.wireOp",EDGE,"E57.9.0.0");var subQ11=makeQuery(id+"F4.imprint","INTERSECT",VERTEX,{"derivedFrom":[subQ10,subQ9]});Q44=makeQuery(id+"F4.imprint","IMPRINT",FACE,{"disambiguationData":[TD([[makeQuery(id+"F4.imprint","IMPRINT",EDGE,{"disambiguationData":[TD([[subQ11,-1.0]])],"derivedFrom":subQ9}),1.0]])]});}
            var Q45;
            {var subQ0=sQuery(id+"F4.wireOp",EDGE,"E57.7.0.0");var subQ4=sQuery(id+"F4.wireOp",EDGE,"E59.9.0.0");var subQ5=makeQuery(id+"F4.imprint","INTERSECT",VERTEX,{"derivedFrom":[subQ0,subQ4]});Q45=makeQuery(id+"F4.imprint","IMPRINT",FACE,{"disambiguationData":[TD([[makeQuery(id+"F4.imprint","IMPRINT",EDGE,{"disambiguationData":[TD([[subQ5,-1.0]])],"derivedFrom":subQ4}),1.0]])]});}
            var Q46;
            {var subQ0=sQuery(id+"F4.wireOp",EDGE,"E59.9.0.0");var subQ1=sQuery(id+"F4.wireOp",EDGE,"E57.8.0.0");var subQ2=makeQuery(id+"F4.imprint","INTERSECT",VERTEX,{"derivedFrom":[subQ1,subQ0]});Q46=makeQuery(id+"F4.imprint","IMPRINT",FACE,{"disambiguationData":[TD([[makeQuery(id+"F4.imprint","IMPRINT",EDGE,{"disambiguationData":[TD([[subQ2,-1.0]])],"derivedFrom":subQ1}),1.0]])]});}
            extrude(context, id + "F5", {"entities" : qUnion([Q0, Q1, Q2, Q3, Q4, Q5, Q6, Q7, Q8, Q9, Q10, Q11, Q12, Q13, Q14, Q15, Q16, Q17, Q18, Q19, Q20, Q21, Q22, Q23, Q24, Q25, Q26, Q27, Q28, Q29, Q30, Q31, Q32, Q33, Q34, Q35, Q36, Q37, Q38, Q39, Q40, Q41, Q42, Q43, Q44, Q45, Q46]), "operationType" : NewBodyOperationType.REMOVE, "oppositeDirection" : true, "depth" : 2 * mm, "offsetDistance" : 25 * mm, "hasDraft" : true, "draftAngle" : 55 * degree, "draftPullDirection" : true});
        }
    });
